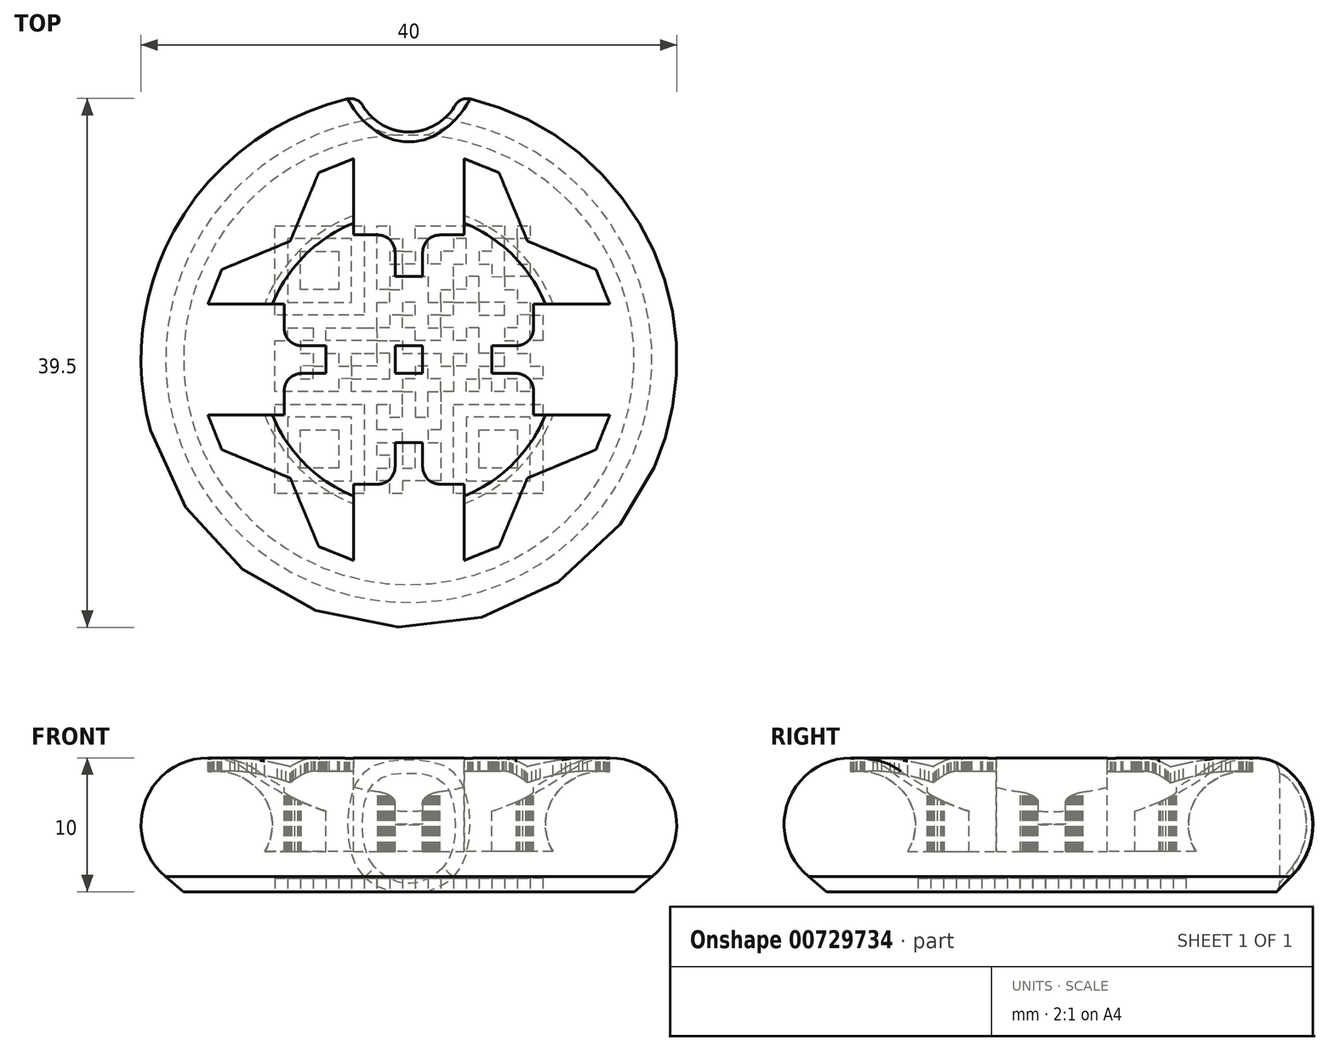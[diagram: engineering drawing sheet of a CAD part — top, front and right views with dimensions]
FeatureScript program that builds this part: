
annotation { "Feature Type Name" : "Feature", "Feature Type Description" : "" }
export const myFeature = defineFeature(function(context is Context, id is Id, definition is map)
    precondition{}
    {
        {
            var Q0;
            Q0=qCreatedBy(makeId("Front.planeOp"),FACE);
            var sketch = newSketch(context, id + "F0", { "sketchPlane" : qUnion([Q0])});
            skArc(sketch, "E0", {"start": v(-12, 9) * mm, "mid": v(-6.32, 6.03) * mm, "end": v(0, 5) * mm});
            skArc(sketch, "E1", {"start": v(-12, 9) * mm, "mid": v(-19.74, 6.58) * mm, "end": v(-15, 0) * mm});
            skLineSegment(sketch, "E2", {"start": v(0, 0) * mm, "end": v(-15, 0) * mm});
            skLineSegment(sketch, "E3", {"start": v(0, 0) * mm, "end": v(0, 5) * mm});
            skLineSegment(sketch, "E4", {"start": v(-18.21, 1.17) * mm, "end": v(-16.82, 0) * mm});
            skLineSegment(sketch, "E5", {"start": v(-16.82, 0) * mm, "end": v(-15, 0) * mm});
            skSolve(sketch);
        }
        {
            var Q0;
            Q0=qSketchRegion(id+"F0",true);
            var Q1;
            Q1=sQuery(id+"F0.wireOp",EDGE,"E3");
            revolve(context, id + "F1", {"surfaceOperationType" : NewSurfaceOperationType.NEW, "entities" : qUnion([Q0]), "axis" : qUnion([Q1]), "revolveType" : RevolveType.FULL});
        }
        {
            var Q0;
            Q0=qCreatedBy(makeId("Top.planeOp"),FACE);
            cPlane(context, id + "F2", {"entities" : qUnion([Q0]), "cplaneType" : CPlaneType.OFFSET, "offset" : 15 * mm, "width" : 150 * mm, "height" : 150 * mm});
        }
        {
            var Q0;
            Q0=qCreatedBy(id+"F2.planeOp",FACE);
            var sketch = newSketch(context, id + "F3", { "sketchPlane" : qUnion([Q0])});
            skLineSegment(sketch, "E6", {"start": v(9.31, -4.14) * mm, "end": v(9.31, -4.02) * mm});
            skLineSegment(sketch, "E7", {"start": v(9.31, -4.02) * mm, "end": v(9.31, -3.91) * mm});
            skLineSegment(sketch, "E8", {"start": v(9.31, -3.91) * mm, "end": v(9.31, -3.8) * mm});
            skLineSegment(sketch, "E9", {"start": v(9.31, -3.8) * mm, "end": v(9.31, -3.69) * mm});
            skLineSegment(sketch, "E10", {"start": v(9.31, -3.69) * mm, "end": v(9.31, -3.57) * mm});
            skLineSegment(sketch, "E11", {"start": v(9.31, -3.57) * mm, "end": v(9.31, -3.46) * mm});
            skLineSegment(sketch, "E12", {"start": v(9.31, -3.46) * mm, "end": v(9.31, -3.35) * mm});
            skLineSegment(sketch, "E13", {"start": v(9.31, -3.35) * mm, "end": v(9.31, -3.23) * mm});
            skLineSegment(sketch, "E14", {"start": v(9.31, -3.23) * mm, "end": v(9.31, -3.12) * mm});
            skLineSegment(sketch, "E15", {"start": v(9.31, -3.12) * mm, "end": v(9.31, -3) * mm});
            skLineSegment(sketch, "E16", {"start": v(9.31, -3) * mm, "end": v(9.31, -2.9) * mm});
            skLineSegment(sketch, "E17", {"start": v(9.31, -2.9) * mm, "end": v(9.31, -2.78) * mm});
            skLineSegment(sketch, "E18", {"start": v(9.31, -2.78) * mm, "end": v(9.31, -2.67) * mm});
            skLineSegment(sketch, "E19", {"start": v(9.31, -2.67) * mm, "end": v(9.31, -2.55) * mm});
            skLineSegment(sketch, "E20", {"start": v(9.31, -2.55) * mm, "end": v(9.31, -2.44) * mm});
            skLineSegment(sketch, "E21", {"start": v(9.31, -2.44) * mm, "end": v(9.31, -2.33) * mm});
            skLineSegment(sketch, "E22", {"start": v(9.31, -2.33) * mm, "end": v(9.3, -2.2) * mm});
            skLineSegment(sketch, "E23", {"start": v(9.3, -2.2) * mm, "end": v(9.28, -2.07) * mm});
            skLineSegment(sketch, "E24", {"start": v(9.28, -2.07) * mm, "end": v(9.25, -1.94) * mm});
            skLineSegment(sketch, "E25", {"start": v(9.25, -1.94) * mm, "end": v(9.2, -1.82) * mm});
            skLineSegment(sketch, "E26", {"start": v(9.2, -1.82) * mm, "end": v(9.15, -1.71) * mm});
            skLineSegment(sketch, "E27", {"start": v(9.15, -1.71) * mm, "end": v(9.09, -1.6) * mm});
            skLineSegment(sketch, "E28", {"start": v(9.09, -1.6) * mm, "end": v(9.02, -1.5) * mm});
            skLineSegment(sketch, "E29", {"start": v(9.02, -1.5) * mm, "end": v(8.93, -1.41) * mm});
            skLineSegment(sketch, "E30", {"start": v(8.93, -1.41) * mm, "end": v(8.84, -1.33) * mm});
            skLineSegment(sketch, "E31", {"start": v(8.84, -1.33) * mm, "end": v(8.74, -1.26) * mm});
            skLineSegment(sketch, "E32", {"start": v(8.74, -1.26) * mm, "end": v(8.63, -1.2) * mm});
            skLineSegment(sketch, "E33", {"start": v(8.63, -1.2) * mm, "end": v(8.52, -1.14) * mm});
            skLineSegment(sketch, "E34", {"start": v(8.52, -1.14) * mm, "end": v(8.4, -1.1) * mm});
            skLineSegment(sketch, "E35", {"start": v(8.4, -1.1) * mm, "end": v(8.28, -1.06) * mm});
            skLineSegment(sketch, "E36", {"start": v(8.28, -1.06) * mm, "end": v(8.15, -1.04) * mm});
            skLineSegment(sketch, "E37", {"start": v(8.15, -1.04) * mm, "end": v(8.02, -1.03) * mm});
            skLineSegment(sketch, "E38", {"start": v(8.02, -1.03) * mm, "end": v(7.9, -1.03) * mm});
            skLineSegment(sketch, "E39", {"start": v(7.9, -1.03) * mm, "end": v(7.8, -1.03) * mm});
            skLineSegment(sketch, "E40", {"start": v(7.8, -1.03) * mm, "end": v(7.68, -1.03) * mm});
            skLineSegment(sketch, "E41", {"start": v(7.68, -1.03) * mm, "end": v(7.56, -1.03) * mm});
            skLineSegment(sketch, "E42", {"start": v(7.56, -1.03) * mm, "end": v(7.45, -1.03) * mm});
            skLineSegment(sketch, "E43", {"start": v(7.45, -1.03) * mm, "end": v(7.34, -1.03) * mm});
            skLineSegment(sketch, "E44", {"start": v(7.34, -1.03) * mm, "end": v(7.23, -1.03) * mm});
            skLineSegment(sketch, "E45", {"start": v(7.23, -1.03) * mm, "end": v(7.11, -1.03) * mm});
            skLineSegment(sketch, "E46", {"start": v(7.11, -1.03) * mm, "end": v(7, -1.03) * mm});
            skLineSegment(sketch, "E47", {"start": v(7, -1.03) * mm, "end": v(6.89, -1.03) * mm});
            skLineSegment(sketch, "E48", {"start": v(6.89, -1.03) * mm, "end": v(6.77, -1.03) * mm});
            skLineSegment(sketch, "E49", {"start": v(6.77, -1.03) * mm, "end": v(6.66, -1.03) * mm});
            skLineSegment(sketch, "E50", {"start": v(6.66, -1.03) * mm, "end": v(6.55, -1.03) * mm});
            skLineSegment(sketch, "E51", {"start": v(6.55, -1.03) * mm, "end": v(6.43, -1.03) * mm});
            skLineSegment(sketch, "E52", {"start": v(6.43, -1.03) * mm, "end": v(6.32, -1.03) * mm});
            skLineSegment(sketch, "E53", {"start": v(6.32, -1.03) * mm, "end": v(6.2, -1.03) * mm});
            skLineSegment(sketch, "E54", {"start": v(6.2, -1.03) * mm, "end": v(6.2, -0.97) * mm});
            skLineSegment(sketch, "E55", {"start": v(6.2, -0.97) * mm, "end": v(6.2, -0.9) * mm});
            skLineSegment(sketch, "E56", {"start": v(6.2, -0.9) * mm, "end": v(6.2, -0.84) * mm});
            skLineSegment(sketch, "E57", {"start": v(6.2, -0.84) * mm, "end": v(6.2, -0.78) * mm});
            skLineSegment(sketch, "E58", {"start": v(6.2, -0.78) * mm, "end": v(6.2, -0.71) * mm});
            skLineSegment(sketch, "E59", {"start": v(6.2, -0.71) * mm, "end": v(6.2, -0.65) * mm});
            skLineSegment(sketch, "E60", {"start": v(6.2, -0.65) * mm, "end": v(6.2, -0.58) * mm});
            skLineSegment(sketch, "E61", {"start": v(6.2, -0.58) * mm, "end": v(6.2, -0.52) * mm});
            skLineSegment(sketch, "E62", {"start": v(6.2, -0.52) * mm, "end": v(6.2, -0.45) * mm});
            skLineSegment(sketch, "E63", {"start": v(6.2, -0.45) * mm, "end": v(6.2, -0.39) * mm});
            skLineSegment(sketch, "E64", {"start": v(6.2, -0.39) * mm, "end": v(6.2, -0.32) * mm});
            skLineSegment(sketch, "E65", {"start": v(6.2, -0.32) * mm, "end": v(6.2, -0.26) * mm});
            skLineSegment(sketch, "E66", {"start": v(6.2, -0.26) * mm, "end": v(6.2, -0.2) * mm});
            skLineSegment(sketch, "E67", {"start": v(6.2, -0.2) * mm, "end": v(6.2, -0.13) * mm});
            skLineSegment(sketch, "E68", {"start": v(6.2, -0.13) * mm, "end": v(6.2, -0.06) * mm});
            skLineSegment(sketch, "E69", {"start": v(6.2, -0.06) * mm, "end": v(6.2, 0) * mm});
            skLineSegment(sketch, "E70", {"start": v(6.2, 0) * mm, "end": v(6.2, 0.06) * mm});
            skLineSegment(sketch, "E71", {"start": v(6.2, 0.06) * mm, "end": v(6.2, 0.13) * mm});
            skLineSegment(sketch, "E72", {"start": v(6.2, 0.13) * mm, "end": v(6.2, 0.2) * mm});
            skLineSegment(sketch, "E73", {"start": v(6.2, 0.2) * mm, "end": v(6.2, 0.26) * mm});
            skLineSegment(sketch, "E74", {"start": v(6.2, 0.26) * mm, "end": v(6.2, 0.32) * mm});
            skLineSegment(sketch, "E75", {"start": v(6.2, 0.32) * mm, "end": v(6.2, 0.39) * mm});
            skLineSegment(sketch, "E76", {"start": v(6.2, 0.39) * mm, "end": v(6.2, 0.45) * mm});
            skLineSegment(sketch, "E77", {"start": v(6.2, 0.45) * mm, "end": v(6.2, 0.52) * mm});
            skLineSegment(sketch, "E78", {"start": v(6.2, 0.52) * mm, "end": v(6.2, 0.58) * mm});
            skLineSegment(sketch, "E79", {"start": v(6.2, 0.58) * mm, "end": v(6.2, 0.65) * mm});
            skLineSegment(sketch, "E80", {"start": v(6.2, 0.65) * mm, "end": v(6.2, 0.71) * mm});
            skLineSegment(sketch, "E81", {"start": v(6.2, 0.71) * mm, "end": v(6.2, 0.78) * mm});
            skLineSegment(sketch, "E82", {"start": v(6.2, 0.78) * mm, "end": v(6.2, 0.84) * mm});
            skLineSegment(sketch, "E83", {"start": v(6.2, 0.84) * mm, "end": v(6.2, 0.9) * mm});
            skLineSegment(sketch, "E84", {"start": v(6.2, 0.9) * mm, "end": v(6.2, 0.97) * mm});
            skLineSegment(sketch, "E85", {"start": v(6.2, 0.97) * mm, "end": v(6.2, 1.03) * mm});
            skLineSegment(sketch, "E86", {"start": v(6.2, 1.03) * mm, "end": v(6.32, 1.03) * mm});
            skLineSegment(sketch, "E87", {"start": v(6.32, 1.03) * mm, "end": v(6.43, 1.03) * mm});
            skLineSegment(sketch, "E88", {"start": v(6.43, 1.03) * mm, "end": v(6.55, 1.03) * mm});
            skLineSegment(sketch, "E89", {"start": v(6.55, 1.03) * mm, "end": v(6.66, 1.03) * mm});
            skLineSegment(sketch, "E90", {"start": v(6.66, 1.03) * mm, "end": v(6.77, 1.03) * mm});
            skLineSegment(sketch, "E91", {"start": v(6.77, 1.03) * mm, "end": v(6.89, 1.03) * mm});
            skLineSegment(sketch, "E92", {"start": v(6.89, 1.03) * mm, "end": v(7, 1.03) * mm});
            skLineSegment(sketch, "E93", {"start": v(7, 1.03) * mm, "end": v(7.11, 1.03) * mm});
            skLineSegment(sketch, "E94", {"start": v(7.11, 1.03) * mm, "end": v(7.23, 1.03) * mm});
            skLineSegment(sketch, "E95", {"start": v(7.23, 1.03) * mm, "end": v(7.34, 1.03) * mm});
            skLineSegment(sketch, "E96", {"start": v(7.34, 1.03) * mm, "end": v(7.45, 1.03) * mm});
            skLineSegment(sketch, "E97", {"start": v(7.45, 1.03) * mm, "end": v(7.56, 1.03) * mm});
            skLineSegment(sketch, "E98", {"start": v(7.56, 1.03) * mm, "end": v(7.68, 1.03) * mm});
            skLineSegment(sketch, "E99", {"start": v(7.68, 1.03) * mm, "end": v(7.8, 1.03) * mm});
            skLineSegment(sketch, "E100", {"start": v(7.8, 1.03) * mm, "end": v(7.9, 1.03) * mm});
            skLineSegment(sketch, "E101", {"start": v(7.9, 1.03) * mm, "end": v(8.02, 1.03) * mm});
            skLineSegment(sketch, "E102", {"start": v(8.02, 1.03) * mm, "end": v(8.15, 1.04) * mm});
            skLineSegment(sketch, "E103", {"start": v(8.15, 1.04) * mm, "end": v(8.28, 1.06) * mm});
            skLineSegment(sketch, "E104", {"start": v(8.28, 1.06) * mm, "end": v(8.4, 1.1) * mm});
            skLineSegment(sketch, "E105", {"start": v(8.4, 1.1) * mm, "end": v(8.52, 1.14) * mm});
            skLineSegment(sketch, "E106", {"start": v(8.52, 1.14) * mm, "end": v(8.63, 1.2) * mm});
            skLineSegment(sketch, "E107", {"start": v(8.63, 1.2) * mm, "end": v(8.74, 1.26) * mm});
            skLineSegment(sketch, "E108", {"start": v(8.74, 1.26) * mm, "end": v(8.84, 1.33) * mm});
            skLineSegment(sketch, "E109", {"start": v(8.84, 1.33) * mm, "end": v(8.93, 1.41) * mm});
            skLineSegment(sketch, "E110", {"start": v(8.93, 1.41) * mm, "end": v(9.02, 1.5) * mm});
            skLineSegment(sketch, "E111", {"start": v(9.02, 1.5) * mm, "end": v(9.09, 1.6) * mm});
            skLineSegment(sketch, "E112", {"start": v(9.09, 1.6) * mm, "end": v(9.15, 1.71) * mm});
            skLineSegment(sketch, "E113", {"start": v(9.15, 1.71) * mm, "end": v(9.2, 1.82) * mm});
            skLineSegment(sketch, "E114", {"start": v(9.2, 1.82) * mm, "end": v(9.25, 1.94) * mm});
            skLineSegment(sketch, "E115", {"start": v(9.25, 1.94) * mm, "end": v(9.28, 2.07) * mm});
            skLineSegment(sketch, "E116", {"start": v(9.28, 2.07) * mm, "end": v(9.3, 2.2) * mm});
            skLineSegment(sketch, "E117", {"start": v(9.3, 2.2) * mm, "end": v(9.31, 2.33) * mm});
            skLineSegment(sketch, "E118", {"start": v(9.31, 2.33) * mm, "end": v(9.31, 2.44) * mm});
            skLineSegment(sketch, "E119", {"start": v(9.31, 2.44) * mm, "end": v(9.31, 2.55) * mm});
            skLineSegment(sketch, "E120", {"start": v(9.31, 2.55) * mm, "end": v(9.31, 2.67) * mm});
            skLineSegment(sketch, "E121", {"start": v(9.31, 2.67) * mm, "end": v(9.31, 2.78) * mm});
            skLineSegment(sketch, "E122", {"start": v(9.31, 2.78) * mm, "end": v(9.31, 2.9) * mm});
            skLineSegment(sketch, "E123", {"start": v(9.31, 2.9) * mm, "end": v(9.31, 3) * mm});
            skLineSegment(sketch, "E124", {"start": v(9.31, 3) * mm, "end": v(9.31, 3.12) * mm});
            skLineSegment(sketch, "E125", {"start": v(9.31, 3.12) * mm, "end": v(9.31, 3.23) * mm});
            skLineSegment(sketch, "E126", {"start": v(9.31, 3.23) * mm, "end": v(9.31, 3.35) * mm});
            skLineSegment(sketch, "E127", {"start": v(9.31, 3.35) * mm, "end": v(9.31, 3.46) * mm});
            skLineSegment(sketch, "E128", {"start": v(9.31, 3.46) * mm, "end": v(9.31, 3.57) * mm});
            skLineSegment(sketch, "E129", {"start": v(9.31, 3.57) * mm, "end": v(9.31, 3.69) * mm});
            skLineSegment(sketch, "E130", {"start": v(9.31, 3.69) * mm, "end": v(9.31, 3.8) * mm});
            skLineSegment(sketch, "E131", {"start": v(9.31, 3.8) * mm, "end": v(9.31, 3.91) * mm});
            skLineSegment(sketch, "E132", {"start": v(9.31, 3.91) * mm, "end": v(9.31, 4.02) * mm});
            skLineSegment(sketch, "E133", {"start": v(9.31, 4.02) * mm, "end": v(9.31, 4.14) * mm});
            skLineSegment(sketch, "E134", {"start": v(9.31, 4.14) * mm, "end": v(9.44, 4.14) * mm});
            skLineSegment(sketch, "E135", {"start": v(9.44, 4.14) * mm, "end": v(9.57, 4.14) * mm});
            skLineSegment(sketch, "E136", {"start": v(9.57, 4.14) * mm, "end": v(9.7, 4.14) * mm});
            skLineSegment(sketch, "E137", {"start": v(9.7, 4.14) * mm, "end": v(9.83, 4.14) * mm});
            skLineSegment(sketch, "E138", {"start": v(9.83, 4.14) * mm, "end": v(9.96, 4.14) * mm});
            skLineSegment(sketch, "E139", {"start": v(9.96, 4.14) * mm, "end": v(10.09, 4.14) * mm});
            skLineSegment(sketch, "E140", {"start": v(10.09, 4.14) * mm, "end": v(10.22, 4.14) * mm});
            skLineSegment(sketch, "E141", {"start": v(10.22, 4.14) * mm, "end": v(10.34, 4.14) * mm});
            skLineSegment(sketch, "E142", {"start": v(10.34, 4.14) * mm, "end": v(10.47, 4.14) * mm});
            skLineSegment(sketch, "E143", {"start": v(10.47, 4.14) * mm, "end": v(10.6, 4.14) * mm});
            skLineSegment(sketch, "E144", {"start": v(10.6, 4.14) * mm, "end": v(10.73, 4.14) * mm});
            skLineSegment(sketch, "E145", {"start": v(10.73, 4.14) * mm, "end": v(10.86, 4.14) * mm});
            skLineSegment(sketch, "E146", {"start": v(10.86, 4.14) * mm, "end": v(11, 4.14) * mm});
            skLineSegment(sketch, "E147", {"start": v(11, 4.14) * mm, "end": v(11.12, 4.14) * mm});
            skLineSegment(sketch, "E148", {"start": v(11.12, 4.14) * mm, "end": v(11.25, 4.14) * mm});
            skLineSegment(sketch, "E149", {"start": v(11.25, 4.14) * mm, "end": v(11.38, 4.14) * mm});
            skLineSegment(sketch, "E150", {"start": v(11.38, 4.14) * mm, "end": v(11.6, 4.14) * mm});
            skLineSegment(sketch, "E151", {"start": v(11.6, 4.14) * mm, "end": v(11.83, 4.14) * mm});
            skLineSegment(sketch, "E152", {"start": v(11.83, 4.14) * mm, "end": v(12.06, 4.14) * mm});
            skLineSegment(sketch, "E153", {"start": v(12.06, 4.14) * mm, "end": v(12.28, 4.14) * mm});
            skLineSegment(sketch, "E154", {"start": v(12.28, 4.14) * mm, "end": v(12.51, 4.14) * mm});
            skLineSegment(sketch, "E155", {"start": v(12.51, 4.14) * mm, "end": v(12.74, 4.14) * mm});
            skLineSegment(sketch, "E156", {"start": v(12.74, 4.14) * mm, "end": v(12.96, 4.14) * mm});
            skLineSegment(sketch, "E157", {"start": v(12.96, 4.14) * mm, "end": v(13.19, 4.14) * mm});
            skLineSegment(sketch, "E158", {"start": v(13.19, 4.14) * mm, "end": v(13.42, 4.14) * mm});
            skLineSegment(sketch, "E159", {"start": v(13.42, 4.14) * mm, "end": v(13.64, 4.14) * mm});
            skLineSegment(sketch, "E160", {"start": v(13.64, 4.14) * mm, "end": v(13.87, 4.14) * mm});
            skLineSegment(sketch, "E161", {"start": v(13.87, 4.14) * mm, "end": v(14.1, 4.14) * mm});
            skLineSegment(sketch, "E162", {"start": v(14.1, 4.14) * mm, "end": v(14.32, 4.14) * mm});
            skLineSegment(sketch, "E163", {"start": v(14.32, 4.14) * mm, "end": v(14.55, 4.14) * mm});
            skLineSegment(sketch, "E164", {"start": v(14.55, 4.14) * mm, "end": v(14.77, 4.14) * mm});
            skLineSegment(sketch, "E165", {"start": v(14.77, 4.14) * mm, "end": v(15, 4.14) * mm});
            skLineSegment(sketch, "E166", {"start": v(15, 4.14) * mm, "end": v(14.95, 4.27) * mm});
            skLineSegment(sketch, "E167", {"start": v(14.95, 4.27) * mm, "end": v(14.9, 4.4) * mm});
            skLineSegment(sketch, "E168", {"start": v(14.9, 4.4) * mm, "end": v(14.84, 4.53) * mm});
            skLineSegment(sketch, "E169", {"start": v(14.84, 4.53) * mm, "end": v(14.8, 4.66) * mm});
            skLineSegment(sketch, "E170", {"start": v(14.8, 4.66) * mm, "end": v(14.74, 4.78) * mm});
            skLineSegment(sketch, "E171", {"start": v(14.74, 4.78) * mm, "end": v(14.69, 4.91) * mm});
            skLineSegment(sketch, "E172", {"start": v(14.69, 4.91) * mm, "end": v(14.64, 5.04) * mm});
            skLineSegment(sketch, "E173", {"start": v(14.64, 5.04) * mm, "end": v(14.59, 5.17) * mm});
            skLineSegment(sketch, "E174", {"start": v(14.59, 5.17) * mm, "end": v(14.53, 5.3) * mm});
            skLineSegment(sketch, "E175", {"start": v(14.53, 5.3) * mm, "end": v(14.48, 5.43) * mm});
            skLineSegment(sketch, "E176", {"start": v(14.48, 5.43) * mm, "end": v(14.43, 5.56) * mm});
            skLineSegment(sketch, "E177", {"start": v(14.43, 5.56) * mm, "end": v(14.38, 5.69) * mm});
            skLineSegment(sketch, "E178", {"start": v(14.38, 5.69) * mm, "end": v(14.33, 5.82) * mm});
            skLineSegment(sketch, "E179", {"start": v(14.33, 5.82) * mm, "end": v(14.28, 5.95) * mm});
            skLineSegment(sketch, "E180", {"start": v(14.28, 5.95) * mm, "end": v(14.22, 6.08) * mm});
            skLineSegment(sketch, "E181", {"start": v(14.22, 6.08) * mm, "end": v(14.17, 6.2) * mm});
            skLineSegment(sketch, "E182", {"start": v(14.17, 6.2) * mm, "end": v(14.16, 6.24) * mm});
            skLineSegment(sketch, "E183", {"start": v(14.16, 6.24) * mm, "end": v(14.15, 6.27) * mm});
            skLineSegment(sketch, "E184", {"start": v(14.15, 6.27) * mm, "end": v(14.13, 6.3) * mm});
            skLineSegment(sketch, "E185", {"start": v(14.13, 6.3) * mm, "end": v(14.12, 6.34) * mm});
            skLineSegment(sketch, "E186", {"start": v(14.12, 6.34) * mm, "end": v(14.1, 6.37) * mm});
            skLineSegment(sketch, "E187", {"start": v(14.1, 6.37) * mm, "end": v(14.1, 6.4) * mm});
            skLineSegment(sketch, "E188", {"start": v(14.1, 6.4) * mm, "end": v(14.08, 6.43) * mm});
            skLineSegment(sketch, "E189", {"start": v(14.08, 6.43) * mm, "end": v(14.07, 6.47) * mm});
            skLineSegment(sketch, "E190", {"start": v(14.07, 6.47) * mm, "end": v(14.06, 6.5) * mm});
            skLineSegment(sketch, "E191", {"start": v(14.06, 6.5) * mm, "end": v(14.04, 6.53) * mm});
            skLineSegment(sketch, "E192", {"start": v(14.04, 6.53) * mm, "end": v(14.03, 6.56) * mm});
            skLineSegment(sketch, "E193", {"start": v(14.03, 6.56) * mm, "end": v(14.02, 6.6) * mm});
            skLineSegment(sketch, "E194", {"start": v(14.02, 6.6) * mm, "end": v(14, 6.63) * mm});
            skLineSegment(sketch, "E195", {"start": v(14, 6.63) * mm, "end": v(14, 6.66) * mm});
            skLineSegment(sketch, "E196", {"start": v(14, 6.66) * mm, "end": v(13.98, 6.7) * mm});
            skLineSegment(sketch, "E197", {"start": v(13.98, 6.7) * mm, "end": v(13.97, 6.72) * mm});
            skLineSegment(sketch, "E198", {"start": v(13.97, 6.72) * mm, "end": v(13.65, 6.86) * mm});
            skLineSegment(sketch, "E199", {"start": v(13.65, 6.86) * mm, "end": v(13.33, 7) * mm});
            skLineSegment(sketch, "E200", {"start": v(13.33, 7) * mm, "end": v(13, 7.12) * mm});
            skLineSegment(sketch, "E201", {"start": v(13, 7.12) * mm, "end": v(12.69, 7.26) * mm});
            skLineSegment(sketch, "E202", {"start": v(12.69, 7.26) * mm, "end": v(12.37, 7.39) * mm});
            skLineSegment(sketch, "E203", {"start": v(12.37, 7.39) * mm, "end": v(12.05, 7.52) * mm});
            skLineSegment(sketch, "E204", {"start": v(12.05, 7.52) * mm, "end": v(11.73, 7.66) * mm});
            skLineSegment(sketch, "E205", {"start": v(11.73, 7.66) * mm, "end": v(11.4, 7.79) * mm});
            skLineSegment(sketch, "E206", {"start": v(11.4, 7.79) * mm, "end": v(11.1, 7.92) * mm});
            skLineSegment(sketch, "E207", {"start": v(11.1, 7.92) * mm, "end": v(10.77, 8.06) * mm});
            skLineSegment(sketch, "E208", {"start": v(10.77, 8.06) * mm, "end": v(10.45, 8.19) * mm});
            skLineSegment(sketch, "E209", {"start": v(10.45, 8.19) * mm, "end": v(10.13, 8.32) * mm});
            skLineSegment(sketch, "E210", {"start": v(10.13, 8.32) * mm, "end": v(9.81, 8.45) * mm});
            skLineSegment(sketch, "E211", {"start": v(9.81, 8.45) * mm, "end": v(9.5, 8.59) * mm});
            skLineSegment(sketch, "E212", {"start": v(9.5, 8.59) * mm, "end": v(9.17, 8.72) * mm});
            skLineSegment(sketch, "E213", {"start": v(9.17, 8.72) * mm, "end": v(8.85, 8.85) * mm});
            skLineSegment(sketch, "E214", {"start": v(8.85, 8.85) * mm, "end": v(8.72, 9.17) * mm});
            skLineSegment(sketch, "E215", {"start": v(8.72, 9.17) * mm, "end": v(8.59, 9.5) * mm});
            skLineSegment(sketch, "E216", {"start": v(8.59, 9.5) * mm, "end": v(8.45, 9.81) * mm});
            skLineSegment(sketch, "E217", {"start": v(8.45, 9.81) * mm, "end": v(8.32, 10.13) * mm});
            skLineSegment(sketch, "E218", {"start": v(8.32, 10.13) * mm, "end": v(8.19, 10.45) * mm});
            skLineSegment(sketch, "E219", {"start": v(8.19, 10.45) * mm, "end": v(8.06, 10.77) * mm});
            skLineSegment(sketch, "E220", {"start": v(8.06, 10.77) * mm, "end": v(7.92, 11.1) * mm});
            skLineSegment(sketch, "E221", {"start": v(7.92, 11.1) * mm, "end": v(7.79, 11.4) * mm});
            skLineSegment(sketch, "E222", {"start": v(7.79, 11.4) * mm, "end": v(7.66, 11.73) * mm});
            skLineSegment(sketch, "E223", {"start": v(7.66, 11.73) * mm, "end": v(7.52, 12.05) * mm});
            skLineSegment(sketch, "E224", {"start": v(7.52, 12.05) * mm, "end": v(7.39, 12.37) * mm});
            skLineSegment(sketch, "E225", {"start": v(7.39, 12.37) * mm, "end": v(7.26, 12.69) * mm});
            skLineSegment(sketch, "E226", {"start": v(7.26, 12.69) * mm, "end": v(7.12, 13) * mm});
            skLineSegment(sketch, "E227", {"start": v(7.12, 13) * mm, "end": v(7, 13.33) * mm});
            skLineSegment(sketch, "E228", {"start": v(7, 13.33) * mm, "end": v(6.86, 13.65) * mm});
            skLineSegment(sketch, "E229", {"start": v(6.86, 13.65) * mm, "end": v(6.72, 13.97) * mm});
            skLineSegment(sketch, "E230", {"start": v(6.72, 13.97) * mm, "end": v(6.7, 13.98) * mm});
            skLineSegment(sketch, "E231", {"start": v(6.7, 13.98) * mm, "end": v(6.66, 14) * mm});
            skLineSegment(sketch, "E232", {"start": v(6.66, 14) * mm, "end": v(6.63, 14) * mm});
            skLineSegment(sketch, "E233", {"start": v(6.63, 14) * mm, "end": v(6.6, 14.02) * mm});
            skLineSegment(sketch, "E234", {"start": v(6.6, 14.02) * mm, "end": v(6.56, 14.03) * mm});
            skLineSegment(sketch, "E235", {"start": v(6.56, 14.03) * mm, "end": v(6.53, 14.04) * mm});
            skLineSegment(sketch, "E236", {"start": v(6.53, 14.04) * mm, "end": v(6.5, 14.06) * mm});
            skLineSegment(sketch, "E237", {"start": v(6.5, 14.06) * mm, "end": v(6.47, 14.07) * mm});
            skLineSegment(sketch, "E238", {"start": v(6.47, 14.07) * mm, "end": v(6.43, 14.08) * mm});
            skLineSegment(sketch, "E239", {"start": v(6.43, 14.08) * mm, "end": v(6.4, 14.1) * mm});
            skLineSegment(sketch, "E240", {"start": v(6.4, 14.1) * mm, "end": v(6.37, 14.1) * mm});
            skLineSegment(sketch, "E241", {"start": v(6.37, 14.1) * mm, "end": v(6.34, 14.12) * mm});
            skLineSegment(sketch, "E242", {"start": v(6.34, 14.12) * mm, "end": v(6.3, 14.13) * mm});
            skLineSegment(sketch, "E243", {"start": v(6.3, 14.13) * mm, "end": v(6.27, 14.15) * mm});
            skLineSegment(sketch, "E244", {"start": v(6.27, 14.15) * mm, "end": v(6.24, 14.16) * mm});
            skLineSegment(sketch, "E245", {"start": v(6.24, 14.16) * mm, "end": v(6.2, 14.17) * mm});
            skLineSegment(sketch, "E246", {"start": v(6.2, 14.17) * mm, "end": v(6.08, 14.22) * mm});
            skLineSegment(sketch, "E247", {"start": v(6.08, 14.22) * mm, "end": v(5.95, 14.28) * mm});
            skLineSegment(sketch, "E248", {"start": v(5.95, 14.28) * mm, "end": v(5.82, 14.33) * mm});
            skLineSegment(sketch, "E249", {"start": v(5.82, 14.33) * mm, "end": v(5.69, 14.38) * mm});
            skLineSegment(sketch, "E250", {"start": v(5.69, 14.38) * mm, "end": v(5.56, 14.43) * mm});
            skLineSegment(sketch, "E251", {"start": v(5.56, 14.43) * mm, "end": v(5.43, 14.48) * mm});
            skLineSegment(sketch, "E252", {"start": v(5.43, 14.48) * mm, "end": v(5.3, 14.53) * mm});
            skLineSegment(sketch, "E253", {"start": v(5.3, 14.53) * mm, "end": v(5.17, 14.59) * mm});
            skLineSegment(sketch, "E254", {"start": v(5.17, 14.59) * mm, "end": v(5.04, 14.64) * mm});
            skLineSegment(sketch, "E255", {"start": v(5.04, 14.64) * mm, "end": v(4.91, 14.69) * mm});
            skLineSegment(sketch, "E256", {"start": v(4.91, 14.69) * mm, "end": v(4.78, 14.74) * mm});
            skLineSegment(sketch, "E257", {"start": v(4.78, 14.74) * mm, "end": v(4.66, 14.8) * mm});
            skLineSegment(sketch, "E258", {"start": v(4.66, 14.8) * mm, "end": v(4.53, 14.84) * mm});
            skLineSegment(sketch, "E259", {"start": v(4.53, 14.84) * mm, "end": v(4.4, 14.9) * mm});
            skLineSegment(sketch, "E260", {"start": v(4.4, 14.9) * mm, "end": v(4.27, 14.95) * mm});
            skLineSegment(sketch, "E261", {"start": v(4.27, 14.95) * mm, "end": v(4.14, 15) * mm});
            skLineSegment(sketch, "E262", {"start": v(4.14, 15) * mm, "end": v(4.14, 14.77) * mm});
            skLineSegment(sketch, "E263", {"start": v(4.14, 14.77) * mm, "end": v(4.14, 14.55) * mm});
            skLineSegment(sketch, "E264", {"start": v(4.14, 14.55) * mm, "end": v(4.14, 14.32) * mm});
            skLineSegment(sketch, "E265", {"start": v(4.14, 14.32) * mm, "end": v(4.14, 14.1) * mm});
            skLineSegment(sketch, "E266", {"start": v(4.14, 14.1) * mm, "end": v(4.14, 13.87) * mm});
            skLineSegment(sketch, "E267", {"start": v(4.14, 13.87) * mm, "end": v(4.14, 13.64) * mm});
            skLineSegment(sketch, "E268", {"start": v(4.14, 13.64) * mm, "end": v(4.14, 13.42) * mm});
            skLineSegment(sketch, "E269", {"start": v(4.14, 13.42) * mm, "end": v(4.14, 13.19) * mm});
            skLineSegment(sketch, "E270", {"start": v(4.14, 13.19) * mm, "end": v(4.14, 12.96) * mm});
            skLineSegment(sketch, "E271", {"start": v(4.14, 12.96) * mm, "end": v(4.14, 12.74) * mm});
            skLineSegment(sketch, "E272", {"start": v(4.14, 12.74) * mm, "end": v(4.14, 12.51) * mm});
            skLineSegment(sketch, "E273", {"start": v(4.14, 12.51) * mm, "end": v(4.14, 12.28) * mm});
            skLineSegment(sketch, "E274", {"start": v(4.14, 12.28) * mm, "end": v(4.14, 12.06) * mm});
            skLineSegment(sketch, "E275", {"start": v(4.14, 12.06) * mm, "end": v(4.14, 11.83) * mm});
            skLineSegment(sketch, "E276", {"start": v(4.14, 11.83) * mm, "end": v(4.14, 11.6) * mm});
            skLineSegment(sketch, "E277", {"start": v(4.14, 11.6) * mm, "end": v(4.14, 11.38) * mm});
            skLineSegment(sketch, "E278", {"start": v(4.14, 11.38) * mm, "end": v(4.14, 11.25) * mm});
            skLineSegment(sketch, "E279", {"start": v(4.14, 11.25) * mm, "end": v(4.14, 11.12) * mm});
            skLineSegment(sketch, "E280", {"start": v(4.14, 11.12) * mm, "end": v(4.14, 11) * mm});
            skLineSegment(sketch, "E281", {"start": v(4.14, 11) * mm, "end": v(4.14, 10.86) * mm});
            skLineSegment(sketch, "E282", {"start": v(4.14, 10.86) * mm, "end": v(4.14, 10.73) * mm});
            skLineSegment(sketch, "E283", {"start": v(4.14, 10.73) * mm, "end": v(4.14, 10.6) * mm});
            skLineSegment(sketch, "E284", {"start": v(4.14, 10.6) * mm, "end": v(4.14, 10.47) * mm});
            skLineSegment(sketch, "E285", {"start": v(4.14, 10.47) * mm, "end": v(4.14, 10.34) * mm});
            skLineSegment(sketch, "E286", {"start": v(4.14, 10.34) * mm, "end": v(4.14, 10.22) * mm});
            skLineSegment(sketch, "E287", {"start": v(4.14, 10.22) * mm, "end": v(4.14, 10.09) * mm});
            skLineSegment(sketch, "E288", {"start": v(4.14, 10.09) * mm, "end": v(4.14, 9.96) * mm});
            skLineSegment(sketch, "E289", {"start": v(4.14, 9.96) * mm, "end": v(4.14, 9.83) * mm});
            skLineSegment(sketch, "E290", {"start": v(4.14, 9.83) * mm, "end": v(4.14, 9.7) * mm});
            skLineSegment(sketch, "E291", {"start": v(4.14, 9.7) * mm, "end": v(4.14, 9.57) * mm});
            skLineSegment(sketch, "E292", {"start": v(4.14, 9.57) * mm, "end": v(4.14, 9.44) * mm});
            skLineSegment(sketch, "E293", {"start": v(4.14, 9.44) * mm, "end": v(4.14, 9.31) * mm});
            skLineSegment(sketch, "E294", {"start": v(4.14, 9.31) * mm, "end": v(4.02, 9.31) * mm});
            skLineSegment(sketch, "E295", {"start": v(4.02, 9.31) * mm, "end": v(3.91, 9.31) * mm});
            skLineSegment(sketch, "E296", {"start": v(3.91, 9.31) * mm, "end": v(3.8, 9.31) * mm});
            skLineSegment(sketch, "E297", {"start": v(3.8, 9.31) * mm, "end": v(3.69, 9.31) * mm});
            skLineSegment(sketch, "E298", {"start": v(3.69, 9.31) * mm, "end": v(3.57, 9.31) * mm});
            skLineSegment(sketch, "E299", {"start": v(3.57, 9.31) * mm, "end": v(3.46, 9.31) * mm});
            skLineSegment(sketch, "E300", {"start": v(3.46, 9.31) * mm, "end": v(3.35, 9.31) * mm});
            skLineSegment(sketch, "E301", {"start": v(3.35, 9.31) * mm, "end": v(3.23, 9.31) * mm});
            skLineSegment(sketch, "E302", {"start": v(3.23, 9.31) * mm, "end": v(3.12, 9.31) * mm});
            skLineSegment(sketch, "E303", {"start": v(3.12, 9.31) * mm, "end": v(3, 9.31) * mm});
            skLineSegment(sketch, "E304", {"start": v(3, 9.31) * mm, "end": v(2.9, 9.31) * mm});
            skLineSegment(sketch, "E305", {"start": v(2.9, 9.31) * mm, "end": v(2.78, 9.31) * mm});
            skLineSegment(sketch, "E306", {"start": v(2.78, 9.31) * mm, "end": v(2.67, 9.31) * mm});
            skLineSegment(sketch, "E307", {"start": v(2.67, 9.31) * mm, "end": v(2.55, 9.31) * mm});
            skLineSegment(sketch, "E308", {"start": v(2.55, 9.31) * mm, "end": v(2.44, 9.31) * mm});
            skLineSegment(sketch, "E309", {"start": v(2.44, 9.31) * mm, "end": v(2.33, 9.31) * mm});
            skLineSegment(sketch, "E310", {"start": v(2.33, 9.31) * mm, "end": v(2.2, 9.3) * mm});
            skLineSegment(sketch, "E311", {"start": v(2.2, 9.3) * mm, "end": v(2.07, 9.28) * mm});
            skLineSegment(sketch, "E312", {"start": v(2.07, 9.28) * mm, "end": v(1.94, 9.25) * mm});
            skLineSegment(sketch, "E313", {"start": v(1.94, 9.25) * mm, "end": v(1.82, 9.2) * mm});
            skLineSegment(sketch, "E314", {"start": v(1.82, 9.2) * mm, "end": v(1.71, 9.15) * mm});
            skLineSegment(sketch, "E315", {"start": v(1.71, 9.15) * mm, "end": v(1.6, 9.09) * mm});
            skLineSegment(sketch, "E316", {"start": v(1.6, 9.09) * mm, "end": v(1.5, 9.02) * mm});
            skLineSegment(sketch, "E317", {"start": v(1.5, 9.02) * mm, "end": v(1.41, 8.93) * mm});
            skLineSegment(sketch, "E318", {"start": v(1.41, 8.93) * mm, "end": v(1.33, 8.84) * mm});
            skLineSegment(sketch, "E319", {"start": v(1.33, 8.84) * mm, "end": v(1.26, 8.74) * mm});
            skLineSegment(sketch, "E320", {"start": v(1.26, 8.74) * mm, "end": v(1.2, 8.63) * mm});
            skLineSegment(sketch, "E321", {"start": v(1.2, 8.63) * mm, "end": v(1.14, 8.52) * mm});
            skLineSegment(sketch, "E322", {"start": v(1.14, 8.52) * mm, "end": v(1.1, 8.4) * mm});
            skLineSegment(sketch, "E323", {"start": v(1.1, 8.4) * mm, "end": v(1.06, 8.28) * mm});
            skLineSegment(sketch, "E324", {"start": v(1.06, 8.28) * mm, "end": v(1.04, 8.15) * mm});
            skLineSegment(sketch, "E325", {"start": v(1.04, 8.15) * mm, "end": v(1.03, 8.02) * mm});
            skLineSegment(sketch, "E326", {"start": v(1.03, 8.02) * mm, "end": v(1.03, 7.9) * mm});
            skLineSegment(sketch, "E327", {"start": v(1.03, 7.9) * mm, "end": v(1.03, 7.8) * mm});
            skLineSegment(sketch, "E328", {"start": v(1.03, 7.8) * mm, "end": v(1.03, 7.68) * mm});
            skLineSegment(sketch, "E329", {"start": v(1.03, 7.68) * mm, "end": v(1.03, 7.56) * mm});
            skLineSegment(sketch, "E330", {"start": v(1.03, 7.56) * mm, "end": v(1.03, 7.45) * mm});
            skLineSegment(sketch, "E331", {"start": v(1.03, 7.45) * mm, "end": v(1.03, 7.34) * mm});
            skLineSegment(sketch, "E332", {"start": v(1.03, 7.34) * mm, "end": v(1.03, 7.23) * mm});
            skLineSegment(sketch, "E333", {"start": v(1.03, 7.23) * mm, "end": v(1.03, 7.11) * mm});
            skLineSegment(sketch, "E334", {"start": v(1.03, 7.11) * mm, "end": v(1.03, 7) * mm});
            skLineSegment(sketch, "E335", {"start": v(1.03, 7) * mm, "end": v(1.03, 6.89) * mm});
            skLineSegment(sketch, "E336", {"start": v(1.03, 6.89) * mm, "end": v(1.03, 6.77) * mm});
            skLineSegment(sketch, "E337", {"start": v(1.03, 6.77) * mm, "end": v(1.03, 6.66) * mm});
            skLineSegment(sketch, "E338", {"start": v(1.03, 6.66) * mm, "end": v(1.03, 6.55) * mm});
            skLineSegment(sketch, "E339", {"start": v(1.03, 6.55) * mm, "end": v(1.03, 6.43) * mm});
            skLineSegment(sketch, "E340", {"start": v(1.03, 6.43) * mm, "end": v(1.03, 6.32) * mm});
            skLineSegment(sketch, "E341", {"start": v(1.03, 6.32) * mm, "end": v(1.03, 6.2) * mm});
            skLineSegment(sketch, "E342", {"start": v(1.03, 6.2) * mm, "end": v(0.97, 6.2) * mm});
            skLineSegment(sketch, "E343", {"start": v(0.97, 6.2) * mm, "end": v(0.9, 6.2) * mm});
            skLineSegment(sketch, "E344", {"start": v(0.9, 6.2) * mm, "end": v(0.84, 6.2) * mm});
            skLineSegment(sketch, "E345", {"start": v(0.84, 6.2) * mm, "end": v(0.78, 6.2) * mm});
            skLineSegment(sketch, "E346", {"start": v(0.78, 6.2) * mm, "end": v(0.71, 6.2) * mm});
            skLineSegment(sketch, "E347", {"start": v(0.71, 6.2) * mm, "end": v(0.65, 6.2) * mm});
            skLineSegment(sketch, "E348", {"start": v(0.65, 6.2) * mm, "end": v(0.58, 6.2) * mm});
            skLineSegment(sketch, "E349", {"start": v(0.58, 6.2) * mm, "end": v(0.52, 6.2) * mm});
            skLineSegment(sketch, "E350", {"start": v(0.52, 6.2) * mm, "end": v(0.45, 6.2) * mm});
            skLineSegment(sketch, "E351", {"start": v(0.45, 6.2) * mm, "end": v(0.39, 6.2) * mm});
            skLineSegment(sketch, "E352", {"start": v(0.39, 6.2) * mm, "end": v(0.32, 6.2) * mm});
            skLineSegment(sketch, "E353", {"start": v(0.32, 6.2) * mm, "end": v(0.26, 6.2) * mm});
            skLineSegment(sketch, "E354", {"start": v(0.26, 6.2) * mm, "end": v(0.2, 6.2) * mm});
            skLineSegment(sketch, "E355", {"start": v(0.2, 6.2) * mm, "end": v(0.13, 6.2) * mm});
            skLineSegment(sketch, "E356", {"start": v(0.13, 6.2) * mm, "end": v(0.06, 6.2) * mm});
            skLineSegment(sketch, "E357", {"start": v(0.06, 6.2) * mm, "end": v(0, 6.2) * mm});
            skLineSegment(sketch, "E358", {"start": v(0, 6.2) * mm, "end": v(-0.06, 6.2) * mm});
            skLineSegment(sketch, "E359", {"start": v(-0.06, 6.2) * mm, "end": v(-0.13, 6.2) * mm});
            skLineSegment(sketch, "E360", {"start": v(-0.13, 6.2) * mm, "end": v(-0.2, 6.2) * mm});
            skLineSegment(sketch, "E361", {"start": v(-0.2, 6.2) * mm, "end": v(-0.26, 6.2) * mm});
            skLineSegment(sketch, "E362", {"start": v(-0.26, 6.2) * mm, "end": v(-0.32, 6.2) * mm});
            skLineSegment(sketch, "E363", {"start": v(-0.32, 6.2) * mm, "end": v(-0.39, 6.2) * mm});
            skLineSegment(sketch, "E364", {"start": v(-0.39, 6.2) * mm, "end": v(-0.45, 6.2) * mm});
            skLineSegment(sketch, "E365", {"start": v(-0.45, 6.2) * mm, "end": v(-0.52, 6.2) * mm});
            skLineSegment(sketch, "E366", {"start": v(-0.52, 6.2) * mm, "end": v(-0.58, 6.2) * mm});
            skLineSegment(sketch, "E367", {"start": v(-0.58, 6.2) * mm, "end": v(-0.65, 6.2) * mm});
            skLineSegment(sketch, "E368", {"start": v(-0.65, 6.2) * mm, "end": v(-0.71, 6.2) * mm});
            skLineSegment(sketch, "E369", {"start": v(-0.71, 6.2) * mm, "end": v(-0.78, 6.2) * mm});
            skLineSegment(sketch, "E370", {"start": v(-0.78, 6.2) * mm, "end": v(-0.84, 6.2) * mm});
            skLineSegment(sketch, "E371", {"start": v(-0.84, 6.2) * mm, "end": v(-0.9, 6.2) * mm});
            skLineSegment(sketch, "E372", {"start": v(-0.9, 6.2) * mm, "end": v(-0.97, 6.2) * mm});
            skLineSegment(sketch, "E373", {"start": v(-0.97, 6.2) * mm, "end": v(-1.03, 6.2) * mm});
            skLineSegment(sketch, "E374", {"start": v(-1.03, 6.2) * mm, "end": v(-1.03, 6.32) * mm});
            skLineSegment(sketch, "E375", {"start": v(-1.03, 6.32) * mm, "end": v(-1.03, 6.43) * mm});
            skLineSegment(sketch, "E376", {"start": v(-1.03, 6.43) * mm, "end": v(-1.03, 6.55) * mm});
            skLineSegment(sketch, "E377", {"start": v(-1.03, 6.55) * mm, "end": v(-1.03, 6.66) * mm});
            skLineSegment(sketch, "E378", {"start": v(-1.03, 6.66) * mm, "end": v(-1.03, 6.77) * mm});
            skLineSegment(sketch, "E379", {"start": v(-1.03, 6.77) * mm, "end": v(-1.03, 6.89) * mm});
            skLineSegment(sketch, "E380", {"start": v(-1.03, 6.89) * mm, "end": v(-1.03, 7) * mm});
            skLineSegment(sketch, "E381", {"start": v(-1.03, 7) * mm, "end": v(-1.03, 7.11) * mm});
            skLineSegment(sketch, "E382", {"start": v(-1.03, 7.11) * mm, "end": v(-1.03, 7.23) * mm});
            skLineSegment(sketch, "E383", {"start": v(-1.03, 7.23) * mm, "end": v(-1.03, 7.34) * mm});
            skLineSegment(sketch, "E384", {"start": v(-1.03, 7.34) * mm, "end": v(-1.03, 7.45) * mm});
            skLineSegment(sketch, "E385", {"start": v(-1.03, 7.45) * mm, "end": v(-1.03, 7.56) * mm});
            skLineSegment(sketch, "E386", {"start": v(-1.03, 7.56) * mm, "end": v(-1.03, 7.68) * mm});
            skLineSegment(sketch, "E387", {"start": v(-1.03, 7.68) * mm, "end": v(-1.03, 7.8) * mm});
            skLineSegment(sketch, "E388", {"start": v(-1.03, 7.8) * mm, "end": v(-1.03, 7.9) * mm});
            skLineSegment(sketch, "E389", {"start": v(-1.03, 7.9) * mm, "end": v(-1.03, 8.02) * mm});
            skLineSegment(sketch, "E390", {"start": v(-1.03, 8.02) * mm, "end": v(-1.04, 8.15) * mm});
            skLineSegment(sketch, "E391", {"start": v(-1.04, 8.15) * mm, "end": v(-1.06, 8.28) * mm});
            skLineSegment(sketch, "E392", {"start": v(-1.06, 8.28) * mm, "end": v(-1.1, 8.4) * mm});
            skLineSegment(sketch, "E393", {"start": v(-1.1, 8.4) * mm, "end": v(-1.14, 8.52) * mm});
            skLineSegment(sketch, "E394", {"start": v(-1.14, 8.52) * mm, "end": v(-1.2, 8.63) * mm});
            skLineSegment(sketch, "E395", {"start": v(-1.2, 8.63) * mm, "end": v(-1.26, 8.74) * mm});
            skLineSegment(sketch, "E396", {"start": v(-1.26, 8.74) * mm, "end": v(-1.33, 8.84) * mm});
            skLineSegment(sketch, "E397", {"start": v(-1.33, 8.84) * mm, "end": v(-1.41, 8.93) * mm});
            skLineSegment(sketch, "E398", {"start": v(-1.41, 8.93) * mm, "end": v(-1.5, 9.02) * mm});
            skLineSegment(sketch, "E399", {"start": v(-1.5, 9.02) * mm, "end": v(-1.6, 9.09) * mm});
            skLineSegment(sketch, "E400", {"start": v(-1.6, 9.09) * mm, "end": v(-1.71, 9.15) * mm});
            skLineSegment(sketch, "E401", {"start": v(-1.71, 9.15) * mm, "end": v(-1.82, 9.2) * mm});
            skLineSegment(sketch, "E402", {"start": v(-1.82, 9.2) * mm, "end": v(-1.94, 9.25) * mm});
            skLineSegment(sketch, "E403", {"start": v(-1.94, 9.25) * mm, "end": v(-2.07, 9.28) * mm});
            skLineSegment(sketch, "E404", {"start": v(-2.07, 9.28) * mm, "end": v(-2.2, 9.3) * mm});
            skLineSegment(sketch, "E405", {"start": v(-2.2, 9.3) * mm, "end": v(-2.33, 9.31) * mm});
            skLineSegment(sketch, "E406", {"start": v(-2.33, 9.31) * mm, "end": v(-2.44, 9.31) * mm});
            skLineSegment(sketch, "E407", {"start": v(-2.44, 9.31) * mm, "end": v(-2.55, 9.31) * mm});
            skLineSegment(sketch, "E408", {"start": v(-2.55, 9.31) * mm, "end": v(-2.67, 9.31) * mm});
            skLineSegment(sketch, "E409", {"start": v(-2.67, 9.31) * mm, "end": v(-2.78, 9.31) * mm});
            skLineSegment(sketch, "E410", {"start": v(-2.78, 9.31) * mm, "end": v(-2.9, 9.31) * mm});
            skLineSegment(sketch, "E411", {"start": v(-2.9, 9.31) * mm, "end": v(-3, 9.31) * mm});
            skLineSegment(sketch, "E412", {"start": v(-3, 9.31) * mm, "end": v(-3.12, 9.31) * mm});
            skLineSegment(sketch, "E413", {"start": v(-3.12, 9.31) * mm, "end": v(-3.23, 9.31) * mm});
            skLineSegment(sketch, "E414", {"start": v(-3.23, 9.31) * mm, "end": v(-3.35, 9.31) * mm});
            skLineSegment(sketch, "E415", {"start": v(-3.35, 9.31) * mm, "end": v(-3.46, 9.31) * mm});
            skLineSegment(sketch, "E416", {"start": v(-3.46, 9.31) * mm, "end": v(-3.57, 9.31) * mm});
            skLineSegment(sketch, "E417", {"start": v(-3.57, 9.31) * mm, "end": v(-3.69, 9.31) * mm});
            skLineSegment(sketch, "E418", {"start": v(-3.69, 9.31) * mm, "end": v(-3.8, 9.31) * mm});
            skLineSegment(sketch, "E419", {"start": v(-3.8, 9.31) * mm, "end": v(-3.91, 9.31) * mm});
            skLineSegment(sketch, "E420", {"start": v(-3.91, 9.31) * mm, "end": v(-4.02, 9.31) * mm});
            skLineSegment(sketch, "E421", {"start": v(-4.02, 9.31) * mm, "end": v(-4.14, 9.31) * mm});
            skLineSegment(sketch, "E422", {"start": v(-4.14, 9.31) * mm, "end": v(-4.14, 9.44) * mm});
            skLineSegment(sketch, "E423", {"start": v(-4.14, 9.44) * mm, "end": v(-4.14, 9.57) * mm});
            skLineSegment(sketch, "E424", {"start": v(-4.14, 9.57) * mm, "end": v(-4.14, 9.7) * mm});
            skLineSegment(sketch, "E425", {"start": v(-4.14, 9.7) * mm, "end": v(-4.14, 9.83) * mm});
            skLineSegment(sketch, "E426", {"start": v(-4.14, 9.83) * mm, "end": v(-4.14, 9.96) * mm});
            skLineSegment(sketch, "E427", {"start": v(-4.14, 9.96) * mm, "end": v(-4.14, 10.09) * mm});
            skLineSegment(sketch, "E428", {"start": v(-4.14, 10.09) * mm, "end": v(-4.14, 10.22) * mm});
            skLineSegment(sketch, "E429", {"start": v(-4.14, 10.22) * mm, "end": v(-4.14, 10.34) * mm});
            skLineSegment(sketch, "E430", {"start": v(-4.14, 10.34) * mm, "end": v(-4.14, 10.47) * mm});
            skLineSegment(sketch, "E431", {"start": v(-4.14, 10.47) * mm, "end": v(-4.14, 10.6) * mm});
            skLineSegment(sketch, "E432", {"start": v(-4.14, 10.6) * mm, "end": v(-4.14, 10.73) * mm});
            skLineSegment(sketch, "E433", {"start": v(-4.14, 10.73) * mm, "end": v(-4.14, 10.86) * mm});
            skLineSegment(sketch, "E434", {"start": v(-4.14, 10.86) * mm, "end": v(-4.14, 11) * mm});
            skLineSegment(sketch, "E435", {"start": v(-4.14, 11) * mm, "end": v(-4.14, 11.12) * mm});
            skLineSegment(sketch, "E436", {"start": v(-4.14, 11.12) * mm, "end": v(-4.14, 11.25) * mm});
            skLineSegment(sketch, "E437", {"start": v(-4.14, 11.25) * mm, "end": v(-4.14, 11.38) * mm});
            skLineSegment(sketch, "E438", {"start": v(-4.14, 11.38) * mm, "end": v(-4.14, 11.6) * mm});
            skLineSegment(sketch, "E439", {"start": v(-4.14, 11.6) * mm, "end": v(-4.14, 11.83) * mm});
            skLineSegment(sketch, "E440", {"start": v(-4.14, 11.83) * mm, "end": v(-4.14, 12.06) * mm});
            skLineSegment(sketch, "E441", {"start": v(-4.14, 12.06) * mm, "end": v(-4.14, 12.28) * mm});
            skLineSegment(sketch, "E442", {"start": v(-4.14, 12.28) * mm, "end": v(-4.14, 12.51) * mm});
            skLineSegment(sketch, "E443", {"start": v(-4.14, 12.51) * mm, "end": v(-4.14, 12.74) * mm});
            skLineSegment(sketch, "E444", {"start": v(-4.14, 12.74) * mm, "end": v(-4.14, 12.96) * mm});
            skLineSegment(sketch, "E445", {"start": v(-4.14, 12.96) * mm, "end": v(-4.14, 13.19) * mm});
            skLineSegment(sketch, "E446", {"start": v(-4.14, 13.19) * mm, "end": v(-4.14, 13.42) * mm});
            skLineSegment(sketch, "E447", {"start": v(-4.14, 13.42) * mm, "end": v(-4.14, 13.64) * mm});
            skLineSegment(sketch, "E448", {"start": v(-4.14, 13.64) * mm, "end": v(-4.14, 13.87) * mm});
            skLineSegment(sketch, "E449", {"start": v(-4.14, 13.87) * mm, "end": v(-4.14, 14.1) * mm});
            skLineSegment(sketch, "E450", {"start": v(-4.14, 14.1) * mm, "end": v(-4.14, 14.32) * mm});
            skLineSegment(sketch, "E451", {"start": v(-4.14, 14.32) * mm, "end": v(-4.14, 14.55) * mm});
            skLineSegment(sketch, "E452", {"start": v(-4.14, 14.55) * mm, "end": v(-4.14, 14.77) * mm});
            skLineSegment(sketch, "E453", {"start": v(-4.14, 14.77) * mm, "end": v(-4.14, 15) * mm});
            skLineSegment(sketch, "E454", {"start": v(-4.14, 15) * mm, "end": v(-4.27, 14.95) * mm});
            skLineSegment(sketch, "E455", {"start": v(-4.27, 14.95) * mm, "end": v(-4.4, 14.9) * mm});
            skLineSegment(sketch, "E456", {"start": v(-4.4, 14.9) * mm, "end": v(-4.53, 14.84) * mm});
            skLineSegment(sketch, "E457", {"start": v(-4.53, 14.84) * mm, "end": v(-4.66, 14.8) * mm});
            skLineSegment(sketch, "E458", {"start": v(-4.66, 14.8) * mm, "end": v(-4.78, 14.74) * mm});
            skLineSegment(sketch, "E459", {"start": v(-4.78, 14.74) * mm, "end": v(-4.91, 14.69) * mm});
            skLineSegment(sketch, "E460", {"start": v(-4.91, 14.69) * mm, "end": v(-5.04, 14.64) * mm});
            skLineSegment(sketch, "E461", {"start": v(-5.04, 14.64) * mm, "end": v(-5.17, 14.59) * mm});
            skLineSegment(sketch, "E462", {"start": v(-5.17, 14.59) * mm, "end": v(-5.3, 14.53) * mm});
            skLineSegment(sketch, "E463", {"start": v(-5.3, 14.53) * mm, "end": v(-5.43, 14.48) * mm});
            skLineSegment(sketch, "E464", {"start": v(-5.43, 14.48) * mm, "end": v(-5.56, 14.43) * mm});
            skLineSegment(sketch, "E465", {"start": v(-5.56, 14.43) * mm, "end": v(-5.69, 14.38) * mm});
            skLineSegment(sketch, "E466", {"start": v(-5.69, 14.38) * mm, "end": v(-5.82, 14.33) * mm});
            skLineSegment(sketch, "E467", {"start": v(-5.82, 14.33) * mm, "end": v(-5.95, 14.28) * mm});
            skLineSegment(sketch, "E468", {"start": v(-5.95, 14.28) * mm, "end": v(-6.08, 14.22) * mm});
            skLineSegment(sketch, "E469", {"start": v(-6.08, 14.22) * mm, "end": v(-6.2, 14.17) * mm});
            skLineSegment(sketch, "E470", {"start": v(-6.2, 14.17) * mm, "end": v(-6.24, 14.16) * mm});
            skLineSegment(sketch, "E471", {"start": v(-6.24, 14.16) * mm, "end": v(-6.27, 14.15) * mm});
            skLineSegment(sketch, "E472", {"start": v(-6.27, 14.15) * mm, "end": v(-6.3, 14.13) * mm});
            skLineSegment(sketch, "E473", {"start": v(-6.3, 14.13) * mm, "end": v(-6.34, 14.12) * mm});
            skLineSegment(sketch, "E474", {"start": v(-6.34, 14.12) * mm, "end": v(-6.37, 14.1) * mm});
            skLineSegment(sketch, "E475", {"start": v(-6.37, 14.1) * mm, "end": v(-6.4, 14.1) * mm});
            skLineSegment(sketch, "E476", {"start": v(-6.4, 14.1) * mm, "end": v(-6.43, 14.08) * mm});
            skLineSegment(sketch, "E477", {"start": v(-6.43, 14.08) * mm, "end": v(-6.47, 14.07) * mm});
            skLineSegment(sketch, "E478", {"start": v(-6.47, 14.07) * mm, "end": v(-6.5, 14.06) * mm});
            skLineSegment(sketch, "E479", {"start": v(-6.5, 14.06) * mm, "end": v(-6.53, 14.04) * mm});
            skLineSegment(sketch, "E480", {"start": v(-6.53, 14.04) * mm, "end": v(-6.56, 14.03) * mm});
            skLineSegment(sketch, "E481", {"start": v(-6.56, 14.03) * mm, "end": v(-6.6, 14.02) * mm});
            skLineSegment(sketch, "E482", {"start": v(-6.6, 14.02) * mm, "end": v(-6.63, 14) * mm});
            skLineSegment(sketch, "E483", {"start": v(-6.63, 14) * mm, "end": v(-6.66, 14) * mm});
            skLineSegment(sketch, "E484", {"start": v(-6.66, 14) * mm, "end": v(-6.7, 13.98) * mm});
            skLineSegment(sketch, "E485", {"start": v(-6.7, 13.98) * mm, "end": v(-6.72, 13.97) * mm});
            skLineSegment(sketch, "E486", {"start": v(-6.72, 13.97) * mm, "end": v(-6.86, 13.65) * mm});
            skLineSegment(sketch, "E487", {"start": v(-6.86, 13.65) * mm, "end": v(-7, 13.33) * mm});
            skLineSegment(sketch, "E488", {"start": v(-7, 13.33) * mm, "end": v(-7.12, 13) * mm});
            skLineSegment(sketch, "E489", {"start": v(-7.12, 13) * mm, "end": v(-7.26, 12.69) * mm});
            skLineSegment(sketch, "E490", {"start": v(-7.26, 12.69) * mm, "end": v(-7.39, 12.37) * mm});
            skLineSegment(sketch, "E491", {"start": v(-7.39, 12.37) * mm, "end": v(-7.52, 12.05) * mm});
            skLineSegment(sketch, "E492", {"start": v(-7.52, 12.05) * mm, "end": v(-7.66, 11.73) * mm});
            skLineSegment(sketch, "E493", {"start": v(-7.66, 11.73) * mm, "end": v(-7.79, 11.4) * mm});
            skLineSegment(sketch, "E494", {"start": v(-7.79, 11.4) * mm, "end": v(-7.92, 11.1) * mm});
            skLineSegment(sketch, "E495", {"start": v(-7.92, 11.1) * mm, "end": v(-8.06, 10.77) * mm});
            skLineSegment(sketch, "E496", {"start": v(-8.06, 10.77) * mm, "end": v(-8.19, 10.45) * mm});
            skLineSegment(sketch, "E497", {"start": v(-8.19, 10.45) * mm, "end": v(-8.32, 10.13) * mm});
            skLineSegment(sketch, "E498", {"start": v(-8.32, 10.13) * mm, "end": v(-8.45, 9.81) * mm});
            skLineSegment(sketch, "E499", {"start": v(-8.45, 9.81) * mm, "end": v(-8.59, 9.5) * mm});
            skLineSegment(sketch, "E500", {"start": v(-8.59, 9.5) * mm, "end": v(-8.72, 9.17) * mm});
            skLineSegment(sketch, "E501", {"start": v(-8.72, 9.17) * mm, "end": v(-8.85, 8.85) * mm});
            skLineSegment(sketch, "E502", {"start": v(-8.85, 8.85) * mm, "end": v(-9.17, 8.72) * mm});
            skLineSegment(sketch, "E503", {"start": v(-9.17, 8.72) * mm, "end": v(-9.5, 8.59) * mm});
            skLineSegment(sketch, "E504", {"start": v(-9.5, 8.59) * mm, "end": v(-9.81, 8.45) * mm});
            skLineSegment(sketch, "E505", {"start": v(-9.81, 8.45) * mm, "end": v(-10.13, 8.32) * mm});
            skLineSegment(sketch, "E506", {"start": v(-10.13, 8.32) * mm, "end": v(-10.45, 8.19) * mm});
            skLineSegment(sketch, "E507", {"start": v(-10.45, 8.19) * mm, "end": v(-10.77, 8.06) * mm});
            skLineSegment(sketch, "E508", {"start": v(-10.77, 8.06) * mm, "end": v(-11.1, 7.92) * mm});
            skLineSegment(sketch, "E509", {"start": v(-11.1, 7.92) * mm, "end": v(-11.4, 7.79) * mm});
            skLineSegment(sketch, "E510", {"start": v(-11.4, 7.79) * mm, "end": v(-11.73, 7.66) * mm});
            skLineSegment(sketch, "E511", {"start": v(-11.73, 7.66) * mm, "end": v(-12.05, 7.52) * mm});
            skLineSegment(sketch, "E512", {"start": v(-12.05, 7.52) * mm, "end": v(-12.37, 7.39) * mm});
            skLineSegment(sketch, "E513", {"start": v(-12.37, 7.39) * mm, "end": v(-12.69, 7.26) * mm});
            skLineSegment(sketch, "E514", {"start": v(-12.69, 7.26) * mm, "end": v(-13, 7.12) * mm});
            skLineSegment(sketch, "E515", {"start": v(-13, 7.12) * mm, "end": v(-13.33, 7) * mm});
            skLineSegment(sketch, "E516", {"start": v(-13.33, 7) * mm, "end": v(-13.65, 6.86) * mm});
            skLineSegment(sketch, "E517", {"start": v(-13.65, 6.86) * mm, "end": v(-13.97, 6.72) * mm});
            skLineSegment(sketch, "E518", {"start": v(-13.97, 6.72) * mm, "end": v(-13.98, 6.7) * mm});
            skLineSegment(sketch, "E519", {"start": v(-13.98, 6.7) * mm, "end": v(-14, 6.66) * mm});
            skLineSegment(sketch, "E520", {"start": v(-14, 6.66) * mm, "end": v(-14, 6.63) * mm});
            skLineSegment(sketch, "E521", {"start": v(-14, 6.63) * mm, "end": v(-14.02, 6.6) * mm});
            skLineSegment(sketch, "E522", {"start": v(-14.02, 6.6) * mm, "end": v(-14.03, 6.56) * mm});
            skLineSegment(sketch, "E523", {"start": v(-14.03, 6.56) * mm, "end": v(-14.04, 6.53) * mm});
            skLineSegment(sketch, "E524", {"start": v(-14.04, 6.53) * mm, "end": v(-14.06, 6.5) * mm});
            skLineSegment(sketch, "E525", {"start": v(-14.06, 6.5) * mm, "end": v(-14.07, 6.47) * mm});
            skLineSegment(sketch, "E526", {"start": v(-14.07, 6.47) * mm, "end": v(-14.08, 6.43) * mm});
            skLineSegment(sketch, "E527", {"start": v(-14.08, 6.43) * mm, "end": v(-14.1, 6.4) * mm});
            skLineSegment(sketch, "E528", {"start": v(-14.1, 6.4) * mm, "end": v(-14.1, 6.37) * mm});
            skLineSegment(sketch, "E529", {"start": v(-14.1, 6.37) * mm, "end": v(-14.12, 6.34) * mm});
            skLineSegment(sketch, "E530", {"start": v(-14.12, 6.34) * mm, "end": v(-14.13, 6.3) * mm});
            skLineSegment(sketch, "E531", {"start": v(-14.13, 6.3) * mm, "end": v(-14.15, 6.27) * mm});
            skLineSegment(sketch, "E532", {"start": v(-14.15, 6.27) * mm, "end": v(-14.16, 6.24) * mm});
            skLineSegment(sketch, "E533", {"start": v(-14.16, 6.24) * mm, "end": v(-14.17, 6.2) * mm});
            skLineSegment(sketch, "E534", {"start": v(-14.17, 6.2) * mm, "end": v(-14.22, 6.08) * mm});
            skLineSegment(sketch, "E535", {"start": v(-14.22, 6.08) * mm, "end": v(-14.28, 5.95) * mm});
            skLineSegment(sketch, "E536", {"start": v(-14.28, 5.95) * mm, "end": v(-14.33, 5.82) * mm});
            skLineSegment(sketch, "E537", {"start": v(-14.33, 5.82) * mm, "end": v(-14.38, 5.69) * mm});
            skLineSegment(sketch, "E538", {"start": v(-14.38, 5.69) * mm, "end": v(-14.43, 5.56) * mm});
            skLineSegment(sketch, "E539", {"start": v(-14.43, 5.56) * mm, "end": v(-14.48, 5.43) * mm});
            skLineSegment(sketch, "E540", {"start": v(-14.48, 5.43) * mm, "end": v(-14.53, 5.3) * mm});
            skLineSegment(sketch, "E541", {"start": v(-14.53, 5.3) * mm, "end": v(-14.59, 5.17) * mm});
            skLineSegment(sketch, "E542", {"start": v(-14.59, 5.17) * mm, "end": v(-14.64, 5.04) * mm});
            skLineSegment(sketch, "E543", {"start": v(-14.64, 5.04) * mm, "end": v(-14.69, 4.91) * mm});
            skLineSegment(sketch, "E544", {"start": v(-14.69, 4.91) * mm, "end": v(-14.74, 4.78) * mm});
            skLineSegment(sketch, "E545", {"start": v(-14.74, 4.78) * mm, "end": v(-14.8, 4.66) * mm});
            skLineSegment(sketch, "E546", {"start": v(-14.8, 4.66) * mm, "end": v(-14.84, 4.53) * mm});
            skLineSegment(sketch, "E547", {"start": v(-14.84, 4.53) * mm, "end": v(-14.9, 4.4) * mm});
            skLineSegment(sketch, "E548", {"start": v(-14.9, 4.4) * mm, "end": v(-14.95, 4.27) * mm});
            skLineSegment(sketch, "E549", {"start": v(-14.95, 4.27) * mm, "end": v(-15, 4.14) * mm});
            skLineSegment(sketch, "E550", {"start": v(-15, 4.14) * mm, "end": v(-14.77, 4.14) * mm});
            skLineSegment(sketch, "E551", {"start": v(-14.77, 4.14) * mm, "end": v(-14.55, 4.14) * mm});
            skLineSegment(sketch, "E552", {"start": v(-14.55, 4.14) * mm, "end": v(-14.32, 4.14) * mm});
            skLineSegment(sketch, "E553", {"start": v(-14.32, 4.14) * mm, "end": v(-14.1, 4.14) * mm});
            skLineSegment(sketch, "E554", {"start": v(-14.1, 4.14) * mm, "end": v(-13.87, 4.14) * mm});
            skLineSegment(sketch, "E555", {"start": v(-13.87, 4.14) * mm, "end": v(-13.64, 4.14) * mm});
            skLineSegment(sketch, "E556", {"start": v(-13.64, 4.14) * mm, "end": v(-13.42, 4.14) * mm});
            skLineSegment(sketch, "E557", {"start": v(-13.42, 4.14) * mm, "end": v(-13.19, 4.14) * mm});
            skLineSegment(sketch, "E558", {"start": v(-13.19, 4.14) * mm, "end": v(-12.96, 4.14) * mm});
            skLineSegment(sketch, "E559", {"start": v(-12.96, 4.14) * mm, "end": v(-12.74, 4.14) * mm});
            skLineSegment(sketch, "E560", {"start": v(-12.74, 4.14) * mm, "end": v(-12.51, 4.14) * mm});
            skLineSegment(sketch, "E561", {"start": v(-12.51, 4.14) * mm, "end": v(-12.28, 4.14) * mm});
            skLineSegment(sketch, "E562", {"start": v(-12.28, 4.14) * mm, "end": v(-12.06, 4.14) * mm});
            skLineSegment(sketch, "E563", {"start": v(-12.06, 4.14) * mm, "end": v(-11.83, 4.14) * mm});
            skLineSegment(sketch, "E564", {"start": v(-11.83, 4.14) * mm, "end": v(-11.6, 4.14) * mm});
            skLineSegment(sketch, "E565", {"start": v(-11.6, 4.14) * mm, "end": v(-11.38, 4.14) * mm});
            skLineSegment(sketch, "E566", {"start": v(-11.38, 4.14) * mm, "end": v(-11.25, 4.14) * mm});
            skLineSegment(sketch, "E567", {"start": v(-11.25, 4.14) * mm, "end": v(-11.12, 4.14) * mm});
            skLineSegment(sketch, "E568", {"start": v(-11.12, 4.14) * mm, "end": v(-11, 4.14) * mm});
            skLineSegment(sketch, "E569", {"start": v(-11, 4.14) * mm, "end": v(-10.86, 4.14) * mm});
            skLineSegment(sketch, "E570", {"start": v(-10.86, 4.14) * mm, "end": v(-10.73, 4.14) * mm});
            skLineSegment(sketch, "E571", {"start": v(-10.73, 4.14) * mm, "end": v(-10.6, 4.14) * mm});
            skLineSegment(sketch, "E572", {"start": v(-10.6, 4.14) * mm, "end": v(-10.47, 4.14) * mm});
            skLineSegment(sketch, "E573", {"start": v(-10.47, 4.14) * mm, "end": v(-10.34, 4.14) * mm});
            skLineSegment(sketch, "E574", {"start": v(-10.34, 4.14) * mm, "end": v(-10.22, 4.14) * mm});
            skLineSegment(sketch, "E575", {"start": v(-10.22, 4.14) * mm, "end": v(-10.09, 4.14) * mm});
            skLineSegment(sketch, "E576", {"start": v(-10.09, 4.14) * mm, "end": v(-9.96, 4.14) * mm});
            skLineSegment(sketch, "E577", {"start": v(-9.96, 4.14) * mm, "end": v(-9.83, 4.14) * mm});
            skLineSegment(sketch, "E578", {"start": v(-9.83, 4.14) * mm, "end": v(-9.7, 4.14) * mm});
            skLineSegment(sketch, "E579", {"start": v(-9.7, 4.14) * mm, "end": v(-9.57, 4.14) * mm});
            skLineSegment(sketch, "E580", {"start": v(-9.57, 4.14) * mm, "end": v(-9.44, 4.14) * mm});
            skLineSegment(sketch, "E581", {"start": v(-9.44, 4.14) * mm, "end": v(-9.31, 4.14) * mm});
            skLineSegment(sketch, "E582", {"start": v(-9.31, 4.14) * mm, "end": v(-9.31, 4.02) * mm});
            skLineSegment(sketch, "E583", {"start": v(-9.31, 4.02) * mm, "end": v(-9.31, 3.91) * mm});
            skLineSegment(sketch, "E584", {"start": v(-9.31, 3.91) * mm, "end": v(-9.31, 3.8) * mm});
            skLineSegment(sketch, "E585", {"start": v(-9.31, 3.8) * mm, "end": v(-9.31, 3.69) * mm});
            skLineSegment(sketch, "E586", {"start": v(-9.31, 3.69) * mm, "end": v(-9.31, 3.57) * mm});
            skLineSegment(sketch, "E587", {"start": v(-9.31, 3.57) * mm, "end": v(-9.31, 3.46) * mm});
            skLineSegment(sketch, "E588", {"start": v(-9.31, 3.46) * mm, "end": v(-9.31, 3.35) * mm});
            skLineSegment(sketch, "E589", {"start": v(-9.31, 3.35) * mm, "end": v(-9.31, 3.23) * mm});
            skLineSegment(sketch, "E590", {"start": v(-9.31, 3.23) * mm, "end": v(-9.31, 3.12) * mm});
            skLineSegment(sketch, "E591", {"start": v(-9.31, 3.12) * mm, "end": v(-9.31, 3) * mm});
            skLineSegment(sketch, "E592", {"start": v(-9.31, 3) * mm, "end": v(-9.31, 2.9) * mm});
            skLineSegment(sketch, "E593", {"start": v(-9.31, 2.9) * mm, "end": v(-9.31, 2.78) * mm});
            skLineSegment(sketch, "E594", {"start": v(-9.31, 2.78) * mm, "end": v(-9.31, 2.67) * mm});
            skLineSegment(sketch, "E595", {"start": v(-9.31, 2.67) * mm, "end": v(-9.31, 2.55) * mm});
            skLineSegment(sketch, "E596", {"start": v(-9.31, 2.55) * mm, "end": v(-9.31, 2.44) * mm});
            skLineSegment(sketch, "E597", {"start": v(-9.31, 2.44) * mm, "end": v(-9.31, 2.33) * mm});
            skLineSegment(sketch, "E598", {"start": v(-9.31, 2.33) * mm, "end": v(-9.3, 2.2) * mm});
            skLineSegment(sketch, "E599", {"start": v(-9.3, 2.2) * mm, "end": v(-9.28, 2.07) * mm});
            skLineSegment(sketch, "E600", {"start": v(-9.28, 2.07) * mm, "end": v(-9.25, 1.94) * mm});
            skLineSegment(sketch, "E601", {"start": v(-9.25, 1.94) * mm, "end": v(-9.2, 1.82) * mm});
            skLineSegment(sketch, "E602", {"start": v(-9.2, 1.82) * mm, "end": v(-9.15, 1.71) * mm});
            skLineSegment(sketch, "E603", {"start": v(-9.15, 1.71) * mm, "end": v(-9.09, 1.6) * mm});
            skLineSegment(sketch, "E604", {"start": v(-9.09, 1.6) * mm, "end": v(-9.02, 1.5) * mm});
            skLineSegment(sketch, "E605", {"start": v(-9.02, 1.5) * mm, "end": v(-8.93, 1.41) * mm});
            skLineSegment(sketch, "E606", {"start": v(-8.93, 1.41) * mm, "end": v(-8.84, 1.33) * mm});
            skLineSegment(sketch, "E607", {"start": v(-8.84, 1.33) * mm, "end": v(-8.74, 1.26) * mm});
            skLineSegment(sketch, "E608", {"start": v(-8.74, 1.26) * mm, "end": v(-8.63, 1.2) * mm});
            skLineSegment(sketch, "E609", {"start": v(-8.63, 1.2) * mm, "end": v(-8.52, 1.14) * mm});
            skLineSegment(sketch, "E610", {"start": v(-8.52, 1.14) * mm, "end": v(-8.4, 1.1) * mm});
            skLineSegment(sketch, "E611", {"start": v(-8.4, 1.1) * mm, "end": v(-8.28, 1.06) * mm});
            skLineSegment(sketch, "E612", {"start": v(-8.28, 1.06) * mm, "end": v(-8.15, 1.04) * mm});
            skLineSegment(sketch, "E613", {"start": v(-8.15, 1.04) * mm, "end": v(-8.02, 1.03) * mm});
            skLineSegment(sketch, "E614", {"start": v(-8.02, 1.03) * mm, "end": v(-7.9, 1.03) * mm});
            skLineSegment(sketch, "E615", {"start": v(-7.9, 1.03) * mm, "end": v(-7.8, 1.03) * mm});
            skLineSegment(sketch, "E616", {"start": v(-7.8, 1.03) * mm, "end": v(-7.68, 1.03) * mm});
            skLineSegment(sketch, "E617", {"start": v(-7.68, 1.03) * mm, "end": v(-7.56, 1.03) * mm});
            skLineSegment(sketch, "E618", {"start": v(-7.56, 1.03) * mm, "end": v(-7.45, 1.03) * mm});
            skLineSegment(sketch, "E619", {"start": v(-7.45, 1.03) * mm, "end": v(-7.34, 1.03) * mm});
            skLineSegment(sketch, "E620", {"start": v(-7.34, 1.03) * mm, "end": v(-7.23, 1.03) * mm});
            skLineSegment(sketch, "E621", {"start": v(-7.23, 1.03) * mm, "end": v(-7.11, 1.03) * mm});
            skLineSegment(sketch, "E622", {"start": v(-7.11, 1.03) * mm, "end": v(-7, 1.03) * mm});
            skLineSegment(sketch, "E623", {"start": v(-7, 1.03) * mm, "end": v(-6.89, 1.03) * mm});
            skLineSegment(sketch, "E624", {"start": v(-6.89, 1.03) * mm, "end": v(-6.77, 1.03) * mm});
            skLineSegment(sketch, "E625", {"start": v(-6.77, 1.03) * mm, "end": v(-6.66, 1.03) * mm});
            skLineSegment(sketch, "E626", {"start": v(-6.66, 1.03) * mm, "end": v(-6.55, 1.03) * mm});
            skLineSegment(sketch, "E627", {"start": v(-6.55, 1.03) * mm, "end": v(-6.43, 1.03) * mm});
            skLineSegment(sketch, "E628", {"start": v(-6.43, 1.03) * mm, "end": v(-6.32, 1.03) * mm});
            skLineSegment(sketch, "E629", {"start": v(-6.32, 1.03) * mm, "end": v(-6.2, 1.03) * mm});
            skLineSegment(sketch, "E630", {"start": v(-6.2, 1.03) * mm, "end": v(-6.2, 0.97) * mm});
            skLineSegment(sketch, "E631", {"start": v(-6.2, 0.97) * mm, "end": v(-6.2, 0.9) * mm});
            skLineSegment(sketch, "E632", {"start": v(-6.2, 0.9) * mm, "end": v(-6.2, 0.84) * mm});
            skLineSegment(sketch, "E633", {"start": v(-6.2, 0.84) * mm, "end": v(-6.2, 0.78) * mm});
            skLineSegment(sketch, "E634", {"start": v(-6.2, 0.78) * mm, "end": v(-6.2, 0.71) * mm});
            skLineSegment(sketch, "E635", {"start": v(-6.2, 0.71) * mm, "end": v(-6.2, 0.65) * mm});
            skLineSegment(sketch, "E636", {"start": v(-6.2, 0.65) * mm, "end": v(-6.2, 0.58) * mm});
            skLineSegment(sketch, "E637", {"start": v(-6.2, 0.58) * mm, "end": v(-6.2, 0.52) * mm});
            skLineSegment(sketch, "E638", {"start": v(-6.2, 0.52) * mm, "end": v(-6.2, 0.45) * mm});
            skLineSegment(sketch, "E639", {"start": v(-6.2, 0.45) * mm, "end": v(-6.2, 0.39) * mm});
            skLineSegment(sketch, "E640", {"start": v(-6.2, 0.39) * mm, "end": v(-6.2, 0.32) * mm});
            skLineSegment(sketch, "E641", {"start": v(-6.2, 0.32) * mm, "end": v(-6.2, 0.26) * mm});
            skLineSegment(sketch, "E642", {"start": v(-6.2, 0.26) * mm, "end": v(-6.2, 0.2) * mm});
            skLineSegment(sketch, "E643", {"start": v(-6.2, 0.2) * mm, "end": v(-6.2, 0.13) * mm});
            skLineSegment(sketch, "E644", {"start": v(-6.2, 0.13) * mm, "end": v(-6.2, 0.06) * mm});
            skLineSegment(sketch, "E645", {"start": v(-6.2, 0.06) * mm, "end": v(-6.2, 0) * mm});
            skLineSegment(sketch, "E646", {"start": v(-6.2, 0) * mm, "end": v(-6.2, -0.06) * mm});
            skLineSegment(sketch, "E647", {"start": v(-6.2, -0.06) * mm, "end": v(-6.2, -0.13) * mm});
            skLineSegment(sketch, "E648", {"start": v(-6.2, -0.13) * mm, "end": v(-6.2, -0.2) * mm});
            skLineSegment(sketch, "E649", {"start": v(-6.2, -0.2) * mm, "end": v(-6.2, -0.26) * mm});
            skLineSegment(sketch, "E650", {"start": v(-6.2, -0.26) * mm, "end": v(-6.2, -0.32) * mm});
            skLineSegment(sketch, "E651", {"start": v(-6.2, -0.32) * mm, "end": v(-6.2, -0.39) * mm});
            skLineSegment(sketch, "E652", {"start": v(-6.2, -0.39) * mm, "end": v(-6.2, -0.45) * mm});
            skLineSegment(sketch, "E653", {"start": v(-6.2, -0.45) * mm, "end": v(-6.2, -0.52) * mm});
            skLineSegment(sketch, "E654", {"start": v(-6.2, -0.52) * mm, "end": v(-6.2, -0.58) * mm});
            skLineSegment(sketch, "E655", {"start": v(-6.2, -0.58) * mm, "end": v(-6.2, -0.65) * mm});
            skLineSegment(sketch, "E656", {"start": v(-6.2, -0.65) * mm, "end": v(-6.2, -0.71) * mm});
            skLineSegment(sketch, "E657", {"start": v(-6.2, -0.71) * mm, "end": v(-6.2, -0.78) * mm});
            skLineSegment(sketch, "E658", {"start": v(-6.2, -0.78) * mm, "end": v(-6.2, -0.84) * mm});
            skLineSegment(sketch, "E659", {"start": v(-6.2, -0.84) * mm, "end": v(-6.2, -0.9) * mm});
            skLineSegment(sketch, "E660", {"start": v(-6.2, -0.9) * mm, "end": v(-6.2, -0.97) * mm});
            skLineSegment(sketch, "E661", {"start": v(-6.2, -0.97) * mm, "end": v(-6.2, -1.03) * mm});
            skLineSegment(sketch, "E662", {"start": v(-6.2, -1.03) * mm, "end": v(-6.32, -1.03) * mm});
            skLineSegment(sketch, "E663", {"start": v(-6.32, -1.03) * mm, "end": v(-6.43, -1.03) * mm});
            skLineSegment(sketch, "E664", {"start": v(-6.43, -1.03) * mm, "end": v(-6.55, -1.03) * mm});
            skLineSegment(sketch, "E665", {"start": v(-6.55, -1.03) * mm, "end": v(-6.66, -1.03) * mm});
            skLineSegment(sketch, "E666", {"start": v(-6.66, -1.03) * mm, "end": v(-6.77, -1.03) * mm});
            skLineSegment(sketch, "E667", {"start": v(-6.77, -1.03) * mm, "end": v(-6.89, -1.03) * mm});
            skLineSegment(sketch, "E668", {"start": v(-6.89, -1.03) * mm, "end": v(-7, -1.03) * mm});
            skLineSegment(sketch, "E669", {"start": v(-7, -1.03) * mm, "end": v(-7.11, -1.03) * mm});
            skLineSegment(sketch, "E670", {"start": v(-7.11, -1.03) * mm, "end": v(-7.23, -1.03) * mm});
            skLineSegment(sketch, "E671", {"start": v(-7.23, -1.03) * mm, "end": v(-7.34, -1.03) * mm});
            skLineSegment(sketch, "E672", {"start": v(-7.34, -1.03) * mm, "end": v(-7.45, -1.03) * mm});
            skLineSegment(sketch, "E673", {"start": v(-7.45, -1.03) * mm, "end": v(-7.56, -1.03) * mm});
            skLineSegment(sketch, "E674", {"start": v(-7.56, -1.03) * mm, "end": v(-7.68, -1.03) * mm});
            skLineSegment(sketch, "E675", {"start": v(-7.68, -1.03) * mm, "end": v(-7.8, -1.03) * mm});
            skLineSegment(sketch, "E676", {"start": v(-7.8, -1.03) * mm, "end": v(-7.9, -1.03) * mm});
            skLineSegment(sketch, "E677", {"start": v(-7.9, -1.03) * mm, "end": v(-8.02, -1.03) * mm});
            skLineSegment(sketch, "E678", {"start": v(-8.02, -1.03) * mm, "end": v(-8.15, -1.04) * mm});
            skLineSegment(sketch, "E679", {"start": v(-8.15, -1.04) * mm, "end": v(-8.28, -1.06) * mm});
            skLineSegment(sketch, "E680", {"start": v(-8.28, -1.06) * mm, "end": v(-8.4, -1.1) * mm});
            skLineSegment(sketch, "E681", {"start": v(-8.4, -1.1) * mm, "end": v(-8.52, -1.14) * mm});
            skLineSegment(sketch, "E682", {"start": v(-8.52, -1.14) * mm, "end": v(-8.63, -1.2) * mm});
            skLineSegment(sketch, "E683", {"start": v(-8.63, -1.2) * mm, "end": v(-8.74, -1.26) * mm});
            skLineSegment(sketch, "E684", {"start": v(-8.74, -1.26) * mm, "end": v(-8.84, -1.33) * mm});
            skLineSegment(sketch, "E685", {"start": v(-8.84, -1.33) * mm, "end": v(-8.93, -1.41) * mm});
            skLineSegment(sketch, "E686", {"start": v(-8.93, -1.41) * mm, "end": v(-9.02, -1.5) * mm});
            skLineSegment(sketch, "E687", {"start": v(-9.02, -1.5) * mm, "end": v(-9.09, -1.6) * mm});
            skLineSegment(sketch, "E688", {"start": v(-9.09, -1.6) * mm, "end": v(-9.15, -1.71) * mm});
            skLineSegment(sketch, "E689", {"start": v(-9.15, -1.71) * mm, "end": v(-9.2, -1.82) * mm});
            skLineSegment(sketch, "E690", {"start": v(-9.2, -1.82) * mm, "end": v(-9.25, -1.94) * mm});
            skLineSegment(sketch, "E691", {"start": v(-9.25, -1.94) * mm, "end": v(-9.28, -2.07) * mm});
            skLineSegment(sketch, "E692", {"start": v(-9.28, -2.07) * mm, "end": v(-9.3, -2.2) * mm});
            skLineSegment(sketch, "E693", {"start": v(-9.3, -2.2) * mm, "end": v(-9.31, -2.33) * mm});
            skLineSegment(sketch, "E694", {"start": v(-9.31, -2.33) * mm, "end": v(-9.31, -2.44) * mm});
            skLineSegment(sketch, "E695", {"start": v(-9.31, -2.44) * mm, "end": v(-9.31, -2.55) * mm});
            skLineSegment(sketch, "E696", {"start": v(-9.31, -2.55) * mm, "end": v(-9.31, -2.67) * mm});
            skLineSegment(sketch, "E697", {"start": v(-9.31, -2.67) * mm, "end": v(-9.31, -2.78) * mm});
            skLineSegment(sketch, "E698", {"start": v(-9.31, -2.78) * mm, "end": v(-9.31, -2.9) * mm});
            skLineSegment(sketch, "E699", {"start": v(-9.31, -2.9) * mm, "end": v(-9.31, -3) * mm});
            skLineSegment(sketch, "E700", {"start": v(-9.31, -3) * mm, "end": v(-9.31, -3.12) * mm});
            skLineSegment(sketch, "E701", {"start": v(-9.31, -3.12) * mm, "end": v(-9.31, -3.23) * mm});
            skLineSegment(sketch, "E702", {"start": v(-9.31, -3.23) * mm, "end": v(-9.31, -3.35) * mm});
            skLineSegment(sketch, "E703", {"start": v(-9.31, -3.35) * mm, "end": v(-9.31, -3.46) * mm});
            skLineSegment(sketch, "E704", {"start": v(-9.31, -3.46) * mm, "end": v(-9.31, -3.57) * mm});
            skLineSegment(sketch, "E705", {"start": v(-9.31, -3.57) * mm, "end": v(-9.31, -3.69) * mm});
            skLineSegment(sketch, "E706", {"start": v(-9.31, -3.69) * mm, "end": v(-9.31, -3.8) * mm});
            skLineSegment(sketch, "E707", {"start": v(-9.31, -3.8) * mm, "end": v(-9.31, -3.91) * mm});
            skLineSegment(sketch, "E708", {"start": v(-9.31, -3.91) * mm, "end": v(-9.31, -4.02) * mm});
            skLineSegment(sketch, "E709", {"start": v(-9.31, -4.02) * mm, "end": v(-9.31, -4.14) * mm});
            skLineSegment(sketch, "E710", {"start": v(-9.31, -4.14) * mm, "end": v(-9.44, -4.14) * mm});
            skLineSegment(sketch, "E711", {"start": v(-9.44, -4.14) * mm, "end": v(-9.57, -4.14) * mm});
            skLineSegment(sketch, "E712", {"start": v(-9.57, -4.14) * mm, "end": v(-9.7, -4.14) * mm});
            skLineSegment(sketch, "E713", {"start": v(-9.7, -4.14) * mm, "end": v(-9.83, -4.14) * mm});
            skLineSegment(sketch, "E714", {"start": v(-9.83, -4.14) * mm, "end": v(-9.96, -4.14) * mm});
            skLineSegment(sketch, "E715", {"start": v(-9.96, -4.14) * mm, "end": v(-10.09, -4.14) * mm});
            skLineSegment(sketch, "E716", {"start": v(-10.09, -4.14) * mm, "end": v(-10.22, -4.14) * mm});
            skLineSegment(sketch, "E717", {"start": v(-10.22, -4.14) * mm, "end": v(-10.34, -4.14) * mm});
            skLineSegment(sketch, "E718", {"start": v(-10.34, -4.14) * mm, "end": v(-10.47, -4.14) * mm});
            skLineSegment(sketch, "E719", {"start": v(-10.47, -4.14) * mm, "end": v(-10.6, -4.14) * mm});
            skLineSegment(sketch, "E720", {"start": v(-10.6, -4.14) * mm, "end": v(-10.73, -4.14) * mm});
            skLineSegment(sketch, "E721", {"start": v(-10.73, -4.14) * mm, "end": v(-10.86, -4.14) * mm});
            skLineSegment(sketch, "E722", {"start": v(-10.86, -4.14) * mm, "end": v(-11, -4.14) * mm});
            skLineSegment(sketch, "E723", {"start": v(-11, -4.14) * mm, "end": v(-11.12, -4.14) * mm});
            skLineSegment(sketch, "E724", {"start": v(-11.12, -4.14) * mm, "end": v(-11.25, -4.14) * mm});
            skLineSegment(sketch, "E725", {"start": v(-11.25, -4.14) * mm, "end": v(-11.38, -4.14) * mm});
            skLineSegment(sketch, "E726", {"start": v(-11.38, -4.14) * mm, "end": v(-11.6, -4.14) * mm});
            skLineSegment(sketch, "E727", {"start": v(-11.6, -4.14) * mm, "end": v(-11.83, -4.14) * mm});
            skLineSegment(sketch, "E728", {"start": v(-11.83, -4.14) * mm, "end": v(-12.06, -4.14) * mm});
            skLineSegment(sketch, "E729", {"start": v(-12.06, -4.14) * mm, "end": v(-12.28, -4.14) * mm});
            skLineSegment(sketch, "E730", {"start": v(-12.28, -4.14) * mm, "end": v(-12.51, -4.14) * mm});
            skLineSegment(sketch, "E731", {"start": v(-12.51, -4.14) * mm, "end": v(-12.74, -4.14) * mm});
            skLineSegment(sketch, "E732", {"start": v(-12.74, -4.14) * mm, "end": v(-12.96, -4.14) * mm});
            skLineSegment(sketch, "E733", {"start": v(-12.96, -4.14) * mm, "end": v(-13.19, -4.14) * mm});
            skLineSegment(sketch, "E734", {"start": v(-13.19, -4.14) * mm, "end": v(-13.42, -4.14) * mm});
            skLineSegment(sketch, "E735", {"start": v(-13.42, -4.14) * mm, "end": v(-13.64, -4.14) * mm});
            skLineSegment(sketch, "E736", {"start": v(-13.64, -4.14) * mm, "end": v(-13.87, -4.14) * mm});
            skLineSegment(sketch, "E737", {"start": v(-13.87, -4.14) * mm, "end": v(-14.1, -4.14) * mm});
            skLineSegment(sketch, "E738", {"start": v(-14.1, -4.14) * mm, "end": v(-14.32, -4.14) * mm});
            skLineSegment(sketch, "E739", {"start": v(-14.32, -4.14) * mm, "end": v(-14.55, -4.14) * mm});
            skLineSegment(sketch, "E740", {"start": v(-14.55, -4.14) * mm, "end": v(-14.77, -4.14) * mm});
            skLineSegment(sketch, "E741", {"start": v(-14.77, -4.14) * mm, "end": v(-15, -4.14) * mm});
            skLineSegment(sketch, "E742", {"start": v(-15, -4.14) * mm, "end": v(-14.95, -4.27) * mm});
            skLineSegment(sketch, "E743", {"start": v(-14.95, -4.27) * mm, "end": v(-14.9, -4.4) * mm});
            skLineSegment(sketch, "E744", {"start": v(-14.9, -4.4) * mm, "end": v(-14.84, -4.53) * mm});
            skLineSegment(sketch, "E745", {"start": v(-14.84, -4.53) * mm, "end": v(-14.8, -4.66) * mm});
            skLineSegment(sketch, "E746", {"start": v(-14.8, -4.66) * mm, "end": v(-14.74, -4.78) * mm});
            skLineSegment(sketch, "E747", {"start": v(-14.74, -4.78) * mm, "end": v(-14.69, -4.91) * mm});
            skLineSegment(sketch, "E748", {"start": v(-14.69, -4.91) * mm, "end": v(-14.64, -5.04) * mm});
            skLineSegment(sketch, "E749", {"start": v(-14.64, -5.04) * mm, "end": v(-14.59, -5.17) * mm});
            skLineSegment(sketch, "E750", {"start": v(-14.59, -5.17) * mm, "end": v(-14.53, -5.3) * mm});
            skLineSegment(sketch, "E751", {"start": v(-14.53, -5.3) * mm, "end": v(-14.48, -5.43) * mm});
            skLineSegment(sketch, "E752", {"start": v(-14.48, -5.43) * mm, "end": v(-14.43, -5.56) * mm});
            skLineSegment(sketch, "E753", {"start": v(-14.43, -5.56) * mm, "end": v(-14.38, -5.69) * mm});
            skLineSegment(sketch, "E754", {"start": v(-14.38, -5.69) * mm, "end": v(-14.33, -5.82) * mm});
            skLineSegment(sketch, "E755", {"start": v(-14.33, -5.82) * mm, "end": v(-14.28, -5.95) * mm});
            skLineSegment(sketch, "E756", {"start": v(-14.28, -5.95) * mm, "end": v(-14.22, -6.08) * mm});
            skLineSegment(sketch, "E757", {"start": v(-14.22, -6.08) * mm, "end": v(-14.17, -6.2) * mm});
            skLineSegment(sketch, "E758", {"start": v(-14.17, -6.2) * mm, "end": v(-14.16, -6.24) * mm});
            skLineSegment(sketch, "E759", {"start": v(-14.16, -6.24) * mm, "end": v(-14.15, -6.27) * mm});
            skLineSegment(sketch, "E760", {"start": v(-14.15, -6.27) * mm, "end": v(-14.13, -6.3) * mm});
            skLineSegment(sketch, "E761", {"start": v(-14.13, -6.3) * mm, "end": v(-14.12, -6.34) * mm});
            skLineSegment(sketch, "E762", {"start": v(-14.12, -6.34) * mm, "end": v(-14.1, -6.37) * mm});
            skLineSegment(sketch, "E763", {"start": v(-14.1, -6.37) * mm, "end": v(-14.1, -6.4) * mm});
            skLineSegment(sketch, "E764", {"start": v(-14.1, -6.4) * mm, "end": v(-14.08, -6.43) * mm});
            skLineSegment(sketch, "E765", {"start": v(-14.08, -6.43) * mm, "end": v(-14.07, -6.47) * mm});
            skLineSegment(sketch, "E766", {"start": v(-14.07, -6.47) * mm, "end": v(-14.06, -6.5) * mm});
            skLineSegment(sketch, "E767", {"start": v(-14.06, -6.5) * mm, "end": v(-14.04, -6.53) * mm});
            skLineSegment(sketch, "E768", {"start": v(-14.04, -6.53) * mm, "end": v(-14.03, -6.56) * mm});
            skLineSegment(sketch, "E769", {"start": v(-14.03, -6.56) * mm, "end": v(-14.02, -6.6) * mm});
            skLineSegment(sketch, "E770", {"start": v(-14.02, -6.6) * mm, "end": v(-14, -6.63) * mm});
            skLineSegment(sketch, "E771", {"start": v(-14, -6.63) * mm, "end": v(-14, -6.66) * mm});
            skLineSegment(sketch, "E772", {"start": v(-14, -6.66) * mm, "end": v(-13.98, -6.7) * mm});
            skLineSegment(sketch, "E773", {"start": v(-13.98, -6.7) * mm, "end": v(-13.97, -6.72) * mm});
            skLineSegment(sketch, "E774", {"start": v(-13.97, -6.72) * mm, "end": v(-13.65, -6.86) * mm});
            skLineSegment(sketch, "E775", {"start": v(-13.65, -6.86) * mm, "end": v(-13.33, -7) * mm});
            skLineSegment(sketch, "E776", {"start": v(-13.33, -7) * mm, "end": v(-13, -7.12) * mm});
            skLineSegment(sketch, "E777", {"start": v(-13, -7.12) * mm, "end": v(-12.69, -7.26) * mm});
            skLineSegment(sketch, "E778", {"start": v(-12.69, -7.26) * mm, "end": v(-12.37, -7.39) * mm});
            skLineSegment(sketch, "E779", {"start": v(-12.37, -7.39) * mm, "end": v(-12.05, -7.52) * mm});
            skLineSegment(sketch, "E780", {"start": v(-12.05, -7.52) * mm, "end": v(-11.73, -7.66) * mm});
            skLineSegment(sketch, "E781", {"start": v(-11.73, -7.66) * mm, "end": v(-11.4, -7.79) * mm});
            skLineSegment(sketch, "E782", {"start": v(-11.4, -7.79) * mm, "end": v(-11.1, -7.92) * mm});
            skLineSegment(sketch, "E783", {"start": v(-11.1, -7.92) * mm, "end": v(-10.77, -8.06) * mm});
            skLineSegment(sketch, "E784", {"start": v(-10.77, -8.06) * mm, "end": v(-10.45, -8.19) * mm});
            skLineSegment(sketch, "E785", {"start": v(-10.45, -8.19) * mm, "end": v(-10.13, -8.32) * mm});
            skLineSegment(sketch, "E786", {"start": v(-10.13, -8.32) * mm, "end": v(-9.81, -8.45) * mm});
            skLineSegment(sketch, "E787", {"start": v(-9.81, -8.45) * mm, "end": v(-9.5, -8.59) * mm});
            skLineSegment(sketch, "E788", {"start": v(-9.5, -8.59) * mm, "end": v(-9.17, -8.72) * mm});
            skLineSegment(sketch, "E789", {"start": v(-9.17, -8.72) * mm, "end": v(-8.85, -8.85) * mm});
            skLineSegment(sketch, "E790", {"start": v(-8.85, -8.85) * mm, "end": v(-8.72, -9.17) * mm});
            skLineSegment(sketch, "E791", {"start": v(-8.72, -9.17) * mm, "end": v(-8.59, -9.5) * mm});
            skLineSegment(sketch, "E792", {"start": v(-8.59, -9.5) * mm, "end": v(-8.45, -9.81) * mm});
            skLineSegment(sketch, "E793", {"start": v(-8.45, -9.81) * mm, "end": v(-8.32, -10.13) * mm});
            skLineSegment(sketch, "E794", {"start": v(-8.32, -10.13) * mm, "end": v(-8.19, -10.45) * mm});
            skLineSegment(sketch, "E795", {"start": v(-8.19, -10.45) * mm, "end": v(-8.06, -10.77) * mm});
            skLineSegment(sketch, "E796", {"start": v(-8.06, -10.77) * mm, "end": v(-7.92, -11.1) * mm});
            skLineSegment(sketch, "E797", {"start": v(-7.92, -11.1) * mm, "end": v(-7.79, -11.4) * mm});
            skLineSegment(sketch, "E798", {"start": v(-7.79, -11.4) * mm, "end": v(-7.66, -11.73) * mm});
            skLineSegment(sketch, "E799", {"start": v(-7.66, -11.73) * mm, "end": v(-7.52, -12.05) * mm});
            skLineSegment(sketch, "E800", {"start": v(-7.52, -12.05) * mm, "end": v(-7.39, -12.37) * mm});
            skLineSegment(sketch, "E801", {"start": v(-7.39, -12.37) * mm, "end": v(-7.26, -12.69) * mm});
            skLineSegment(sketch, "E802", {"start": v(-7.26, -12.69) * mm, "end": v(-7.12, -13) * mm});
            skLineSegment(sketch, "E803", {"start": v(-7.12, -13) * mm, "end": v(-7, -13.33) * mm});
            skLineSegment(sketch, "E804", {"start": v(-7, -13.33) * mm, "end": v(-6.86, -13.65) * mm});
            skLineSegment(sketch, "E805", {"start": v(-6.86, -13.65) * mm, "end": v(-6.72, -13.97) * mm});
            skLineSegment(sketch, "E806", {"start": v(-6.72, -13.97) * mm, "end": v(-6.7, -13.98) * mm});
            skLineSegment(sketch, "E807", {"start": v(-6.7, -13.98) * mm, "end": v(-6.66, -14) * mm});
            skLineSegment(sketch, "E808", {"start": v(-6.66, -14) * mm, "end": v(-6.63, -14) * mm});
            skLineSegment(sketch, "E809", {"start": v(-6.63, -14) * mm, "end": v(-6.6, -14.02) * mm});
            skLineSegment(sketch, "E810", {"start": v(-6.6, -14.02) * mm, "end": v(-6.56, -14.03) * mm});
            skLineSegment(sketch, "E811", {"start": v(-6.56, -14.03) * mm, "end": v(-6.53, -14.04) * mm});
            skLineSegment(sketch, "E812", {"start": v(-6.53, -14.04) * mm, "end": v(-6.5, -14.06) * mm});
            skLineSegment(sketch, "E813", {"start": v(-6.5, -14.06) * mm, "end": v(-6.47, -14.07) * mm});
            skLineSegment(sketch, "E814", {"start": v(-6.47, -14.07) * mm, "end": v(-6.43, -14.08) * mm});
            skLineSegment(sketch, "E815", {"start": v(-6.43, -14.08) * mm, "end": v(-6.4, -14.1) * mm});
            skLineSegment(sketch, "E816", {"start": v(-6.4, -14.1) * mm, "end": v(-6.37, -14.1) * mm});
            skLineSegment(sketch, "E817", {"start": v(-6.37, -14.1) * mm, "end": v(-6.34, -14.12) * mm});
            skLineSegment(sketch, "E818", {"start": v(-6.34, -14.12) * mm, "end": v(-6.3, -14.13) * mm});
            skLineSegment(sketch, "E819", {"start": v(-6.3, -14.13) * mm, "end": v(-6.27, -14.15) * mm});
            skLineSegment(sketch, "E820", {"start": v(-6.27, -14.15) * mm, "end": v(-6.24, -14.16) * mm});
            skLineSegment(sketch, "E821", {"start": v(-6.24, -14.16) * mm, "end": v(-6.2, -14.17) * mm});
            skLineSegment(sketch, "E822", {"start": v(-6.2, -14.17) * mm, "end": v(-6.08, -14.22) * mm});
            skLineSegment(sketch, "E823", {"start": v(-6.08, -14.22) * mm, "end": v(-5.95, -14.28) * mm});
            skLineSegment(sketch, "E824", {"start": v(-5.95, -14.28) * mm, "end": v(-5.82, -14.33) * mm});
            skLineSegment(sketch, "E825", {"start": v(-5.82, -14.33) * mm, "end": v(-5.69, -14.38) * mm});
            skLineSegment(sketch, "E826", {"start": v(-5.69, -14.38) * mm, "end": v(-5.56, -14.43) * mm});
            skLineSegment(sketch, "E827", {"start": v(-5.56, -14.43) * mm, "end": v(-5.43, -14.48) * mm});
            skLineSegment(sketch, "E828", {"start": v(-5.43, -14.48) * mm, "end": v(-5.3, -14.53) * mm});
            skLineSegment(sketch, "E829", {"start": v(-5.3, -14.53) * mm, "end": v(-5.17, -14.59) * mm});
            skLineSegment(sketch, "E830", {"start": v(-5.17, -14.59) * mm, "end": v(-5.04, -14.64) * mm});
            skLineSegment(sketch, "E831", {"start": v(-5.04, -14.64) * mm, "end": v(-4.91, -14.69) * mm});
            skLineSegment(sketch, "E832", {"start": v(-4.91, -14.69) * mm, "end": v(-4.78, -14.74) * mm});
            skLineSegment(sketch, "E833", {"start": v(-4.78, -14.74) * mm, "end": v(-4.66, -14.8) * mm});
            skLineSegment(sketch, "E834", {"start": v(-4.66, -14.8) * mm, "end": v(-4.53, -14.84) * mm});
            skLineSegment(sketch, "E835", {"start": v(-4.53, -14.84) * mm, "end": v(-4.4, -14.9) * mm});
            skLineSegment(sketch, "E836", {"start": v(-4.4, -14.9) * mm, "end": v(-4.27, -14.95) * mm});
            skLineSegment(sketch, "E837", {"start": v(-4.27, -14.95) * mm, "end": v(-4.14, -15) * mm});
            skLineSegment(sketch, "E838", {"start": v(-4.14, -15) * mm, "end": v(-4.14, -14.77) * mm});
            skLineSegment(sketch, "E839", {"start": v(-4.14, -14.77) * mm, "end": v(-4.14, -14.55) * mm});
            skLineSegment(sketch, "E840", {"start": v(-4.14, -14.55) * mm, "end": v(-4.14, -14.32) * mm});
            skLineSegment(sketch, "E841", {"start": v(-4.14, -14.32) * mm, "end": v(-4.14, -14.1) * mm});
            skLineSegment(sketch, "E842", {"start": v(-4.14, -14.1) * mm, "end": v(-4.14, -13.87) * mm});
            skLineSegment(sketch, "E843", {"start": v(-4.14, -13.87) * mm, "end": v(-4.14, -13.64) * mm});
            skLineSegment(sketch, "E844", {"start": v(-4.14, -13.64) * mm, "end": v(-4.14, -13.42) * mm});
            skLineSegment(sketch, "E845", {"start": v(-4.14, -13.42) * mm, "end": v(-4.14, -13.19) * mm});
            skLineSegment(sketch, "E846", {"start": v(-4.14, -13.19) * mm, "end": v(-4.14, -12.96) * mm});
            skLineSegment(sketch, "E847", {"start": v(-4.14, -12.96) * mm, "end": v(-4.14, -12.74) * mm});
            skLineSegment(sketch, "E848", {"start": v(-4.14, -12.74) * mm, "end": v(-4.14, -12.51) * mm});
            skLineSegment(sketch, "E849", {"start": v(-4.14, -12.51) * mm, "end": v(-4.14, -12.28) * mm});
            skLineSegment(sketch, "E850", {"start": v(-4.14, -12.28) * mm, "end": v(-4.14, -12.06) * mm});
            skLineSegment(sketch, "E851", {"start": v(-4.14, -12.06) * mm, "end": v(-4.14, -11.83) * mm});
            skLineSegment(sketch, "E852", {"start": v(-4.14, -11.83) * mm, "end": v(-4.14, -11.6) * mm});
            skLineSegment(sketch, "E853", {"start": v(-4.14, -11.6) * mm, "end": v(-4.14, -11.38) * mm});
            skLineSegment(sketch, "E854", {"start": v(-4.14, -11.38) * mm, "end": v(-4.14, -11.25) * mm});
            skLineSegment(sketch, "E855", {"start": v(-4.14, -11.25) * mm, "end": v(-4.14, -11.12) * mm});
            skLineSegment(sketch, "E856", {"start": v(-4.14, -11.12) * mm, "end": v(-4.14, -11) * mm});
            skLineSegment(sketch, "E857", {"start": v(-4.14, -11) * mm, "end": v(-4.14, -10.86) * mm});
            skLineSegment(sketch, "E858", {"start": v(-4.14, -10.86) * mm, "end": v(-4.14, -10.73) * mm});
            skLineSegment(sketch, "E859", {"start": v(-4.14, -10.73) * mm, "end": v(-4.14, -10.6) * mm});
            skLineSegment(sketch, "E860", {"start": v(-4.14, -10.6) * mm, "end": v(-4.14, -10.47) * mm});
            skLineSegment(sketch, "E861", {"start": v(-4.14, -10.47) * mm, "end": v(-4.14, -10.34) * mm});
            skLineSegment(sketch, "E862", {"start": v(-4.14, -10.34) * mm, "end": v(-4.14, -10.22) * mm});
            skLineSegment(sketch, "E863", {"start": v(-4.14, -10.22) * mm, "end": v(-4.14, -10.09) * mm});
            skLineSegment(sketch, "E864", {"start": v(-4.14, -10.09) * mm, "end": v(-4.14, -9.96) * mm});
            skLineSegment(sketch, "E865", {"start": v(-4.14, -9.96) * mm, "end": v(-4.14, -9.83) * mm});
            skLineSegment(sketch, "E866", {"start": v(-4.14, -9.83) * mm, "end": v(-4.14, -9.7) * mm});
            skLineSegment(sketch, "E867", {"start": v(-4.14, -9.7) * mm, "end": v(-4.14, -9.57) * mm});
            skLineSegment(sketch, "E868", {"start": v(-4.14, -9.57) * mm, "end": v(-4.14, -9.44) * mm});
            skLineSegment(sketch, "E869", {"start": v(-4.14, -9.44) * mm, "end": v(-4.14, -9.31) * mm});
            skLineSegment(sketch, "E870", {"start": v(-4.14, -9.31) * mm, "end": v(-4.02, -9.31) * mm});
            skLineSegment(sketch, "E871", {"start": v(-4.02, -9.31) * mm, "end": v(-3.91, -9.31) * mm});
            skLineSegment(sketch, "E872", {"start": v(-3.91, -9.31) * mm, "end": v(-3.8, -9.31) * mm});
            skLineSegment(sketch, "E873", {"start": v(-3.8, -9.31) * mm, "end": v(-3.69, -9.31) * mm});
            skLineSegment(sketch, "E874", {"start": v(-3.69, -9.31) * mm, "end": v(-3.57, -9.31) * mm});
            skLineSegment(sketch, "E875", {"start": v(-3.57, -9.31) * mm, "end": v(-3.46, -9.31) * mm});
            skLineSegment(sketch, "E876", {"start": v(-3.46, -9.31) * mm, "end": v(-3.35, -9.31) * mm});
            skLineSegment(sketch, "E877", {"start": v(-3.35, -9.31) * mm, "end": v(-3.23, -9.31) * mm});
            skLineSegment(sketch, "E878", {"start": v(-3.23, -9.31) * mm, "end": v(-3.12, -9.31) * mm});
            skLineSegment(sketch, "E879", {"start": v(-3.12, -9.31) * mm, "end": v(-3, -9.31) * mm});
            skLineSegment(sketch, "E880", {"start": v(-3, -9.31) * mm, "end": v(-2.9, -9.31) * mm});
            skLineSegment(sketch, "E881", {"start": v(-2.9, -9.31) * mm, "end": v(-2.78, -9.31) * mm});
            skLineSegment(sketch, "E882", {"start": v(-2.78, -9.31) * mm, "end": v(-2.67, -9.31) * mm});
            skLineSegment(sketch, "E883", {"start": v(-2.67, -9.31) * mm, "end": v(-2.55, -9.31) * mm});
            skLineSegment(sketch, "E884", {"start": v(-2.55, -9.31) * mm, "end": v(-2.44, -9.31) * mm});
            skLineSegment(sketch, "E885", {"start": v(-2.44, -9.31) * mm, "end": v(-2.33, -9.31) * mm});
            skLineSegment(sketch, "E886", {"start": v(-2.33, -9.31) * mm, "end": v(-2.2, -9.3) * mm});
            skLineSegment(sketch, "E887", {"start": v(-2.2, -9.3) * mm, "end": v(-2.07, -9.28) * mm});
            skLineSegment(sketch, "E888", {"start": v(-2.07, -9.28) * mm, "end": v(-1.94, -9.25) * mm});
            skLineSegment(sketch, "E889", {"start": v(-1.94, -9.25) * mm, "end": v(-1.82, -9.2) * mm});
            skLineSegment(sketch, "E890", {"start": v(-1.82, -9.2) * mm, "end": v(-1.71, -9.15) * mm});
            skLineSegment(sketch, "E891", {"start": v(-1.71, -9.15) * mm, "end": v(-1.6, -9.09) * mm});
            skLineSegment(sketch, "E892", {"start": v(-1.6, -9.09) * mm, "end": v(-1.5, -9.02) * mm});
            skLineSegment(sketch, "E893", {"start": v(-1.5, -9.02) * mm, "end": v(-1.41, -8.93) * mm});
            skLineSegment(sketch, "E894", {"start": v(-1.41, -8.93) * mm, "end": v(-1.33, -8.84) * mm});
            skLineSegment(sketch, "E895", {"start": v(-1.33, -8.84) * mm, "end": v(-1.26, -8.74) * mm});
            skLineSegment(sketch, "E896", {"start": v(-1.26, -8.74) * mm, "end": v(-1.2, -8.63) * mm});
            skLineSegment(sketch, "E897", {"start": v(-1.2, -8.63) * mm, "end": v(-1.14, -8.52) * mm});
            skLineSegment(sketch, "E898", {"start": v(-1.14, -8.52) * mm, "end": v(-1.1, -8.4) * mm});
            skLineSegment(sketch, "E899", {"start": v(-1.1, -8.4) * mm, "end": v(-1.06, -8.28) * mm});
            skLineSegment(sketch, "E900", {"start": v(-1.06, -8.28) * mm, "end": v(-1.04, -8.15) * mm});
            skLineSegment(sketch, "E901", {"start": v(-1.04, -8.15) * mm, "end": v(-1.03, -8.02) * mm});
            skLineSegment(sketch, "E902", {"start": v(-1.03, -8.02) * mm, "end": v(-1.03, -7.9) * mm});
            skLineSegment(sketch, "E903", {"start": v(-1.03, -7.9) * mm, "end": v(-1.03, -7.8) * mm});
            skLineSegment(sketch, "E904", {"start": v(-1.03, -7.8) * mm, "end": v(-1.03, -7.68) * mm});
            skLineSegment(sketch, "E905", {"start": v(-1.03, -7.68) * mm, "end": v(-1.03, -7.56) * mm});
            skLineSegment(sketch, "E906", {"start": v(-1.03, -7.56) * mm, "end": v(-1.03, -7.45) * mm});
            skLineSegment(sketch, "E907", {"start": v(-1.03, -7.45) * mm, "end": v(-1.03, -7.34) * mm});
            skLineSegment(sketch, "E908", {"start": v(-1.03, -7.34) * mm, "end": v(-1.03, -7.23) * mm});
            skLineSegment(sketch, "E909", {"start": v(-1.03, -7.23) * mm, "end": v(-1.03, -7.11) * mm});
            skLineSegment(sketch, "E910", {"start": v(-1.03, -7.11) * mm, "end": v(-1.03, -7) * mm});
            skLineSegment(sketch, "E911", {"start": v(-1.03, -7) * mm, "end": v(-1.03, -6.89) * mm});
            skLineSegment(sketch, "E912", {"start": v(-1.03, -6.89) * mm, "end": v(-1.03, -6.77) * mm});
            skLineSegment(sketch, "E913", {"start": v(-1.03, -6.77) * mm, "end": v(-1.03, -6.66) * mm});
            skLineSegment(sketch, "E914", {"start": v(-1.03, -6.66) * mm, "end": v(-1.03, -6.55) * mm});
            skLineSegment(sketch, "E915", {"start": v(-1.03, -6.55) * mm, "end": v(-1.03, -6.43) * mm});
            skLineSegment(sketch, "E916", {"start": v(-1.03, -6.43) * mm, "end": v(-1.03, -6.32) * mm});
            skLineSegment(sketch, "E917", {"start": v(-1.03, -6.32) * mm, "end": v(-1.03, -6.2) * mm});
            skLineSegment(sketch, "E918", {"start": v(-1.03, -6.2) * mm, "end": v(-0.97, -6.2) * mm});
            skLineSegment(sketch, "E919", {"start": v(-0.97, -6.2) * mm, "end": v(-0.9, -6.2) * mm});
            skLineSegment(sketch, "E920", {"start": v(-0.9, -6.2) * mm, "end": v(-0.84, -6.2) * mm});
            skLineSegment(sketch, "E921", {"start": v(-0.84, -6.2) * mm, "end": v(-0.78, -6.2) * mm});
            skLineSegment(sketch, "E922", {"start": v(-0.78, -6.2) * mm, "end": v(-0.71, -6.2) * mm});
            skLineSegment(sketch, "E923", {"start": v(-0.71, -6.2) * mm, "end": v(-0.65, -6.2) * mm});
            skLineSegment(sketch, "E924", {"start": v(-0.65, -6.2) * mm, "end": v(-0.58, -6.2) * mm});
            skLineSegment(sketch, "E925", {"start": v(-0.58, -6.2) * mm, "end": v(-0.52, -6.2) * mm});
            skLineSegment(sketch, "E926", {"start": v(-0.52, -6.2) * mm, "end": v(-0.45, -6.2) * mm});
            skLineSegment(sketch, "E927", {"start": v(-0.45, -6.2) * mm, "end": v(-0.39, -6.2) * mm});
            skLineSegment(sketch, "E928", {"start": v(-0.39, -6.2) * mm, "end": v(-0.32, -6.2) * mm});
            skLineSegment(sketch, "E929", {"start": v(-0.32, -6.2) * mm, "end": v(-0.26, -6.2) * mm});
            skLineSegment(sketch, "E930", {"start": v(-0.26, -6.2) * mm, "end": v(-0.2, -6.2) * mm});
            skLineSegment(sketch, "E931", {"start": v(-0.2, -6.2) * mm, "end": v(-0.13, -6.2) * mm});
            skLineSegment(sketch, "E932", {"start": v(-0.13, -6.2) * mm, "end": v(-0.06, -6.2) * mm});
            skLineSegment(sketch, "E933", {"start": v(-0.06, -6.2) * mm, "end": v(0, -6.2) * mm});
            skLineSegment(sketch, "E934", {"start": v(0, -6.2) * mm, "end": v(0.06, -6.2) * mm});
            skLineSegment(sketch, "E935", {"start": v(0.06, -6.2) * mm, "end": v(0.13, -6.2) * mm});
            skLineSegment(sketch, "E936", {"start": v(0.13, -6.2) * mm, "end": v(0.2, -6.2) * mm});
            skLineSegment(sketch, "E937", {"start": v(0.2, -6.2) * mm, "end": v(0.26, -6.2) * mm});
            skLineSegment(sketch, "E938", {"start": v(0.26, -6.2) * mm, "end": v(0.32, -6.2) * mm});
            skLineSegment(sketch, "E939", {"start": v(0.32, -6.2) * mm, "end": v(0.39, -6.2) * mm});
            skLineSegment(sketch, "E940", {"start": v(0.39, -6.2) * mm, "end": v(0.45, -6.2) * mm});
            skLineSegment(sketch, "E941", {"start": v(0.45, -6.2) * mm, "end": v(0.52, -6.2) * mm});
            skLineSegment(sketch, "E942", {"start": v(0.52, -6.2) * mm, "end": v(0.58, -6.2) * mm});
            skLineSegment(sketch, "E943", {"start": v(0.58, -6.2) * mm, "end": v(0.65, -6.2) * mm});
            skLineSegment(sketch, "E944", {"start": v(0.65, -6.2) * mm, "end": v(0.71, -6.2) * mm});
            skLineSegment(sketch, "E945", {"start": v(0.71, -6.2) * mm, "end": v(0.78, -6.2) * mm});
            skLineSegment(sketch, "E946", {"start": v(0.78, -6.2) * mm, "end": v(0.84, -6.2) * mm});
            skLineSegment(sketch, "E947", {"start": v(0.84, -6.2) * mm, "end": v(0.9, -6.2) * mm});
            skLineSegment(sketch, "E948", {"start": v(0.9, -6.2) * mm, "end": v(0.97, -6.2) * mm});
            skLineSegment(sketch, "E949", {"start": v(0.97, -6.2) * mm, "end": v(1.03, -6.2) * mm});
            skLineSegment(sketch, "E950", {"start": v(1.03, -6.2) * mm, "end": v(1.03, -6.32) * mm});
            skLineSegment(sketch, "E951", {"start": v(1.03, -6.32) * mm, "end": v(1.03, -6.43) * mm});
            skLineSegment(sketch, "E952", {"start": v(1.03, -6.43) * mm, "end": v(1.03, -6.55) * mm});
            skLineSegment(sketch, "E953", {"start": v(1.03, -6.55) * mm, "end": v(1.03, -6.66) * mm});
            skLineSegment(sketch, "E954", {"start": v(1.03, -6.66) * mm, "end": v(1.03, -6.77) * mm});
            skLineSegment(sketch, "E955", {"start": v(1.03, -6.77) * mm, "end": v(1.03, -6.89) * mm});
            skLineSegment(sketch, "E956", {"start": v(1.03, -6.89) * mm, "end": v(1.03, -7) * mm});
            skLineSegment(sketch, "E957", {"start": v(1.03, -7) * mm, "end": v(1.03, -7.11) * mm});
            skLineSegment(sketch, "E958", {"start": v(1.03, -7.11) * mm, "end": v(1.03, -7.23) * mm});
            skLineSegment(sketch, "E959", {"start": v(1.03, -7.23) * mm, "end": v(1.03, -7.34) * mm});
            skLineSegment(sketch, "E960", {"start": v(1.03, -7.34) * mm, "end": v(1.03, -7.45) * mm});
            skLineSegment(sketch, "E961", {"start": v(1.03, -7.45) * mm, "end": v(1.03, -7.56) * mm});
            skLineSegment(sketch, "E962", {"start": v(1.03, -7.56) * mm, "end": v(1.03, -7.68) * mm});
            skLineSegment(sketch, "E963", {"start": v(1.03, -7.68) * mm, "end": v(1.03, -7.8) * mm});
            skLineSegment(sketch, "E964", {"start": v(1.03, -7.8) * mm, "end": v(1.03, -7.9) * mm});
            skLineSegment(sketch, "E965", {"start": v(1.03, -7.9) * mm, "end": v(1.03, -8.02) * mm});
            skLineSegment(sketch, "E966", {"start": v(1.03, -8.02) * mm, "end": v(1.04, -8.15) * mm});
            skLineSegment(sketch, "E967", {"start": v(1.04, -8.15) * mm, "end": v(1.06, -8.28) * mm});
            skLineSegment(sketch, "E968", {"start": v(1.06, -8.28) * mm, "end": v(1.1, -8.4) * mm});
            skLineSegment(sketch, "E969", {"start": v(1.1, -8.4) * mm, "end": v(1.14, -8.52) * mm});
            skLineSegment(sketch, "E970", {"start": v(1.14, -8.52) * mm, "end": v(1.2, -8.63) * mm});
            skLineSegment(sketch, "E971", {"start": v(1.2, -8.63) * mm, "end": v(1.26, -8.74) * mm});
            skLineSegment(sketch, "E972", {"start": v(1.26, -8.74) * mm, "end": v(1.33, -8.84) * mm});
            skLineSegment(sketch, "E973", {"start": v(1.33, -8.84) * mm, "end": v(1.41, -8.93) * mm});
            skLineSegment(sketch, "E974", {"start": v(1.41, -8.93) * mm, "end": v(1.5, -9.02) * mm});
            skLineSegment(sketch, "E975", {"start": v(1.5, -9.02) * mm, "end": v(1.6, -9.09) * mm});
            skLineSegment(sketch, "E976", {"start": v(1.6, -9.09) * mm, "end": v(1.71, -9.15) * mm});
            skLineSegment(sketch, "E977", {"start": v(1.71, -9.15) * mm, "end": v(1.82, -9.2) * mm});
            skLineSegment(sketch, "E978", {"start": v(1.82, -9.2) * mm, "end": v(1.94, -9.25) * mm});
            skLineSegment(sketch, "E979", {"start": v(1.94, -9.25) * mm, "end": v(2.07, -9.28) * mm});
            skLineSegment(sketch, "E980", {"start": v(2.07, -9.28) * mm, "end": v(2.2, -9.3) * mm});
            skLineSegment(sketch, "E981", {"start": v(2.2, -9.3) * mm, "end": v(2.33, -9.31) * mm});
            skLineSegment(sketch, "E982", {"start": v(2.33, -9.31) * mm, "end": v(2.44, -9.31) * mm});
            skLineSegment(sketch, "E983", {"start": v(2.44, -9.31) * mm, "end": v(2.55, -9.31) * mm});
            skLineSegment(sketch, "E984", {"start": v(2.55, -9.31) * mm, "end": v(2.67, -9.31) * mm});
            skLineSegment(sketch, "E985", {"start": v(2.67, -9.31) * mm, "end": v(2.78, -9.31) * mm});
            skLineSegment(sketch, "E986", {"start": v(2.78, -9.31) * mm, "end": v(2.9, -9.31) * mm});
            skLineSegment(sketch, "E987", {"start": v(2.9, -9.31) * mm, "end": v(3, -9.31) * mm});
            skLineSegment(sketch, "E988", {"start": v(3, -9.31) * mm, "end": v(3.12, -9.31) * mm});
            skLineSegment(sketch, "E989", {"start": v(3.12, -9.31) * mm, "end": v(3.23, -9.31) * mm});
            skLineSegment(sketch, "E990", {"start": v(3.23, -9.31) * mm, "end": v(3.35, -9.31) * mm});
            skLineSegment(sketch, "E991", {"start": v(3.35, -9.31) * mm, "end": v(3.46, -9.31) * mm});
            skLineSegment(sketch, "E992", {"start": v(3.46, -9.31) * mm, "end": v(3.57, -9.31) * mm});
            skLineSegment(sketch, "E993", {"start": v(3.57, -9.31) * mm, "end": v(3.69, -9.31) * mm});
            skLineSegment(sketch, "E994", {"start": v(3.69, -9.31) * mm, "end": v(3.8, -9.31) * mm});
            skLineSegment(sketch, "E995", {"start": v(3.8, -9.31) * mm, "end": v(3.91, -9.31) * mm});
            skLineSegment(sketch, "E996", {"start": v(3.91, -9.31) * mm, "end": v(4.02, -9.31) * mm});
            skLineSegment(sketch, "E997", {"start": v(4.02, -9.31) * mm, "end": v(4.14, -9.31) * mm});
            skLineSegment(sketch, "E998", {"start": v(4.14, -9.31) * mm, "end": v(4.14, -9.44) * mm});
            skLineSegment(sketch, "E999", {"start": v(4.14, -9.44) * mm, "end": v(4.14, -9.57) * mm});
            skLineSegment(sketch, "E1000", {"start": v(4.14, -9.57) * mm, "end": v(4.14, -9.7) * mm});
            skLineSegment(sketch, "E1001", {"start": v(4.14, -9.7) * mm, "end": v(4.14, -9.83) * mm});
            skLineSegment(sketch, "E1002", {"start": v(4.14, -9.83) * mm, "end": v(4.14, -9.96) * mm});
            skLineSegment(sketch, "E1003", {"start": v(4.14, -9.96) * mm, "end": v(4.14, -10.09) * mm});
            skLineSegment(sketch, "E1004", {"start": v(4.14, -10.09) * mm, "end": v(4.14, -10.22) * mm});
            skLineSegment(sketch, "E1005", {"start": v(4.14, -10.22) * mm, "end": v(4.14, -10.34) * mm});
            skLineSegment(sketch, "E1006", {"start": v(4.14, -10.34) * mm, "end": v(4.14, -10.47) * mm});
            skLineSegment(sketch, "E1007", {"start": v(4.14, -10.47) * mm, "end": v(4.14, -10.6) * mm});
            skLineSegment(sketch, "E1008", {"start": v(4.14, -10.6) * mm, "end": v(4.14, -10.73) * mm});
            skLineSegment(sketch, "E1009", {"start": v(4.14, -10.73) * mm, "end": v(4.14, -10.86) * mm});
            skLineSegment(sketch, "E1010", {"start": v(4.14, -10.86) * mm, "end": v(4.14, -11) * mm});
            skLineSegment(sketch, "E1011", {"start": v(4.14, -11) * mm, "end": v(4.14, -11.12) * mm});
            skLineSegment(sketch, "E1012", {"start": v(4.14, -11.12) * mm, "end": v(4.14, -11.25) * mm});
            skLineSegment(sketch, "E1013", {"start": v(4.14, -11.25) * mm, "end": v(4.14, -11.38) * mm});
            skLineSegment(sketch, "E1014", {"start": v(4.14, -11.38) * mm, "end": v(4.14, -11.6) * mm});
            skLineSegment(sketch, "E1015", {"start": v(4.14, -11.6) * mm, "end": v(4.14, -11.83) * mm});
            skLineSegment(sketch, "E1016", {"start": v(4.14, -11.83) * mm, "end": v(4.14, -12.06) * mm});
            skLineSegment(sketch, "E1017", {"start": v(4.14, -12.06) * mm, "end": v(4.14, -12.28) * mm});
            skLineSegment(sketch, "E1018", {"start": v(4.14, -12.28) * mm, "end": v(4.14, -12.51) * mm});
            skLineSegment(sketch, "E1019", {"start": v(4.14, -12.51) * mm, "end": v(4.14, -12.74) * mm});
            skLineSegment(sketch, "E1020", {"start": v(4.14, -12.74) * mm, "end": v(4.14, -12.96) * mm});
            skLineSegment(sketch, "E1021", {"start": v(4.14, -12.96) * mm, "end": v(4.14, -13.19) * mm});
            skLineSegment(sketch, "E1022", {"start": v(4.14, -13.19) * mm, "end": v(4.14, -13.42) * mm});
            skLineSegment(sketch, "E1023", {"start": v(4.14, -13.42) * mm, "end": v(4.14, -13.64) * mm});
            skLineSegment(sketch, "E1024", {"start": v(4.14, -13.64) * mm, "end": v(4.14, -13.87) * mm});
            skLineSegment(sketch, "E1025", {"start": v(4.14, -13.87) * mm, "end": v(4.14, -14.1) * mm});
            skLineSegment(sketch, "E1026", {"start": v(4.14, -14.1) * mm, "end": v(4.14, -14.32) * mm});
            skLineSegment(sketch, "E1027", {"start": v(4.14, -14.32) * mm, "end": v(4.14, -14.55) * mm});
            skLineSegment(sketch, "E1028", {"start": v(4.14, -14.55) * mm, "end": v(4.14, -14.77) * mm});
            skLineSegment(sketch, "E1029", {"start": v(4.14, -14.77) * mm, "end": v(4.14, -15) * mm});
            skLineSegment(sketch, "E1030", {"start": v(4.14, -15) * mm, "end": v(4.27, -14.95) * mm});
            skLineSegment(sketch, "E1031", {"start": v(4.27, -14.95) * mm, "end": v(4.4, -14.9) * mm});
            skLineSegment(sketch, "E1032", {"start": v(4.4, -14.9) * mm, "end": v(4.53, -14.84) * mm});
            skLineSegment(sketch, "E1033", {"start": v(4.53, -14.84) * mm, "end": v(4.66, -14.8) * mm});
            skLineSegment(sketch, "E1034", {"start": v(4.66, -14.8) * mm, "end": v(4.78, -14.74) * mm});
            skLineSegment(sketch, "E1035", {"start": v(4.78, -14.74) * mm, "end": v(4.91, -14.69) * mm});
            skLineSegment(sketch, "E1036", {"start": v(4.91, -14.69) * mm, "end": v(5.04, -14.64) * mm});
            skLineSegment(sketch, "E1037", {"start": v(5.04, -14.64) * mm, "end": v(5.17, -14.59) * mm});
            skLineSegment(sketch, "E1038", {"start": v(5.17, -14.59) * mm, "end": v(5.3, -14.53) * mm});
            skLineSegment(sketch, "E1039", {"start": v(5.3, -14.53) * mm, "end": v(5.43, -14.48) * mm});
            skLineSegment(sketch, "E1040", {"start": v(5.43, -14.48) * mm, "end": v(5.56, -14.43) * mm});
            skLineSegment(sketch, "E1041", {"start": v(5.56, -14.43) * mm, "end": v(5.69, -14.38) * mm});
            skLineSegment(sketch, "E1042", {"start": v(5.69, -14.38) * mm, "end": v(5.82, -14.33) * mm});
            skLineSegment(sketch, "E1043", {"start": v(5.82, -14.33) * mm, "end": v(5.95, -14.28) * mm});
            skLineSegment(sketch, "E1044", {"start": v(5.95, -14.28) * mm, "end": v(6.08, -14.22) * mm});
            skLineSegment(sketch, "E1045", {"start": v(6.08, -14.22) * mm, "end": v(6.2, -14.17) * mm});
            skLineSegment(sketch, "E1046", {"start": v(6.2, -14.17) * mm, "end": v(6.24, -14.16) * mm});
            skLineSegment(sketch, "E1047", {"start": v(6.24, -14.16) * mm, "end": v(6.27, -14.15) * mm});
            skLineSegment(sketch, "E1048", {"start": v(6.27, -14.15) * mm, "end": v(6.3, -14.13) * mm});
            skLineSegment(sketch, "E1049", {"start": v(6.3, -14.13) * mm, "end": v(6.34, -14.12) * mm});
            skLineSegment(sketch, "E1050", {"start": v(6.34, -14.12) * mm, "end": v(6.37, -14.1) * mm});
            skLineSegment(sketch, "E1051", {"start": v(6.37, -14.1) * mm, "end": v(6.4, -14.1) * mm});
            skLineSegment(sketch, "E1052", {"start": v(6.4, -14.1) * mm, "end": v(6.43, -14.08) * mm});
            skLineSegment(sketch, "E1053", {"start": v(6.43, -14.08) * mm, "end": v(6.47, -14.07) * mm});
            skLineSegment(sketch, "E1054", {"start": v(6.47, -14.07) * mm, "end": v(6.5, -14.06) * mm});
            skLineSegment(sketch, "E1055", {"start": v(6.5, -14.06) * mm, "end": v(6.53, -14.04) * mm});
            skLineSegment(sketch, "E1056", {"start": v(6.53, -14.04) * mm, "end": v(6.56, -14.03) * mm});
            skLineSegment(sketch, "E1057", {"start": v(6.56, -14.03) * mm, "end": v(6.6, -14.02) * mm});
            skLineSegment(sketch, "E1058", {"start": v(6.6, -14.02) * mm, "end": v(6.63, -14) * mm});
            skLineSegment(sketch, "E1059", {"start": v(6.63, -14) * mm, "end": v(6.66, -14) * mm});
            skLineSegment(sketch, "E1060", {"start": v(6.66, -14) * mm, "end": v(6.7, -13.98) * mm});
            skLineSegment(sketch, "E1061", {"start": v(6.7, -13.98) * mm, "end": v(6.72, -13.97) * mm});
            skLineSegment(sketch, "E1062", {"start": v(6.72, -13.97) * mm, "end": v(6.86, -13.65) * mm});
            skLineSegment(sketch, "E1063", {"start": v(6.86, -13.65) * mm, "end": v(7, -13.33) * mm});
            skLineSegment(sketch, "E1064", {"start": v(7, -13.33) * mm, "end": v(7.12, -13) * mm});
            skLineSegment(sketch, "E1065", {"start": v(7.12, -13) * mm, "end": v(7.26, -12.69) * mm});
            skLineSegment(sketch, "E1066", {"start": v(7.26, -12.69) * mm, "end": v(7.39, -12.37) * mm});
            skLineSegment(sketch, "E1067", {"start": v(7.39, -12.37) * mm, "end": v(7.52, -12.05) * mm});
            skLineSegment(sketch, "E1068", {"start": v(7.52, -12.05) * mm, "end": v(7.66, -11.73) * mm});
            skLineSegment(sketch, "E1069", {"start": v(7.66, -11.73) * mm, "end": v(7.79, -11.4) * mm});
            skLineSegment(sketch, "E1070", {"start": v(7.79, -11.4) * mm, "end": v(7.92, -11.1) * mm});
            skLineSegment(sketch, "E1071", {"start": v(7.92, -11.1) * mm, "end": v(8.06, -10.77) * mm});
            skLineSegment(sketch, "E1072", {"start": v(8.06, -10.77) * mm, "end": v(8.19, -10.45) * mm});
            skLineSegment(sketch, "E1073", {"start": v(8.19, -10.45) * mm, "end": v(8.32, -10.13) * mm});
            skLineSegment(sketch, "E1074", {"start": v(8.32, -10.13) * mm, "end": v(8.45, -9.81) * mm});
            skLineSegment(sketch, "E1075", {"start": v(8.45, -9.81) * mm, "end": v(8.59, -9.5) * mm});
            skLineSegment(sketch, "E1076", {"start": v(8.59, -9.5) * mm, "end": v(8.72, -9.17) * mm});
            skLineSegment(sketch, "E1077", {"start": v(8.72, -9.17) * mm, "end": v(8.85, -8.85) * mm});
            skLineSegment(sketch, "E1078", {"start": v(8.85, -8.85) * mm, "end": v(9.17, -8.72) * mm});
            skLineSegment(sketch, "E1079", {"start": v(9.17, -8.72) * mm, "end": v(9.5, -8.59) * mm});
            skLineSegment(sketch, "E1080", {"start": v(9.5, -8.59) * mm, "end": v(9.81, -8.45) * mm});
            skLineSegment(sketch, "E1081", {"start": v(9.81, -8.45) * mm, "end": v(10.13, -8.32) * mm});
            skLineSegment(sketch, "E1082", {"start": v(10.13, -8.32) * mm, "end": v(10.45, -8.19) * mm});
            skLineSegment(sketch, "E1083", {"start": v(10.45, -8.19) * mm, "end": v(10.77, -8.06) * mm});
            skLineSegment(sketch, "E1084", {"start": v(10.77, -8.06) * mm, "end": v(11.1, -7.92) * mm});
            skLineSegment(sketch, "E1085", {"start": v(11.1, -7.92) * mm, "end": v(11.4, -7.79) * mm});
            skLineSegment(sketch, "E1086", {"start": v(11.4, -7.79) * mm, "end": v(11.73, -7.66) * mm});
            skLineSegment(sketch, "E1087", {"start": v(11.73, -7.66) * mm, "end": v(12.05, -7.52) * mm});
            skLineSegment(sketch, "E1088", {"start": v(12.05, -7.52) * mm, "end": v(12.37, -7.39) * mm});
            skLineSegment(sketch, "E1089", {"start": v(12.37, -7.39) * mm, "end": v(12.69, -7.26) * mm});
            skLineSegment(sketch, "E1090", {"start": v(12.69, -7.26) * mm, "end": v(13, -7.12) * mm});
            skLineSegment(sketch, "E1091", {"start": v(13, -7.12) * mm, "end": v(13.33, -7) * mm});
            skLineSegment(sketch, "E1092", {"start": v(13.33, -7) * mm, "end": v(13.65, -6.86) * mm});
            skLineSegment(sketch, "E1093", {"start": v(13.65, -6.86) * mm, "end": v(13.97, -6.72) * mm});
            skLineSegment(sketch, "E1094", {"start": v(13.97, -6.72) * mm, "end": v(13.98, -6.7) * mm});
            skLineSegment(sketch, "E1095", {"start": v(13.98, -6.7) * mm, "end": v(14, -6.66) * mm});
            skLineSegment(sketch, "E1096", {"start": v(14, -6.66) * mm, "end": v(14, -6.63) * mm});
            skLineSegment(sketch, "E1097", {"start": v(14, -6.63) * mm, "end": v(14.02, -6.6) * mm});
            skLineSegment(sketch, "E1098", {"start": v(14.02, -6.6) * mm, "end": v(14.03, -6.56) * mm});
            skLineSegment(sketch, "E1099", {"start": v(14.03, -6.56) * mm, "end": v(14.04, -6.53) * mm});
            skLineSegment(sketch, "E1100", {"start": v(14.04, -6.53) * mm, "end": v(14.06, -6.5) * mm});
            skLineSegment(sketch, "E1101", {"start": v(14.06, -6.5) * mm, "end": v(14.07, -6.47) * mm});
            skLineSegment(sketch, "E1102", {"start": v(14.07, -6.47) * mm, "end": v(14.08, -6.43) * mm});
            skLineSegment(sketch, "E1103", {"start": v(14.08, -6.43) * mm, "end": v(14.1, -6.4) * mm});
            skLineSegment(sketch, "E1104", {"start": v(14.1, -6.4) * mm, "end": v(14.1, -6.37) * mm});
            skLineSegment(sketch, "E1105", {"start": v(14.1, -6.37) * mm, "end": v(14.12, -6.34) * mm});
            skLineSegment(sketch, "E1106", {"start": v(14.12, -6.34) * mm, "end": v(14.13, -6.3) * mm});
            skLineSegment(sketch, "E1107", {"start": v(14.13, -6.3) * mm, "end": v(14.15, -6.27) * mm});
            skLineSegment(sketch, "E1108", {"start": v(14.15, -6.27) * mm, "end": v(14.16, -6.24) * mm});
            skLineSegment(sketch, "E1109", {"start": v(14.16, -6.24) * mm, "end": v(14.17, -6.2) * mm});
            skLineSegment(sketch, "E1110", {"start": v(14.17, -6.2) * mm, "end": v(14.22, -6.08) * mm});
            skLineSegment(sketch, "E1111", {"start": v(14.22, -6.08) * mm, "end": v(14.28, -5.95) * mm});
            skLineSegment(sketch, "E1112", {"start": v(14.28, -5.95) * mm, "end": v(14.33, -5.82) * mm});
            skLineSegment(sketch, "E1113", {"start": v(14.33, -5.82) * mm, "end": v(14.38, -5.69) * mm});
            skLineSegment(sketch, "E1114", {"start": v(14.38, -5.69) * mm, "end": v(14.43, -5.56) * mm});
            skLineSegment(sketch, "E1115", {"start": v(14.43, -5.56) * mm, "end": v(14.48, -5.43) * mm});
            skLineSegment(sketch, "E1116", {"start": v(14.48, -5.43) * mm, "end": v(14.53, -5.3) * mm});
            skLineSegment(sketch, "E1117", {"start": v(14.53, -5.3) * mm, "end": v(14.59, -5.17) * mm});
            skLineSegment(sketch, "E1118", {"start": v(14.59, -5.17) * mm, "end": v(14.64, -5.04) * mm});
            skLineSegment(sketch, "E1119", {"start": v(14.64, -5.04) * mm, "end": v(14.69, -4.91) * mm});
            skLineSegment(sketch, "E1120", {"start": v(14.69, -4.91) * mm, "end": v(14.74, -4.78) * mm});
            skLineSegment(sketch, "E1121", {"start": v(14.74, -4.78) * mm, "end": v(14.8, -4.66) * mm});
            skLineSegment(sketch, "E1122", {"start": v(14.8, -4.66) * mm, "end": v(14.84, -4.53) * mm});
            skLineSegment(sketch, "E1123", {"start": v(14.84, -4.53) * mm, "end": v(14.9, -4.4) * mm});
            skLineSegment(sketch, "E1124", {"start": v(14.9, -4.4) * mm, "end": v(14.95, -4.27) * mm});
            skLineSegment(sketch, "E1125", {"start": v(14.95, -4.27) * mm, "end": v(15, -4.14) * mm});
            skLineSegment(sketch, "E1126", {"start": v(15, -4.14) * mm, "end": v(14.77, -4.14) * mm});
            skLineSegment(sketch, "E1127", {"start": v(14.77, -4.14) * mm, "end": v(14.55, -4.14) * mm});
            skLineSegment(sketch, "E1128", {"start": v(14.55, -4.14) * mm, "end": v(14.32, -4.14) * mm});
            skLineSegment(sketch, "E1129", {"start": v(14.32, -4.14) * mm, "end": v(14.1, -4.14) * mm});
            skLineSegment(sketch, "E1130", {"start": v(14.1, -4.14) * mm, "end": v(13.87, -4.14) * mm});
            skLineSegment(sketch, "E1131", {"start": v(13.87, -4.14) * mm, "end": v(13.64, -4.14) * mm});
            skLineSegment(sketch, "E1132", {"start": v(13.64, -4.14) * mm, "end": v(13.42, -4.14) * mm});
            skLineSegment(sketch, "E1133", {"start": v(13.42, -4.14) * mm, "end": v(13.19, -4.14) * mm});
            skLineSegment(sketch, "E1134", {"start": v(13.19, -4.14) * mm, "end": v(12.96, -4.14) * mm});
            skLineSegment(sketch, "E1135", {"start": v(12.96, -4.14) * mm, "end": v(12.74, -4.14) * mm});
            skLineSegment(sketch, "E1136", {"start": v(12.74, -4.14) * mm, "end": v(12.51, -4.14) * mm});
            skLineSegment(sketch, "E1137", {"start": v(12.51, -4.14) * mm, "end": v(12.28, -4.14) * mm});
            skLineSegment(sketch, "E1138", {"start": v(12.28, -4.14) * mm, "end": v(12.06, -4.14) * mm});
            skLineSegment(sketch, "E1139", {"start": v(12.06, -4.14) * mm, "end": v(11.83, -4.14) * mm});
            skLineSegment(sketch, "E1140", {"start": v(11.83, -4.14) * mm, "end": v(11.6, -4.14) * mm});
            skLineSegment(sketch, "E1141", {"start": v(11.6, -4.14) * mm, "end": v(11.38, -4.14) * mm});
            skLineSegment(sketch, "E1142", {"start": v(11.38, -4.14) * mm, "end": v(11.25, -4.14) * mm});
            skLineSegment(sketch, "E1143", {"start": v(11.25, -4.14) * mm, "end": v(11.12, -4.14) * mm});
            skLineSegment(sketch, "E1144", {"start": v(11.12, -4.14) * mm, "end": v(11, -4.14) * mm});
            skLineSegment(sketch, "E1145", {"start": v(11, -4.14) * mm, "end": v(10.86, -4.14) * mm});
            skLineSegment(sketch, "E1146", {"start": v(10.86, -4.14) * mm, "end": v(10.73, -4.14) * mm});
            skLineSegment(sketch, "E1147", {"start": v(10.73, -4.14) * mm, "end": v(10.6, -4.14) * mm});
            skLineSegment(sketch, "E1148", {"start": v(10.6, -4.14) * mm, "end": v(10.47, -4.14) * mm});
            skLineSegment(sketch, "E1149", {"start": v(10.47, -4.14) * mm, "end": v(10.34, -4.14) * mm});
            skLineSegment(sketch, "E1150", {"start": v(10.34, -4.14) * mm, "end": v(10.22, -4.14) * mm});
            skLineSegment(sketch, "E1151", {"start": v(10.22, -4.14) * mm, "end": v(10.09, -4.14) * mm});
            skLineSegment(sketch, "E1152", {"start": v(10.09, -4.14) * mm, "end": v(9.96, -4.14) * mm});
            skLineSegment(sketch, "E1153", {"start": v(9.96, -4.14) * mm, "end": v(9.83, -4.14) * mm});
            skLineSegment(sketch, "E1154", {"start": v(9.83, -4.14) * mm, "end": v(9.7, -4.14) * mm});
            skLineSegment(sketch, "E1155", {"start": v(9.7, -4.14) * mm, "end": v(9.57, -4.14) * mm});
            skLineSegment(sketch, "E1156", {"start": v(9.57, -4.14) * mm, "end": v(9.44, -4.14) * mm});
            skLineSegment(sketch, "E1157", {"start": v(9.44, -4.14) * mm, "end": v(9.31, -4.14) * mm});
            skLineSegment(sketch, "E1158", {"start": v(-1.03, -1.03) * mm, "end": v(-1.03, -0.9) * mm});
            skLineSegment(sketch, "E1159", {"start": v(-1.03, -0.9) * mm, "end": v(-1.03, -0.78) * mm});
            skLineSegment(sketch, "E1160", {"start": v(-1.03, -0.78) * mm, "end": v(-1.03, -0.65) * mm});
            skLineSegment(sketch, "E1161", {"start": v(-1.03, -0.65) * mm, "end": v(-1.03, -0.52) * mm});
            skLineSegment(sketch, "E1162", {"start": v(-1.03, -0.52) * mm, "end": v(-1.03, -0.39) * mm});
            skLineSegment(sketch, "E1163", {"start": v(-1.03, -0.39) * mm, "end": v(-1.03, -0.26) * mm});
            skLineSegment(sketch, "E1164", {"start": v(-1.03, -0.26) * mm, "end": v(-1.03, -0.13) * mm});
            skLineSegment(sketch, "E1165", {"start": v(-1.03, -0.13) * mm, "end": v(-1.03, 0) * mm});
            skLineSegment(sketch, "E1166", {"start": v(-1.03, 0) * mm, "end": v(-1.03, 0.13) * mm});
            skLineSegment(sketch, "E1167", {"start": v(-1.03, 0.13) * mm, "end": v(-1.03, 0.26) * mm});
            skLineSegment(sketch, "E1168", {"start": v(-1.03, 0.26) * mm, "end": v(-1.03, 0.39) * mm});
            skLineSegment(sketch, "E1169", {"start": v(-1.03, 0.39) * mm, "end": v(-1.03, 0.52) * mm});
            skLineSegment(sketch, "E1170", {"start": v(-1.03, 0.52) * mm, "end": v(-1.03, 0.65) * mm});
            skLineSegment(sketch, "E1171", {"start": v(-1.03, 0.65) * mm, "end": v(-1.03, 0.78) * mm});
            skLineSegment(sketch, "E1172", {"start": v(-1.03, 0.78) * mm, "end": v(-1.03, 0.9) * mm});
            skLineSegment(sketch, "E1173", {"start": v(-1.03, 0.9) * mm, "end": v(-1.03, 1.03) * mm});
            skLineSegment(sketch, "E1174", {"start": v(-1.03, 1.03) * mm, "end": v(-0.9, 1.03) * mm});
            skLineSegment(sketch, "E1175", {"start": v(-0.9, 1.03) * mm, "end": v(-0.78, 1.03) * mm});
            skLineSegment(sketch, "E1176", {"start": v(-0.78, 1.03) * mm, "end": v(-0.65, 1.03) * mm});
            skLineSegment(sketch, "E1177", {"start": v(-0.65, 1.03) * mm, "end": v(-0.52, 1.03) * mm});
            skLineSegment(sketch, "E1178", {"start": v(-0.52, 1.03) * mm, "end": v(-0.39, 1.03) * mm});
            skLineSegment(sketch, "E1179", {"start": v(-0.39, 1.03) * mm, "end": v(-0.26, 1.03) * mm});
            skLineSegment(sketch, "E1180", {"start": v(-0.26, 1.03) * mm, "end": v(-0.13, 1.03) * mm});
            skLineSegment(sketch, "E1181", {"start": v(-0.13, 1.03) * mm, "end": v(0, 1.03) * mm});
            skLineSegment(sketch, "E1182", {"start": v(0, 1.03) * mm, "end": v(0.13, 1.03) * mm});
            skLineSegment(sketch, "E1183", {"start": v(0.13, 1.03) * mm, "end": v(0.26, 1.03) * mm});
            skLineSegment(sketch, "E1184", {"start": v(0.26, 1.03) * mm, "end": v(0.39, 1.03) * mm});
            skLineSegment(sketch, "E1185", {"start": v(0.39, 1.03) * mm, "end": v(0.52, 1.03) * mm});
            skLineSegment(sketch, "E1186", {"start": v(0.52, 1.03) * mm, "end": v(0.65, 1.03) * mm});
            skLineSegment(sketch, "E1187", {"start": v(0.65, 1.03) * mm, "end": v(0.78, 1.03) * mm});
            skLineSegment(sketch, "E1188", {"start": v(0.78, 1.03) * mm, "end": v(0.9, 1.03) * mm});
            skLineSegment(sketch, "E1189", {"start": v(0.9, 1.03) * mm, "end": v(1.03, 1.03) * mm});
            skLineSegment(sketch, "E1190", {"start": v(1.03, 1.03) * mm, "end": v(1.03, 0.9) * mm});
            skLineSegment(sketch, "E1191", {"start": v(1.03, 0.9) * mm, "end": v(1.03, 0.78) * mm});
            skLineSegment(sketch, "E1192", {"start": v(1.03, 0.78) * mm, "end": v(1.03, 0.65) * mm});
            skLineSegment(sketch, "E1193", {"start": v(1.03, 0.65) * mm, "end": v(1.03, 0.52) * mm});
            skLineSegment(sketch, "E1194", {"start": v(1.03, 0.52) * mm, "end": v(1.03, 0.39) * mm});
            skLineSegment(sketch, "E1195", {"start": v(1.03, 0.39) * mm, "end": v(1.03, 0.26) * mm});
            skLineSegment(sketch, "E1196", {"start": v(1.03, 0.26) * mm, "end": v(1.03, 0.13) * mm});
            skLineSegment(sketch, "E1197", {"start": v(1.03, 0.13) * mm, "end": v(1.03, 0) * mm});
            skLineSegment(sketch, "E1198", {"start": v(1.03, 0) * mm, "end": v(1.03, -0.13) * mm});
            skLineSegment(sketch, "E1199", {"start": v(1.03, -0.13) * mm, "end": v(1.03, -0.26) * mm});
            skLineSegment(sketch, "E1200", {"start": v(1.03, -0.26) * mm, "end": v(1.03, -0.39) * mm});
            skLineSegment(sketch, "E1201", {"start": v(1.03, -0.39) * mm, "end": v(1.03, -0.52) * mm});
            skLineSegment(sketch, "E1202", {"start": v(1.03, -0.52) * mm, "end": v(1.03, -0.65) * mm});
            skLineSegment(sketch, "E1203", {"start": v(1.03, -0.65) * mm, "end": v(1.03, -0.78) * mm});
            skLineSegment(sketch, "E1204", {"start": v(1.03, -0.78) * mm, "end": v(1.03, -0.9) * mm});
            skLineSegment(sketch, "E1205", {"start": v(1.03, -0.9) * mm, "end": v(1.03, -1.03) * mm});
            skLineSegment(sketch, "E1206", {"start": v(1.03, -1.03) * mm, "end": v(0.9, -1.03) * mm});
            skLineSegment(sketch, "E1207", {"start": v(0.9, -1.03) * mm, "end": v(0.78, -1.03) * mm});
            skLineSegment(sketch, "E1208", {"start": v(0.78, -1.03) * mm, "end": v(0.65, -1.03) * mm});
            skLineSegment(sketch, "E1209", {"start": v(0.65, -1.03) * mm, "end": v(0.52, -1.03) * mm});
            skLineSegment(sketch, "E1210", {"start": v(0.52, -1.03) * mm, "end": v(0.39, -1.03) * mm});
            skLineSegment(sketch, "E1211", {"start": v(0.39, -1.03) * mm, "end": v(0.26, -1.03) * mm});
            skLineSegment(sketch, "E1212", {"start": v(0.26, -1.03) * mm, "end": v(0.13, -1.03) * mm});
            skLineSegment(sketch, "E1213", {"start": v(0.13, -1.03) * mm, "end": v(0, -1.03) * mm});
            skLineSegment(sketch, "E1214", {"start": v(0, -1.03) * mm, "end": v(-0.13, -1.03) * mm});
            skLineSegment(sketch, "E1215", {"start": v(-0.13, -1.03) * mm, "end": v(-0.26, -1.03) * mm});
            skLineSegment(sketch, "E1216", {"start": v(-0.26, -1.03) * mm, "end": v(-0.39, -1.03) * mm});
            skLineSegment(sketch, "E1217", {"start": v(-0.39, -1.03) * mm, "end": v(-0.52, -1.03) * mm});
            skLineSegment(sketch, "E1218", {"start": v(-0.52, -1.03) * mm, "end": v(-0.65, -1.03) * mm});
            skLineSegment(sketch, "E1219", {"start": v(-0.65, -1.03) * mm, "end": v(-0.78, -1.03) * mm});
            skLineSegment(sketch, "E1220", {"start": v(-0.78, -1.03) * mm, "end": v(-0.9, -1.03) * mm});
            skLineSegment(sketch, "E1221", {"start": v(-0.9, -1.03) * mm, "end": v(-1.03, -1.03) * mm});
            skSolve(sketch);
        }
        {
            var Q0;
            Q0=makeQuery(id+"F3.imprint","IMPRINT",FACE,{"disambiguationData":[TD([[makeQuery(id+"F3.imprint","IMPRINT",EDGE,{"derivedFrom":sQuery(id+"F3.wireOp",EDGE,"E6")}),1.0]])]});
            extrude(context, id + "F4", {"entities" : qUnion([Q0]), "operationType" : NewBodyOperationType.REMOVE, "oppositeDirection" : true, "depth" : 12 * mm, "offsetDistance" : 25 * mm});
        }
        {
            var Q0;
            Q0=qCreatedBy(makeId("Front.planeOp"),FACE);
            var sketch = newSketch(context, id + "F5", { "sketchPlane" : qUnion([Q0])});
            skCircle(sketch, "E1222", {"center": v(-15, 5) * mm, "radius": 4 * mm});
            skLineSegment(sketch, "E1223", {"start": v(-17.93, 2.28) * mm, "end": v(-15.82, 0) * mm});
            skLineSegment(sketch, "E1224", {"start": v(-16.82, 0) * mm, "end": v(-18.21, 1.17) * mm, "construction": true});
            skLineSegment(sketch, "E1225", {"start": v(-11.94, 2.43) * mm, "end": v(-13.97, 0) * mm});
            skLineSegment(sketch, "E1226", {"start": v(-15.82, 0) * mm, "end": v(-13.97, 0) * mm});
            skSolve(sketch);
        }
        {
            var Q0;
            Q0=qSketchRegion(id+"F5",true);
            var Q1;
            Q1=sQuery(id+"F0.wireOp",EDGE,"E3");
            revolve(context, id + "F6", {"operationType" : NewBodyOperationType.ADD, "surfaceOperationType" : NewSurfaceOperationType.NEW, "entities" : qUnion([Q0]), "axis" : qUnion([Q1]), "revolveType" : RevolveType.FULL});
        }
        {
            var Q0;
            Q0=qCreatedBy(makeId("Top.planeOp"),FACE);
            var sketch = newSketch(context, id + "F7", { "sketchPlane" : qUnion([Q0])});
            skCircle(sketch, "E1227", {"center": v(0, 21) * mm, "radius": 4 * mm});
            skSolve(sketch);
        }
        {
            var Q0;
            Q0=makeQuery(id+"F7.imprint","IMPRINT",FACE,{"disambiguationData":[TD([[makeQuery(id+"F7.imprint","IMPRINT",EDGE,{"derivedFrom":sQuery(id+"F7.wireOp",EDGE,"E1227")}),1.0]])]});
            extrude(context, id + "F8", {"entities" : qUnion([Q0]), "operationType" : NewBodyOperationType.REMOVE, "depth" : 25 * mm, "offsetDistance" : 25 * mm});
        }
        {
            var Q0;
            Q0=makeQuery(id+"F8.boolean.opBoolean","INTERSECT",EDGE,{"derivedFrom":[makeQuery(id+"F4.boolean.opBoolean","SPLIT",FACE,{"disambiguationData":[TD([makeQuery(id+"F1.opRevolve","SWEPT_FACE",FACE,{"disambiguationData":[OSD([sQuery(id+"F0.wireOp",EDGE,"E2")])]}),makeQuery(id+"F4.opExtrude","SWEPT_FACE",FACE,{"disambiguationData":[OSD([sQuery(id+"F3.wireOp",EDGE,"705da5c4-06c6-4740-92ce-35b712dfc936.0")])]}),makeQuery(id+"F4.opExtrude","SWEPT_FACE",FACE,{"disambiguationData":[OSD([sQuery(id+"F3.wireOp",EDGE,"705da5c4-06c6-4740-92ce-35b712dfc936.1")])]}),makeQuery(id+"F4.opExtrude","SWEPT_FACE",FACE,{"disambiguationData":[OSD([sQuery(id+"F3.wireOp",EDGE,"705da5c4-06c6-4740-92ce-35b712dfc936.2")])]}),makeQuery(id+"F4.opExtrude","SWEPT_FACE",FACE,{"disambiguationData":[OSD([sQuery(id+"F3.wireOp",EDGE,"705da5c4-06c6-4740-92ce-35b712dfc936.3")])]}),makeQuery(id+"F4.opExtrude","SWEPT_FACE",FACE,{"disambiguationData":[OSD([sQuery(id+"F3.wireOp",EDGE,"705da5c4-06c6-4740-92ce-35b712dfc936.4")])]}),makeQuery(id+"F4.opExtrude","SWEPT_FACE",FACE,{"disambiguationData":[OSD([sQuery(id+"F3.wireOp",EDGE,"705da5c4-06c6-4740-92ce-35b712dfc936.5")])]})])],"derivedFrom":makeQuery(id+"F1.opRevolve","SWEPT_FACE",FACE,{"disambiguationData":[OSD([sQuery(id+"F0.wireOp",EDGE,"E1")])]})}),makeQuery(id+"F8.opExtrude","SWEPT_FACE",FACE,{"disambiguationData":[OSD([sQuery(id+"F7.wireOp",EDGE,"E1227")])]})]});
            fillet(context, id + "F9", {"entities" : qUnion([Q0]), "radius" : 1 * mm, "tangentPropagation" : true, "allowEdgeOverflow" : false});
        }
        {
            var Q0;
            Q0=makeQuery(id+"F1.opRevolve","SWEPT_FACE",FACE,{"disambiguationData":[OSD([sQuery(id+"F0.wireOp",EDGE,"E2"),sQuery(id+"F0.wireOp",EDGE,"E5")])]});
            var sketch = newSketch(context, id + "F10", { "sketchPlane" : qUnion([Q0])});
            skLineSegment(sketch, "E1228", {"start": v(9.05, -10) * mm, "end": v(9.05, -9.05) * mm});
            skLineSegment(sketch, "E1229", {"start": v(9.05, -9.05) * mm, "end": v(8.1, -9.05) * mm});
            skLineSegment(sketch, "E1230", {"start": v(8.1, -9.05) * mm, "end": v(8.1, -10) * mm});
            skLineSegment(sketch, "E1231", {"start": v(8.1, -10) * mm, "end": v(9.05, -10) * mm});
            skLineSegment(sketch, "E1232", {"start": v(7.14, -8.1) * mm, "end": v(7.14, -9.05) * mm});
            skLineSegment(sketch, "E1233", {"start": v(7.14, -9.05) * mm, "end": v(8.09, -9.04) * mm});
            skLineSegment(sketch, "E1234", {"start": v(8.09, -9.04) * mm, "end": v(8.1, -8.1) * mm});
            skLineSegment(sketch, "E1235", {"start": v(8.1, -8.1) * mm, "end": v(8.1, -7.14) * mm});
            skLineSegment(sketch, "E1236", {"start": v(8.1, -7.14) * mm, "end": v(9.05, -7.14) * mm});
            skLineSegment(sketch, "E1237", {"start": v(9.05, -7.14) * mm, "end": v(9.05, -6.2) * mm});
            skLineSegment(sketch, "E1238", {"start": v(9.05, -6.2) * mm, "end": v(8.1, -6.2) * mm});
            skLineSegment(sketch, "E1239", {"start": v(8.1, -6.2) * mm, "end": v(7.14, -6.2) * mm});
            skLineSegment(sketch, "E1240", {"start": v(7.14, -6.2) * mm, "end": v(7.14, -7.14) * mm});
            skLineSegment(sketch, "E1241", {"start": v(7.14, -7.14) * mm, "end": v(7.14, -8.1) * mm});
            skLineSegment(sketch, "E1242", {"start": v(0.48, -8.1) * mm, "end": v(0.48, -7.14) * mm});
            skLineSegment(sketch, "E1243", {"start": v(0.48, -7.14) * mm, "end": v(-0.48, -7.14) * mm});
            skLineSegment(sketch, "E1244", {"start": v(-0.48, -7.14) * mm, "end": v(-0.48, -8.1) * mm});
            skLineSegment(sketch, "E1245", {"start": v(-0.48, -8.1) * mm, "end": v(0.48, -8.1) * mm});
            skLineSegment(sketch, "E1246", {"start": v(-1.43, -5.24) * mm, "end": v(-2.38, -5.24) * mm});
            skLineSegment(sketch, "E1247", {"start": v(-2.38, -5.24) * mm, "end": v(-2.38, -6.2) * mm});
            skLineSegment(sketch, "E1248", {"start": v(-2.38, -6.2) * mm, "end": v(-2.38, -7.14) * mm});
            skLineSegment(sketch, "E1249", {"start": v(-2.38, -7.14) * mm, "end": v(-2.38, -8.1) * mm});
            skLineSegment(sketch, "E1250", {"start": v(-2.38, -8.1) * mm, "end": v(-2.38, -9.05) * mm});
            skLineSegment(sketch, "E1251", {"start": v(-2.38, -9.05) * mm, "end": v(-2.38, -10) * mm});
            skLineSegment(sketch, "E1252", {"start": v(-2.38, -10) * mm, "end": v(-1.43, -10) * mm});
            skLineSegment(sketch, "E1253", {"start": v(-1.43, -10) * mm, "end": v(-1.43, -9.05) * mm});
            skLineSegment(sketch, "E1254", {"start": v(-1.43, -9.05) * mm, "end": v(-0.48, -9.05) * mm});
            skLineSegment(sketch, "E1255", {"start": v(-0.48, -9.05) * mm, "end": v(-0.49, -8.1) * mm});
            skLineSegment(sketch, "E1256", {"start": v(-0.49, -8.1) * mm, "end": v(-1.43, -8.1) * mm});
            skLineSegment(sketch, "E1257", {"start": v(-1.43, -8.1) * mm, "end": v(-1.43, -7.14) * mm});
            skLineSegment(sketch, "E1258", {"start": v(-1.43, -7.14) * mm, "end": v(-0.49, -7.13) * mm});
            skLineSegment(sketch, "E1259", {"start": v(-0.49, -7.13) * mm, "end": v(-0.48, -6.2) * mm});
            skLineSegment(sketch, "E1260", {"start": v(-0.48, -6.2) * mm, "end": v(-1.43, -6.2) * mm});
            skLineSegment(sketch, "E1261", {"start": v(-1.43, -6.2) * mm, "end": v(-1.43, -5.24) * mm});
            skLineSegment(sketch, "E1262", {"start": v(-7.14, -5.24) * mm, "end": v(-8.1, -5.24) * mm});
            skLineSegment(sketch, "E1263", {"start": v(-8.1, -5.24) * mm, "end": v(-8.1, -6.2) * mm});
            skLineSegment(sketch, "E1264", {"start": v(-8.1, -6.2) * mm, "end": v(-8.1, -7.14) * mm});
            skLineSegment(sketch, "E1265", {"start": v(-8.1, -7.14) * mm, "end": v(-8.1, -8.1) * mm});
            skLineSegment(sketch, "E1266", {"start": v(-8.1, -8.1) * mm, "end": v(-7.14, -8.1) * mm});
            skLineSegment(sketch, "E1267", {"start": v(-7.14, -8.1) * mm, "end": v(-6.2, -8.1) * mm});
            skLineSegment(sketch, "E1268", {"start": v(-6.2, -8.1) * mm, "end": v(-5.24, -8.1) * mm});
            skLineSegment(sketch, "E1269", {"start": v(-5.24, -8.1) * mm, "end": v(-5.24, -7.14) * mm});
            skLineSegment(sketch, "E1270", {"start": v(-5.24, -7.14) * mm, "end": v(-5.24, -6.2) * mm});
            skLineSegment(sketch, "E1271", {"start": v(-5.24, -6.2) * mm, "end": v(-5.24, -5.24) * mm});
            skLineSegment(sketch, "E1272", {"start": v(-5.24, -5.24) * mm, "end": v(-6.2, -5.24) * mm});
            skLineSegment(sketch, "E1273", {"start": v(-6.2, -5.24) * mm, "end": v(-7.14, -5.24) * mm});
            skLineSegment(sketch, "E1274", {"start": v(2.38, -4.29) * mm, "end": v(2.38, -5.24) * mm});
            skLineSegment(sketch, "E1275", {"start": v(2.38, -5.24) * mm, "end": v(3.33, -5.24) * mm});
            skLineSegment(sketch, "E1276", {"start": v(3.33, -5.24) * mm, "end": v(3.33, -4.29) * mm});
            skLineSegment(sketch, "E1277", {"start": v(3.33, -4.29) * mm, "end": v(2.38, -4.29) * mm});
            skLineSegment(sketch, "E1278", {"start": v(1.43, -3.33) * mm, "end": v(1.43, -2.38) * mm});
            skLineSegment(sketch, "E1279", {"start": v(1.43, -2.38) * mm, "end": v(2.38, -2.38) * mm});
            skLineSegment(sketch, "E1280", {"start": v(2.38, -2.38) * mm, "end": v(2.38, -1.43) * mm});
            skLineSegment(sketch, "E1281", {"start": v(2.38, -1.43) * mm, "end": v(1.43, -1.43) * mm});
            skLineSegment(sketch, "E1282", {"start": v(1.43, -1.43) * mm, "end": v(0.48, -1.43) * mm});
            skLineSegment(sketch, "E1283", {"start": v(0.48, -1.43) * mm, "end": v(0.48, -2.38) * mm});
            skLineSegment(sketch, "E1284", {"start": v(0.48, -2.38) * mm, "end": v(-0.48, -2.38) * mm});
            skLineSegment(sketch, "E1285", {"start": v(-0.48, -2.38) * mm, "end": v(-0.47, -3.32) * mm});
            skLineSegment(sketch, "E1286", {"start": v(-0.47, -3.32) * mm, "end": v(0.48, -3.33) * mm});
            skLineSegment(sketch, "E1287", {"start": v(0.48, -3.33) * mm, "end": v(0.48, -4.29) * mm});
            skLineSegment(sketch, "E1288", {"start": v(0.48, -4.29) * mm, "end": v(-0.48, -4.29) * mm});
            skLineSegment(sketch, "E1289", {"start": v(-0.48, -4.29) * mm, "end": v(-0.48, -3.33) * mm});
            skLineSegment(sketch, "E1290", {"start": v(-0.48, -3.33) * mm, "end": v(-1.43, -3.33) * mm});
            skLineSegment(sketch, "E1291", {"start": v(-1.43, -3.33) * mm, "end": v(-1.43, -2.38) * mm});
            skLineSegment(sketch, "E1292", {"start": v(-1.43, -2.38) * mm, "end": v(-2.38, -2.38) * mm});
            skLineSegment(sketch, "E1293", {"start": v(-2.38, -2.38) * mm, "end": v(-2.38, -3.33) * mm});
            skLineSegment(sketch, "E1294", {"start": v(-2.38, -3.33) * mm, "end": v(-2.38, -4.29) * mm});
            skLineSegment(sketch, "E1295", {"start": v(-2.38, -4.29) * mm, "end": v(-1.43, -4.29) * mm});
            skLineSegment(sketch, "E1296", {"start": v(-1.43, -4.29) * mm, "end": v(-1.42, -5.23) * mm});
            skLineSegment(sketch, "E1297", {"start": v(-1.42, -5.23) * mm, "end": v(-0.48, -5.24) * mm});
            skLineSegment(sketch, "E1298", {"start": v(-0.48, -5.24) * mm, "end": v(-0.47, -6.18) * mm});
            skLineSegment(sketch, "E1299", {"start": v(-0.47, -6.18) * mm, "end": v(0.48, -6.2) * mm});
            skLineSegment(sketch, "E1300", {"start": v(0.48, -6.2) * mm, "end": v(1.43, -6.2) * mm});
            skLineSegment(sketch, "E1301", {"start": v(1.43, -6.2) * mm, "end": v(1.43, -5.24) * mm});
            skLineSegment(sketch, "E1302", {"start": v(1.43, -5.24) * mm, "end": v(1.43, -4.29) * mm});
            skLineSegment(sketch, "E1303", {"start": v(1.43, -4.29) * mm, "end": v(2.37, -4.28) * mm});
            skLineSegment(sketch, "E1304", {"start": v(2.37, -4.28) * mm, "end": v(2.38, -3.33) * mm});
            skLineSegment(sketch, "E1305", {"start": v(2.38, -3.33) * mm, "end": v(1.43, -3.33) * mm});
            skLineSegment(sketch, "E1306", {"start": v(-5.24, -3.33) * mm, "end": v(-6.2, -3.33) * mm});
            skLineSegment(sketch, "E1307", {"start": v(-6.2, -3.33) * mm, "end": v(-7.14, -3.33) * mm});
            skLineSegment(sketch, "E1308", {"start": v(-7.14, -3.33) * mm, "end": v(-8.1, -3.33) * mm});
            skLineSegment(sketch, "E1309", {"start": v(-8.1, -3.33) * mm, "end": v(-9.05, -3.33) * mm});
            skLineSegment(sketch, "E1310", {"start": v(-9.05, -3.33) * mm, "end": v(-10, -3.33) * mm});
            skLineSegment(sketch, "E1311", {"start": v(-10, -3.33) * mm, "end": v(-10, -4.29) * mm});
            skLineSegment(sketch, "E1312", {"start": v(-10, -4.29) * mm, "end": v(-10, -5.24) * mm});
            skLineSegment(sketch, "E1313", {"start": v(-10, -5.24) * mm, "end": v(-10, -6.2) * mm});
            skLineSegment(sketch, "E1314", {"start": v(-10, -6.2) * mm, "end": v(-10, -7.14) * mm});
            skLineSegment(sketch, "E1315", {"start": v(-10, -7.14) * mm, "end": v(-10, -8.1) * mm});
            skLineSegment(sketch, "E1316", {"start": v(-10, -8.1) * mm, "end": v(-10, -9.05) * mm});
            skLineSegment(sketch, "E1317", {"start": v(-10, -9.05) * mm, "end": v(-10, -10) * mm});
            skLineSegment(sketch, "E1318", {"start": v(-10, -10) * mm, "end": v(-9.05, -10) * mm});
            skLineSegment(sketch, "E1319", {"start": v(-9.05, -10) * mm, "end": v(-8.1, -10) * mm});
            skLineSegment(sketch, "E1320", {"start": v(-8.1, -10) * mm, "end": v(-7.14, -10) * mm});
            skLineSegment(sketch, "E1321", {"start": v(-7.14, -10) * mm, "end": v(-6.2, -10) * mm});
            skLineSegment(sketch, "E1322", {"start": v(-6.2, -10) * mm, "end": v(-5.24, -10) * mm});
            skLineSegment(sketch, "E1323", {"start": v(-5.24, -10) * mm, "end": v(-4.29, -10) * mm});
            skLineSegment(sketch, "E1324", {"start": v(-4.29, -10) * mm, "end": v(-3.33, -10) * mm});
            skLineSegment(sketch, "E1325", {"start": v(-3.33, -10) * mm, "end": v(-3.33, -9.05) * mm});
            skLineSegment(sketch, "E1326", {"start": v(-3.33, -9.05) * mm, "end": v(-3.33, -8.1) * mm});
            skLineSegment(sketch, "E1327", {"start": v(-3.33, -8.1) * mm, "end": v(-3.33, -7.14) * mm});
            skLineSegment(sketch, "E1328", {"start": v(-3.33, -7.14) * mm, "end": v(-3.33, -6.2) * mm});
            skLineSegment(sketch, "E1329", {"start": v(-3.33, -6.2) * mm, "end": v(-3.33, -5.24) * mm});
            skLineSegment(sketch, "E1330", {"start": v(-3.33, -5.24) * mm, "end": v(-3.33, -4.29) * mm});
            skLineSegment(sketch, "E1331", {"start": v(-3.33, -4.29) * mm, "end": v(-3.33, -3.33) * mm});
            skLineSegment(sketch, "E1332", {"start": v(-3.33, -3.33) * mm, "end": v(-4.29, -3.33) * mm});
            skLineSegment(sketch, "E1333", {"start": v(-4.29, -3.33) * mm, "end": v(-5.24, -3.33) * mm});
            skLineSegment(sketch, "E1334", {"start": v(-4.29, -5.24) * mm, "end": v(-4.29, -6.2) * mm});
            skLineSegment(sketch, "E1335", {"start": v(-4.29, -6.2) * mm, "end": v(-4.29, -7.14) * mm});
            skLineSegment(sketch, "E1336", {"start": v(-4.29, -7.14) * mm, "end": v(-4.29, -8.1) * mm});
            skLineSegment(sketch, "E1337", {"start": v(-4.29, -8.1) * mm, "end": v(-4.29, -9.05) * mm});
            skLineSegment(sketch, "E1338", {"start": v(-4.29, -9.05) * mm, "end": v(-5.24, -9.05) * mm});
            skLineSegment(sketch, "E1339", {"start": v(-5.24, -9.05) * mm, "end": v(-6.2, -9.05) * mm});
            skLineSegment(sketch, "E1340", {"start": v(-6.2, -9.05) * mm, "end": v(-7.14, -9.05) * mm});
            skLineSegment(sketch, "E1341", {"start": v(-7.14, -9.05) * mm, "end": v(-8.1, -9.05) * mm});
            skLineSegment(sketch, "E1342", {"start": v(-8.1, -9.05) * mm, "end": v(-9.05, -9.05) * mm});
            skLineSegment(sketch, "E1343", {"start": v(-9.05, -9.05) * mm, "end": v(-9.05, -8.1) * mm});
            skLineSegment(sketch, "E1344", {"start": v(-9.05, -8.1) * mm, "end": v(-9.05, -7.14) * mm});
            skLineSegment(sketch, "E1345", {"start": v(-9.05, -7.14) * mm, "end": v(-9.05, -6.2) * mm});
            skLineSegment(sketch, "E1346", {"start": v(-9.05, -6.2) * mm, "end": v(-9.05, -5.24) * mm});
            skLineSegment(sketch, "E1347", {"start": v(-9.05, -5.24) * mm, "end": v(-9.05, -4.29) * mm});
            skLineSegment(sketch, "E1348", {"start": v(-9.05, -4.29) * mm, "end": v(-8.1, -4.29) * mm});
            skLineSegment(sketch, "E1349", {"start": v(-8.1, -4.29) * mm, "end": v(-7.14, -4.29) * mm});
            skLineSegment(sketch, "E1350", {"start": v(-7.14, -4.29) * mm, "end": v(-6.2, -4.29) * mm});
            skLineSegment(sketch, "E1351", {"start": v(-6.2, -4.29) * mm, "end": v(-5.24, -4.29) * mm});
            skLineSegment(sketch, "E1352", {"start": v(-5.24, -4.29) * mm, "end": v(-4.29, -4.29) * mm});
            skLineSegment(sketch, "E1353", {"start": v(-4.29, -4.29) * mm, "end": v(-4.29, -5.24) * mm});
            skLineSegment(sketch, "E1354", {"start": v(10, -2.38) * mm, "end": v(10, -1.43) * mm});
            skLineSegment(sketch, "E1355", {"start": v(10, -1.43) * mm, "end": v(9.05, -1.43) * mm});
            skLineSegment(sketch, "E1356", {"start": v(9.05, -1.43) * mm, "end": v(9.05, -2.38) * mm});
            skLineSegment(sketch, "E1357", {"start": v(9.05, -2.38) * mm, "end": v(9.05, -3.33) * mm});
            skLineSegment(sketch, "E1358", {"start": v(9.05, -3.33) * mm, "end": v(10, -3.33) * mm});
            skLineSegment(sketch, "E1359", {"start": v(10, -3.33) * mm, "end": v(10, -2.38) * mm});
            skLineSegment(sketch, "E1360", {"start": v(-3.33, -1.43) * mm, "end": v(-4.29, -1.43) * mm});
            skLineSegment(sketch, "E1361", {"start": v(-4.29, -1.43) * mm, "end": v(-5.24, -1.43) * mm});
            skLineSegment(sketch, "E1362", {"start": v(-5.24, -1.43) * mm, "end": v(-6.2, -1.43) * mm});
            skLineSegment(sketch, "E1363", {"start": v(-6.2, -1.43) * mm, "end": v(-6.2, -2.38) * mm});
            skLineSegment(sketch, "E1364", {"start": v(-6.2, -2.38) * mm, "end": v(-5.24, -2.38) * mm});
            skLineSegment(sketch, "E1365", {"start": v(-5.24, -2.38) * mm, "end": v(-4.29, -2.38) * mm});
            skLineSegment(sketch, "E1366", {"start": v(-4.29, -2.38) * mm, "end": v(-3.33, -2.38) * mm});
            skLineSegment(sketch, "E1367", {"start": v(-3.33, -2.38) * mm, "end": v(-2.4, -2.37) * mm});
            skLineSegment(sketch, "E1368", {"start": v(-2.4, -2.37) * mm, "end": v(-2.38, -1.43) * mm});
            skLineSegment(sketch, "E1369", {"start": v(-2.38, -1.43) * mm, "end": v(-3.33, -1.43) * mm});
            skLineSegment(sketch, "E1370", {"start": v(-0.48, -1.43) * mm, "end": v(-0.48, -0.48) * mm});
            skLineSegment(sketch, "E1371", {"start": v(-0.48, -0.48) * mm, "end": v(0.48, -0.48) * mm});
            skLineSegment(sketch, "E1372", {"start": v(0.48, -0.48) * mm, "end": v(1.43, -0.48) * mm});
            skLineSegment(sketch, "E1373", {"start": v(1.43, -0.48) * mm, "end": v(2.38, -0.48) * mm});
            skLineSegment(sketch, "E1374", {"start": v(2.38, -0.48) * mm, "end": v(2.38, 0.48) * mm});
            skLineSegment(sketch, "E1375", {"start": v(2.38, 0.48) * mm, "end": v(3.33, 0.48) * mm});
            skLineSegment(sketch, "E1376", {"start": v(3.33, 0.48) * mm, "end": v(3.33, 1.43) * mm});
            skLineSegment(sketch, "E1377", {"start": v(3.33, 1.43) * mm, "end": v(3.33, 2.38) * mm});
            skLineSegment(sketch, "E1378", {"start": v(3.33, 2.38) * mm, "end": v(2.38, 2.38) * mm});
            skLineSegment(sketch, "E1379", {"start": v(2.38, 2.38) * mm, "end": v(2.38, 1.43) * mm});
            skLineSegment(sketch, "E1380", {"start": v(2.38, 1.43) * mm, "end": v(1.43, 1.43) * mm});
            skLineSegment(sketch, "E1381", {"start": v(1.43, 1.43) * mm, "end": v(1.43, 0.48) * mm});
            skLineSegment(sketch, "E1382", {"start": v(1.43, 0.48) * mm, "end": v(0.48, 0.48) * mm});
            skLineSegment(sketch, "E1383", {"start": v(0.48, 0.48) * mm, "end": v(0.48, 1.43) * mm});
            skLineSegment(sketch, "E1384", {"start": v(0.48, 1.43) * mm, "end": v(-0.48, 1.43) * mm});
            skLineSegment(sketch, "E1385", {"start": v(-0.48, 1.43) * mm, "end": v(-0.48, 2.38) * mm});
            skLineSegment(sketch, "E1386", {"start": v(-0.48, 2.38) * mm, "end": v(-1.43, 2.38) * mm});
            skLineSegment(sketch, "E1387", {"start": v(-1.43, 2.38) * mm, "end": v(-2.38, 2.38) * mm});
            skLineSegment(sketch, "E1388", {"start": v(-2.38, 2.38) * mm, "end": v(-3.33, 2.38) * mm});
            skLineSegment(sketch, "E1389", {"start": v(-3.33, 2.38) * mm, "end": v(-4.29, 2.38) * mm});
            skLineSegment(sketch, "E1390", {"start": v(-4.29, 2.38) * mm, "end": v(-4.29, 1.43) * mm});
            skLineSegment(sketch, "E1391", {"start": v(-4.29, 1.43) * mm, "end": v(-3.33, 1.43) * mm});
            skLineSegment(sketch, "E1392", {"start": v(-3.33, 1.43) * mm, "end": v(-2.38, 1.43) * mm});
            skLineSegment(sketch, "E1393", {"start": v(-2.38, 1.43) * mm, "end": v(-1.43, 1.43) * mm});
            skLineSegment(sketch, "E1394", {"start": v(-1.43, 1.43) * mm, "end": v(-1.43, 0.48) * mm});
            skLineSegment(sketch, "E1395", {"start": v(-1.43, 0.48) * mm, "end": v(-1.43, -0.48) * mm});
            skLineSegment(sketch, "E1396", {"start": v(-1.43, -0.48) * mm, "end": v(-2.38, -0.48) * mm});
            skLineSegment(sketch, "E1397", {"start": v(-2.38, -0.48) * mm, "end": v(-2.37, -1.42) * mm});
            skLineSegment(sketch, "E1398", {"start": v(-2.37, -1.42) * mm, "end": v(-1.43, -1.43) * mm});
            skLineSegment(sketch, "E1399", {"start": v(-1.43, -1.43) * mm, "end": v(-0.48, -1.43) * mm});
            skLineSegment(sketch, "E1400", {"start": v(4.29, -0.48) * mm, "end": v(4.29, 0.48) * mm});
            skLineSegment(sketch, "E1401", {"start": v(4.29, 0.48) * mm, "end": v(3.34, 0.47) * mm});
            skLineSegment(sketch, "E1402", {"start": v(3.34, 0.47) * mm, "end": v(3.33, -0.48) * mm});
            skLineSegment(sketch, "E1403", {"start": v(3.33, -0.48) * mm, "end": v(4.29, -0.48) * mm});
            skLineSegment(sketch, "E1404", {"start": v(-3.33, 0.48) * mm, "end": v(-4.29, 0.48) * mm});
            skLineSegment(sketch, "E1405", {"start": v(-4.29, 0.48) * mm, "end": v(-4.29, -0.48) * mm});
            skLineSegment(sketch, "E1406", {"start": v(-4.29, -0.48) * mm, "end": v(-3.33, -0.48) * mm});
            skLineSegment(sketch, "E1407", {"start": v(-3.33, -0.48) * mm, "end": v(-2.4, -0.47) * mm});
            skLineSegment(sketch, "E1408", {"start": v(-2.4, -0.47) * mm, "end": v(-2.38, 0.48) * mm});
            skLineSegment(sketch, "E1409", {"start": v(-2.38, 0.48) * mm, "end": v(-3.33, 0.48) * mm});
            skLineSegment(sketch, "E1410", {"start": v(-5.24, 1.43) * mm, "end": v(-5.24, 2.38) * mm});
            skLineSegment(sketch, "E1411", {"start": v(-5.24, 2.38) * mm, "end": v(-6.2, 2.38) * mm});
            skLineSegment(sketch, "E1412", {"start": v(-6.2, 2.38) * mm, "end": v(-7.14, 2.38) * mm});
            skLineSegment(sketch, "E1413", {"start": v(-7.14, 2.38) * mm, "end": v(-8.1, 2.38) * mm});
            skLineSegment(sketch, "E1414", {"start": v(-8.1, 2.38) * mm, "end": v(-9.05, 2.38) * mm});
            skLineSegment(sketch, "E1415", {"start": v(-9.05, 2.38) * mm, "end": v(-10, 2.38) * mm});
            skLineSegment(sketch, "E1416", {"start": v(-10, 2.38) * mm, "end": v(-10, 1.43) * mm});
            skLineSegment(sketch, "E1417", {"start": v(-10, 1.43) * mm, "end": v(-10, 0.48) * mm});
            skLineSegment(sketch, "E1418", {"start": v(-10, 0.48) * mm, "end": v(-10, -0.48) * mm});
            skLineSegment(sketch, "E1419", {"start": v(-10, -0.48) * mm, "end": v(-10, -1.43) * mm});
            skLineSegment(sketch, "E1420", {"start": v(-10, -1.43) * mm, "end": v(-9.05, -1.43) * mm});
            skLineSegment(sketch, "E1421", {"start": v(-9.05, -1.43) * mm, "end": v(-9.05, -2.38) * mm});
            skLineSegment(sketch, "E1422", {"start": v(-9.05, -2.38) * mm, "end": v(-8.1, -2.38) * mm});
            skLineSegment(sketch, "E1423", {"start": v(-8.1, -2.38) * mm, "end": v(-7.14, -2.38) * mm});
            skLineSegment(sketch, "E1424", {"start": v(-7.14, -2.38) * mm, "end": v(-7.14, -1.43) * mm});
            skLineSegment(sketch, "E1425", {"start": v(-7.14, -1.43) * mm, "end": v(-8.1, -1.43) * mm});
            skLineSegment(sketch, "E1426", {"start": v(-8.1, -1.43) * mm, "end": v(-8.1, -0.48) * mm});
            skLineSegment(sketch, "E1427", {"start": v(-8.1, -0.48) * mm, "end": v(-7.14, -0.48) * mm});
            skLineSegment(sketch, "E1428", {"start": v(-7.14, -0.48) * mm, "end": v(-7.15, 0.47) * mm});
            skLineSegment(sketch, "E1429", {"start": v(-7.15, 0.47) * mm, "end": v(-8.1, 0.48) * mm});
            skLineSegment(sketch, "E1430", {"start": v(-8.1, 0.48) * mm, "end": v(-8.1, 1.43) * mm});
            skLineSegment(sketch, "E1431", {"start": v(-8.1, 1.43) * mm, "end": v(-7.14, 1.43) * mm});
            skLineSegment(sketch, "E1432", {"start": v(-7.14, 1.43) * mm, "end": v(-7.14, 0.48) * mm});
            skLineSegment(sketch, "E1433", {"start": v(-7.14, 0.48) * mm, "end": v(-6.2, 0.48) * mm});
            skLineSegment(sketch, "E1434", {"start": v(-6.2, 0.48) * mm, "end": v(-6.2, -0.48) * mm});
            skLineSegment(sketch, "E1435", {"start": v(-6.2, -0.48) * mm, "end": v(-5.24, -0.48) * mm});
            skLineSegment(sketch, "E1436", {"start": v(-5.24, -0.48) * mm, "end": v(-5.24, 0.48) * mm});
            skLineSegment(sketch, "E1437", {"start": v(-5.24, 0.48) * mm, "end": v(-4.29, 0.49) * mm});
            skLineSegment(sketch, "E1438", {"start": v(-4.29, 0.49) * mm, "end": v(-4.29, 1.42) * mm});
            skLineSegment(sketch, "E1439", {"start": v(-4.29, 1.42) * mm, "end": v(-5.23, 1.43) * mm});
            skLineSegment(sketch, "E1440", {"start": v(-5.23, 1.43) * mm, "end": v(-5.24, 1.43) * mm});
            skLineSegment(sketch, "E1441", {"start": v(9.05, 2.38) * mm, "end": v(8.1, 2.38) * mm});
            skLineSegment(sketch, "E1442", {"start": v(8.1, 2.38) * mm, "end": v(8.1, 1.43) * mm});
            skLineSegment(sketch, "E1443", {"start": v(8.1, 1.43) * mm, "end": v(7.14, 1.43) * mm});
            skLineSegment(sketch, "E1444", {"start": v(7.14, 1.43) * mm, "end": v(7.14, 2.38) * mm});
            skLineSegment(sketch, "E1445", {"start": v(7.14, 2.38) * mm, "end": v(6.2, 2.38) * mm});
            skLineSegment(sketch, "E1446", {"start": v(6.2, 2.38) * mm, "end": v(6.2, 1.43) * mm});
            skLineSegment(sketch, "E1447", {"start": v(6.2, 1.43) * mm, "end": v(5.24, 1.43) * mm});
            skLineSegment(sketch, "E1448", {"start": v(5.24, 1.43) * mm, "end": v(5.24, 0.48) * mm});
            skLineSegment(sketch, "E1449", {"start": v(5.24, 0.48) * mm, "end": v(6.2, 0.48) * mm});
            skLineSegment(sketch, "E1450", {"start": v(6.2, 0.48) * mm, "end": v(7.14, 0.48) * mm});
            skLineSegment(sketch, "E1451", {"start": v(7.14, 0.48) * mm, "end": v(7.14, -0.48) * mm});
            skLineSegment(sketch, "E1452", {"start": v(7.14, -0.48) * mm, "end": v(6.2, -0.48) * mm});
            skLineSegment(sketch, "E1453", {"start": v(6.2, -0.48) * mm, "end": v(5.24, -0.48) * mm});
            skLineSegment(sketch, "E1454", {"start": v(5.24, -0.48) * mm, "end": v(5.24, -1.43) * mm});
            skLineSegment(sketch, "E1455", {"start": v(5.24, -1.43) * mm, "end": v(5.24, -2.38) * mm});
            skLineSegment(sketch, "E1456", {"start": v(5.24, -2.38) * mm, "end": v(4.29, -2.38) * mm});
            skLineSegment(sketch, "E1457", {"start": v(4.29, -2.38) * mm, "end": v(4.29, -1.43) * mm});
            skLineSegment(sketch, "E1458", {"start": v(4.29, -1.43) * mm, "end": v(3.33, -1.43) * mm});
            skLineSegment(sketch, "E1459", {"start": v(3.33, -1.43) * mm, "end": v(3.33, -2.38) * mm});
            skLineSegment(sketch, "E1460", {"start": v(3.33, -2.38) * mm, "end": v(2.38, -2.4) * mm});
            skLineSegment(sketch, "E1461", {"start": v(2.38, -2.4) * mm, "end": v(2.38, -3.32) * mm});
            skLineSegment(sketch, "E1462", {"start": v(2.38, -3.32) * mm, "end": v(3.33, -3.33) * mm});
            skLineSegment(sketch, "E1463", {"start": v(3.33, -3.33) * mm, "end": v(3.34, -4.28) * mm});
            skLineSegment(sketch, "E1464", {"start": v(3.34, -4.28) * mm, "end": v(4.29, -4.29) * mm});
            skLineSegment(sketch, "E1465", {"start": v(4.29, -4.29) * mm, "end": v(5.23, -4.28) * mm});
            skLineSegment(sketch, "E1466", {"start": v(5.23, -4.28) * mm, "end": v(5.24, -3.33) * mm});
            skLineSegment(sketch, "E1467", {"start": v(5.24, -3.33) * mm, "end": v(6.2, -3.33) * mm});
            skLineSegment(sketch, "E1468", {"start": v(6.2, -3.33) * mm, "end": v(7.14, -3.33) * mm});
            skLineSegment(sketch, "E1469", {"start": v(7.14, -3.33) * mm, "end": v(7.14, -4.29) * mm});
            skLineSegment(sketch, "E1470", {"start": v(7.14, -4.29) * mm, "end": v(6.2, -4.29) * mm});
            skLineSegment(sketch, "E1471", {"start": v(6.2, -4.29) * mm, "end": v(5.24, -4.29) * mm});
            skLineSegment(sketch, "E1472", {"start": v(5.24, -4.29) * mm, "end": v(5.24, -5.24) * mm});
            skLineSegment(sketch, "E1473", {"start": v(5.24, -5.24) * mm, "end": v(5.24, -6.2) * mm});
            skLineSegment(sketch, "E1474", {"start": v(5.24, -6.2) * mm, "end": v(4.29, -6.2) * mm});
            skLineSegment(sketch, "E1475", {"start": v(4.29, -6.2) * mm, "end": v(4.29, -5.24) * mm});
            skLineSegment(sketch, "E1476", {"start": v(4.29, -5.24) * mm, "end": v(3.34, -5.25) * mm});
            skLineSegment(sketch, "E1477", {"start": v(3.34, -5.25) * mm, "end": v(3.33, -6.2) * mm});
            skLineSegment(sketch, "E1478", {"start": v(3.33, -6.2) * mm, "end": v(3.33, -7.14) * mm});
            skLineSegment(sketch, "E1479", {"start": v(3.33, -7.14) * mm, "end": v(4.29, -7.14) * mm});
            skLineSegment(sketch, "E1480", {"start": v(4.29, -7.14) * mm, "end": v(4.29, -8.1) * mm});
            skLineSegment(sketch, "E1481", {"start": v(4.29, -8.1) * mm, "end": v(4.29, -9.05) * mm});
            skLineSegment(sketch, "E1482", {"start": v(4.29, -9.05) * mm, "end": v(3.33, -9.05) * mm});
            skLineSegment(sketch, "E1483", {"start": v(3.33, -9.05) * mm, "end": v(3.33, -8.1) * mm});
            skLineSegment(sketch, "E1484", {"start": v(3.33, -8.1) * mm, "end": v(2.38, -8.1) * mm});
            skLineSegment(sketch, "E1485", {"start": v(2.38, -8.1) * mm, "end": v(2.38, -7.14) * mm});
            skLineSegment(sketch, "E1486", {"start": v(2.38, -7.14) * mm, "end": v(1.43, -7.14) * mm});
            skLineSegment(sketch, "E1487", {"start": v(1.43, -7.14) * mm, "end": v(1.43, -8.1) * mm});
            skLineSegment(sketch, "E1488", {"start": v(1.43, -8.1) * mm, "end": v(1.43, -9.05) * mm});
            skLineSegment(sketch, "E1489", {"start": v(1.43, -9.05) * mm, "end": v(0.48, -9.05) * mm});
            skLineSegment(sketch, "E1490", {"start": v(0.48, -9.05) * mm, "end": v(0.48, -10) * mm});
            skLineSegment(sketch, "E1491", {"start": v(0.48, -10) * mm, "end": v(1.43, -10) * mm});
            skLineSegment(sketch, "E1492", {"start": v(1.43, -10) * mm, "end": v(2.38, -10) * mm});
            skLineSegment(sketch, "E1493", {"start": v(2.38, -10) * mm, "end": v(3.33, -10) * mm});
            skLineSegment(sketch, "E1494", {"start": v(3.33, -10) * mm, "end": v(4.29, -10) * mm});
            skLineSegment(sketch, "E1495", {"start": v(4.29, -10) * mm, "end": v(5.24, -10) * mm});
            skLineSegment(sketch, "E1496", {"start": v(5.24, -10) * mm, "end": v(6.2, -10) * mm});
            skLineSegment(sketch, "E1497", {"start": v(6.2, -10) * mm, "end": v(7.14, -10) * mm});
            skLineSegment(sketch, "E1498", {"start": v(7.14, -10) * mm, "end": v(7.13, -9.06) * mm});
            skLineSegment(sketch, "E1499", {"start": v(7.13, -9.06) * mm, "end": v(6.2, -9.05) * mm});
            skLineSegment(sketch, "E1500", {"start": v(6.2, -9.05) * mm, "end": v(6.2, -8.1) * mm});
            skLineSegment(sketch, "E1501", {"start": v(6.2, -8.1) * mm, "end": v(5.24, -8.1) * mm});
            skLineSegment(sketch, "E1502", {"start": v(5.24, -8.1) * mm, "end": v(5.24, -7.14) * mm});
            skLineSegment(sketch, "E1503", {"start": v(5.24, -7.14) * mm, "end": v(6.2, -7.14) * mm});
            skLineSegment(sketch, "E1504", {"start": v(6.2, -7.14) * mm, "end": v(6.2, -6.2) * mm});
            skLineSegment(sketch, "E1505", {"start": v(6.2, -6.2) * mm, "end": v(7.13, -6.18) * mm});
            skLineSegment(sketch, "E1506", {"start": v(7.13, -6.18) * mm, "end": v(7.14, -5.24) * mm});
            skLineSegment(sketch, "E1507", {"start": v(7.14, -5.24) * mm, "end": v(8.1, -5.24) * mm});
            skLineSegment(sketch, "E1508", {"start": v(8.1, -5.24) * mm, "end": v(8.1, -4.29) * mm});
            skLineSegment(sketch, "E1509", {"start": v(8.1, -4.29) * mm, "end": v(9.05, -4.29) * mm});
            skLineSegment(sketch, "E1510", {"start": v(9.05, -4.29) * mm, "end": v(9.04, -3.34) * mm});
            skLineSegment(sketch, "E1511", {"start": v(9.04, -3.34) * mm, "end": v(8.1, -3.33) * mm});
            skLineSegment(sketch, "E1512", {"start": v(8.1, -3.33) * mm, "end": v(8.1, -2.38) * mm});
            skLineSegment(sketch, "E1513", {"start": v(8.1, -2.38) * mm, "end": v(7.14, -2.38) * mm});
            skLineSegment(sketch, "E1514", {"start": v(7.14, -2.38) * mm, "end": v(7.14, -1.43) * mm});
            skLineSegment(sketch, "E1515", {"start": v(7.14, -1.43) * mm, "end": v(8.1, -1.43) * mm});
            skLineSegment(sketch, "E1516", {"start": v(8.1, -1.43) * mm, "end": v(8.1, -0.48) * mm});
            skLineSegment(sketch, "E1517", {"start": v(8.1, -0.48) * mm, "end": v(9.05, -0.48) * mm});
            skLineSegment(sketch, "E1518", {"start": v(9.05, -0.48) * mm, "end": v(9.05, 0.48) * mm});
            skLineSegment(sketch, "E1519", {"start": v(9.05, 0.48) * mm, "end": v(10, 0.48) * mm});
            skLineSegment(sketch, "E1520", {"start": v(10, 0.48) * mm, "end": v(10, 1.43) * mm});
            skLineSegment(sketch, "E1521", {"start": v(10, 1.43) * mm, "end": v(9.05, 1.43) * mm});
            skLineSegment(sketch, "E1522", {"start": v(9.05, 1.43) * mm, "end": v(9.05, 2.38) * mm});
            skLineSegment(sketch, "E1523", {"start": v(4.29, 2.38) * mm, "end": v(4.29, 1.43) * mm});
            skLineSegment(sketch, "E1524", {"start": v(4.29, 1.43) * mm, "end": v(5.23, 1.44) * mm});
            skLineSegment(sketch, "E1525", {"start": v(5.23, 1.44) * mm, "end": v(5.24, 2.38) * mm});
            skLineSegment(sketch, "E1526", {"start": v(5.24, 2.38) * mm, "end": v(4.29, 2.38) * mm});
            skLineSegment(sketch, "E1527", {"start": v(0.48, 3.33) * mm, "end": v(0.48, 4.29) * mm});
            skLineSegment(sketch, "E1528", {"start": v(0.48, 4.29) * mm, "end": v(1.43, 4.29) * mm});
            skLineSegment(sketch, "E1529", {"start": v(1.43, 4.29) * mm, "end": v(1.43, 3.33) * mm});
            skLineSegment(sketch, "E1530", {"start": v(1.43, 3.33) * mm, "end": v(1.43, 2.38) * mm});
            skLineSegment(sketch, "E1531", {"start": v(1.43, 2.38) * mm, "end": v(2.37, 2.4) * mm});
            skLineSegment(sketch, "E1532", {"start": v(2.37, 2.4) * mm, "end": v(2.38, 3.33) * mm});
            skLineSegment(sketch, "E1533", {"start": v(2.38, 3.33) * mm, "end": v(2.38, 4.29) * mm});
            skLineSegment(sketch, "E1534", {"start": v(2.38, 4.29) * mm, "end": v(2.38, 5.24) * mm});
            skLineSegment(sketch, "E1535", {"start": v(2.38, 5.24) * mm, "end": v(1.43, 5.24) * mm});
            skLineSegment(sketch, "E1536", {"start": v(1.43, 5.24) * mm, "end": v(1.43, 6.2) * mm});
            skLineSegment(sketch, "E1537", {"start": v(1.43, 6.2) * mm, "end": v(2.38, 6.2) * mm});
            skLineSegment(sketch, "E1538", {"start": v(2.38, 6.2) * mm, "end": v(2.38, 7.14) * mm});
            skLineSegment(sketch, "E1539", {"start": v(2.38, 7.14) * mm, "end": v(2.38, 8.1) * mm});
            skLineSegment(sketch, "E1540", {"start": v(2.38, 8.1) * mm, "end": v(2.38, 9.05) * mm});
            skLineSegment(sketch, "E1541", {"start": v(2.38, 9.05) * mm, "end": v(1.43, 9.05) * mm});
            skLineSegment(sketch, "E1542", {"start": v(1.43, 9.05) * mm, "end": v(0.48, 9.05) * mm});
            skLineSegment(sketch, "E1543", {"start": v(0.48, 9.05) * mm, "end": v(-0.48, 9.05) * mm});
            skLineSegment(sketch, "E1544", {"start": v(-0.48, 9.05) * mm, "end": v(-0.48, 10) * mm});
            skLineSegment(sketch, "E1545", {"start": v(-0.48, 10) * mm, "end": v(-1.43, 10) * mm});
            skLineSegment(sketch, "E1546", {"start": v(-1.43, 10) * mm, "end": v(-1.43, 9.05) * mm});
            skLineSegment(sketch, "E1547", {"start": v(-1.43, 9.05) * mm, "end": v(-2.38, 9.05) * mm});
            skLineSegment(sketch, "E1548", {"start": v(-2.38, 9.05) * mm, "end": v(-2.38, 8.1) * mm});
            skLineSegment(sketch, "E1549", {"start": v(-2.38, 8.1) * mm, "end": v(-1.43, 8.1) * mm});
            skLineSegment(sketch, "E1550", {"start": v(-1.43, 8.1) * mm, "end": v(-1.43, 7.14) * mm});
            skLineSegment(sketch, "E1551", {"start": v(-1.43, 7.14) * mm, "end": v(-2.38, 7.14) * mm});
            skLineSegment(sketch, "E1552", {"start": v(-2.38, 7.14) * mm, "end": v(-2.38, 6.2) * mm});
            skLineSegment(sketch, "E1553", {"start": v(-2.38, 6.2) * mm, "end": v(-1.43, 6.2) * mm});
            skLineSegment(sketch, "E1554", {"start": v(-1.43, 6.2) * mm, "end": v(-0.49, 6.2) * mm});
            skLineSegment(sketch, "E1555", {"start": v(-0.49, 6.2) * mm, "end": v(-0.48, 7.14) * mm});
            skLineSegment(sketch, "E1556", {"start": v(-0.48, 7.14) * mm, "end": v(-0.48, 8.1) * mm});
            skLineSegment(sketch, "E1557", {"start": v(-0.48, 8.1) * mm, "end": v(0.48, 8.1) * mm});
            skLineSegment(sketch, "E1558", {"start": v(0.48, 8.1) * mm, "end": v(0.48, 7.14) * mm});
            skLineSegment(sketch, "E1559", {"start": v(0.48, 7.14) * mm, "end": v(0.48, 6.2) * mm});
            skLineSegment(sketch, "E1560", {"start": v(0.48, 6.2) * mm, "end": v(-0.48, 6.2) * mm});
            skLineSegment(sketch, "E1561", {"start": v(-0.48, 6.2) * mm, "end": v(-0.48, 5.24) * mm});
            skLineSegment(sketch, "E1562", {"start": v(-0.48, 5.24) * mm, "end": v(-1.43, 5.24) * mm});
            skLineSegment(sketch, "E1563", {"start": v(-1.43, 5.24) * mm, "end": v(-2.38, 5.24) * mm});
            skLineSegment(sketch, "E1564", {"start": v(-2.38, 5.24) * mm, "end": v(-2.38, 4.29) * mm});
            skLineSegment(sketch, "E1565", {"start": v(-2.38, 4.29) * mm, "end": v(-2.38, 3.33) * mm});
            skLineSegment(sketch, "E1566", {"start": v(-2.38, 3.33) * mm, "end": v(-1.43, 3.33) * mm});
            skLineSegment(sketch, "E1567", {"start": v(-1.43, 3.33) * mm, "end": v(-1.43, 4.29) * mm});
            skLineSegment(sketch, "E1568", {"start": v(-1.43, 4.29) * mm, "end": v(-0.48, 4.29) * mm});
            skLineSegment(sketch, "E1569", {"start": v(-0.48, 4.29) * mm, "end": v(-0.48, 3.33) * mm});
            skLineSegment(sketch, "E1570", {"start": v(-0.48, 3.33) * mm, "end": v(-0.47, 2.4) * mm});
            skLineSegment(sketch, "E1571", {"start": v(-0.47, 2.4) * mm, "end": v(0.48, 2.38) * mm});
            skLineSegment(sketch, "E1572", {"start": v(0.48, 2.38) * mm, "end": v(0.48, 3.33) * mm});
            skLineSegment(sketch, "E1573", {"start": v(-8.1, 3.33) * mm, "end": v(-7.14, 3.33) * mm});
            skLineSegment(sketch, "E1574", {"start": v(-7.14, 3.33) * mm, "end": v(-6.2, 3.33) * mm});
            skLineSegment(sketch, "E1575", {"start": v(-6.2, 3.33) * mm, "end": v(-5.24, 3.33) * mm});
            skLineSegment(sketch, "E1576", {"start": v(-5.24, 3.33) * mm, "end": v(-4.29, 3.33) * mm});
            skLineSegment(sketch, "E1577", {"start": v(-4.29, 3.33) * mm, "end": v(-3.33, 3.33) * mm});
            skLineSegment(sketch, "E1578", {"start": v(-3.33, 3.33) * mm, "end": v(-3.33, 4.29) * mm});
            skLineSegment(sketch, "E1579", {"start": v(-3.33, 4.29) * mm, "end": v(-3.33, 5.24) * mm});
            skLineSegment(sketch, "E1580", {"start": v(-3.33, 5.24) * mm, "end": v(-3.33, 6.2) * mm});
            skLineSegment(sketch, "E1581", {"start": v(-3.33, 6.2) * mm, "end": v(-3.33, 7.14) * mm});
            skLineSegment(sketch, "E1582", {"start": v(-3.33, 7.14) * mm, "end": v(-3.33, 8.1) * mm});
            skLineSegment(sketch, "E1583", {"start": v(-3.33, 8.1) * mm, "end": v(-3.33, 9.05) * mm});
            skLineSegment(sketch, "E1584", {"start": v(-3.33, 9.05) * mm, "end": v(-3.33, 10) * mm});
            skLineSegment(sketch, "E1585", {"start": v(-3.33, 10) * mm, "end": v(-4.29, 10) * mm});
            skLineSegment(sketch, "E1586", {"start": v(-4.29, 10) * mm, "end": v(-5.24, 10) * mm});
            skLineSegment(sketch, "E1587", {"start": v(-5.24, 10) * mm, "end": v(-6.2, 10) * mm});
            skLineSegment(sketch, "E1588", {"start": v(-6.2, 10) * mm, "end": v(-7.14, 10) * mm});
            skLineSegment(sketch, "E1589", {"start": v(-7.14, 10) * mm, "end": v(-8.1, 10) * mm});
            skLineSegment(sketch, "E1590", {"start": v(-8.1, 10) * mm, "end": v(-9.05, 10) * mm});
            skLineSegment(sketch, "E1591", {"start": v(-9.05, 10) * mm, "end": v(-10, 10) * mm});
            skLineSegment(sketch, "E1592", {"start": v(-10, 10) * mm, "end": v(-10, 9.05) * mm});
            skLineSegment(sketch, "E1593", {"start": v(-10, 9.05) * mm, "end": v(-10, 8.1) * mm});
            skLineSegment(sketch, "E1594", {"start": v(-10, 8.1) * mm, "end": v(-10, 7.14) * mm});
            skLineSegment(sketch, "E1595", {"start": v(-10, 7.14) * mm, "end": v(-10, 6.2) * mm});
            skLineSegment(sketch, "E1596", {"start": v(-10, 6.2) * mm, "end": v(-10, 5.24) * mm});
            skLineSegment(sketch, "E1597", {"start": v(-10, 5.24) * mm, "end": v(-10, 4.29) * mm});
            skLineSegment(sketch, "E1598", {"start": v(-10, 4.29) * mm, "end": v(-10, 3.33) * mm});
            skLineSegment(sketch, "E1599", {"start": v(-10, 3.33) * mm, "end": v(-9.05, 3.33) * mm});
            skLineSegment(sketch, "E1600", {"start": v(-9.05, 3.33) * mm, "end": v(-8.1, 3.33) * mm});
            skLineSegment(sketch, "E1601", {"start": v(-9.05, 5.24) * mm, "end": v(-9.05, 6.2) * mm});
            skLineSegment(sketch, "E1602", {"start": v(-9.05, 6.2) * mm, "end": v(-9.05, 7.14) * mm});
            skLineSegment(sketch, "E1603", {"start": v(-9.05, 7.14) * mm, "end": v(-9.05, 8.1) * mm});
            skLineSegment(sketch, "E1604", {"start": v(-9.05, 8.1) * mm, "end": v(-9.05, 9.05) * mm});
            skLineSegment(sketch, "E1605", {"start": v(-9.05, 9.05) * mm, "end": v(-8.1, 9.05) * mm});
            skLineSegment(sketch, "E1606", {"start": v(-8.1, 9.05) * mm, "end": v(-7.14, 9.05) * mm});
            skLineSegment(sketch, "E1607", {"start": v(-7.14, 9.05) * mm, "end": v(-6.2, 9.05) * mm});
            skLineSegment(sketch, "E1608", {"start": v(-6.2, 9.05) * mm, "end": v(-5.24, 9.05) * mm});
            skLineSegment(sketch, "E1609", {"start": v(-5.24, 9.05) * mm, "end": v(-4.29, 9.05) * mm});
            skLineSegment(sketch, "E1610", {"start": v(-4.29, 9.05) * mm, "end": v(-4.29, 8.1) * mm});
            skLineSegment(sketch, "E1611", {"start": v(-4.29, 8.1) * mm, "end": v(-4.29, 7.14) * mm});
            skLineSegment(sketch, "E1612", {"start": v(-4.29, 7.14) * mm, "end": v(-4.29, 6.2) * mm});
            skLineSegment(sketch, "E1613", {"start": v(-4.29, 6.2) * mm, "end": v(-4.29, 5.24) * mm});
            skLineSegment(sketch, "E1614", {"start": v(-4.29, 5.24) * mm, "end": v(-4.29, 4.29) * mm});
            skLineSegment(sketch, "E1615", {"start": v(-4.29, 4.29) * mm, "end": v(-5.24, 4.29) * mm});
            skLineSegment(sketch, "E1616", {"start": v(-5.24, 4.29) * mm, "end": v(-6.2, 4.29) * mm});
            skLineSegment(sketch, "E1617", {"start": v(-6.2, 4.29) * mm, "end": v(-7.14, 4.29) * mm});
            skLineSegment(sketch, "E1618", {"start": v(-7.14, 4.29) * mm, "end": v(-8.1, 4.29) * mm});
            skLineSegment(sketch, "E1619", {"start": v(-8.1, 4.29) * mm, "end": v(-9.05, 4.29) * mm});
            skLineSegment(sketch, "E1620", {"start": v(-9.05, 4.29) * mm, "end": v(-9.05, 5.24) * mm});
            skLineSegment(sketch, "E1621", {"start": v(-6.2, 5.24) * mm, "end": v(-5.24, 5.24) * mm});
            skLineSegment(sketch, "E1622", {"start": v(-5.24, 5.24) * mm, "end": v(-5.24, 6.2) * mm});
            skLineSegment(sketch, "E1623", {"start": v(-5.24, 6.2) * mm, "end": v(-5.24, 7.14) * mm});
            skLineSegment(sketch, "E1624", {"start": v(-5.24, 7.14) * mm, "end": v(-5.24, 8.1) * mm});
            skLineSegment(sketch, "E1625", {"start": v(-5.24, 8.1) * mm, "end": v(-6.2, 8.1) * mm});
            skLineSegment(sketch, "E1626", {"start": v(-6.2, 8.1) * mm, "end": v(-7.14, 8.1) * mm});
            skLineSegment(sketch, "E1627", {"start": v(-7.14, 8.1) * mm, "end": v(-8.1, 8.1) * mm});
            skLineSegment(sketch, "E1628", {"start": v(-8.1, 8.1) * mm, "end": v(-8.1, 7.14) * mm});
            skLineSegment(sketch, "E1629", {"start": v(-8.1, 7.14) * mm, "end": v(-8.1, 6.2) * mm});
            skLineSegment(sketch, "E1630", {"start": v(-8.1, 6.2) * mm, "end": v(-8.1, 5.24) * mm});
            skLineSegment(sketch, "E1631", {"start": v(-8.1, 5.24) * mm, "end": v(-7.14, 5.24) * mm});
            skLineSegment(sketch, "E1632", {"start": v(-7.14, 5.24) * mm, "end": v(-6.2, 5.24) * mm});
            skLineSegment(sketch, "E1633", {"start": v(6.2, 8.1) * mm, "end": v(5.24, 8.1) * mm});
            skLineSegment(sketch, "E1634", {"start": v(5.24, 8.1) * mm, "end": v(5.24, 7.14) * mm});
            skLineSegment(sketch, "E1635", {"start": v(5.24, 7.14) * mm, "end": v(5.24, 6.2) * mm});
            skLineSegment(sketch, "E1636", {"start": v(5.24, 6.2) * mm, "end": v(5.24, 5.24) * mm});
            skLineSegment(sketch, "E1637", {"start": v(5.24, 5.24) * mm, "end": v(6.2, 5.24) * mm});
            skLineSegment(sketch, "E1638", {"start": v(6.2, 5.24) * mm, "end": v(7.14, 5.24) * mm});
            skLineSegment(sketch, "E1639", {"start": v(7.14, 5.24) * mm, "end": v(8.1, 5.24) * mm});
            skLineSegment(sketch, "E1640", {"start": v(8.1, 5.24) * mm, "end": v(8.1, 6.2) * mm});
            skLineSegment(sketch, "E1641", {"start": v(8.1, 6.2) * mm, "end": v(8.1, 7.14) * mm});
            skLineSegment(sketch, "E1642", {"start": v(8.1, 7.14) * mm, "end": v(8.1, 8.1) * mm});
            skLineSegment(sketch, "E1643", {"start": v(8.1, 8.1) * mm, "end": v(7.14, 8.1) * mm});
            skLineSegment(sketch, "E1644", {"start": v(7.14, 8.1) * mm, "end": v(6.2, 8.1) * mm});
            skLineSegment(sketch, "E1645", {"start": v(9.05, 10) * mm, "end": v(8.1, 10) * mm});
            skLineSegment(sketch, "E1646", {"start": v(8.1, 10) * mm, "end": v(7.14, 10) * mm});
            skLineSegment(sketch, "E1647", {"start": v(7.14, 10) * mm, "end": v(6.2, 10) * mm});
            skLineSegment(sketch, "E1648", {"start": v(6.2, 10) * mm, "end": v(5.24, 10) * mm});
            skLineSegment(sketch, "E1649", {"start": v(5.24, 10) * mm, "end": v(4.29, 10) * mm});
            skLineSegment(sketch, "E1650", {"start": v(4.29, 10) * mm, "end": v(3.33, 10) * mm});
            skLineSegment(sketch, "E1651", {"start": v(3.33, 10) * mm, "end": v(3.33, 9.05) * mm});
            skLineSegment(sketch, "E1652", {"start": v(3.33, 9.05) * mm, "end": v(3.33, 8.1) * mm});
            skLineSegment(sketch, "E1653", {"start": v(3.33, 8.1) * mm, "end": v(3.33, 7.14) * mm});
            skLineSegment(sketch, "E1654", {"start": v(3.33, 7.14) * mm, "end": v(3.33, 6.2) * mm});
            skLineSegment(sketch, "E1655", {"start": v(3.33, 6.2) * mm, "end": v(3.33, 5.24) * mm});
            skLineSegment(sketch, "E1656", {"start": v(3.33, 5.24) * mm, "end": v(3.33, 4.29) * mm});
            skLineSegment(sketch, "E1657", {"start": v(3.33, 4.29) * mm, "end": v(3.33, 3.33) * mm});
            skLineSegment(sketch, "E1658", {"start": v(3.33, 3.33) * mm, "end": v(4.29, 3.33) * mm});
            skLineSegment(sketch, "E1659", {"start": v(4.29, 3.33) * mm, "end": v(5.24, 3.33) * mm});
            skLineSegment(sketch, "E1660", {"start": v(5.24, 3.33) * mm, "end": v(6.2, 3.33) * mm});
            skLineSegment(sketch, "E1661", {"start": v(6.2, 3.33) * mm, "end": v(7.14, 3.33) * mm});
            skLineSegment(sketch, "E1662", {"start": v(7.14, 3.33) * mm, "end": v(8.1, 3.33) * mm});
            skLineSegment(sketch, "E1663", {"start": v(8.1, 3.33) * mm, "end": v(9.05, 3.33) * mm});
            skLineSegment(sketch, "E1664", {"start": v(9.05, 3.33) * mm, "end": v(10, 3.33) * mm});
            skLineSegment(sketch, "E1665", {"start": v(10, 3.33) * mm, "end": v(10, 4.29) * mm});
            skLineSegment(sketch, "E1666", {"start": v(10, 4.29) * mm, "end": v(10, 5.24) * mm});
            skLineSegment(sketch, "E1667", {"start": v(10, 5.24) * mm, "end": v(10, 6.2) * mm});
            skLineSegment(sketch, "E1668", {"start": v(10, 6.2) * mm, "end": v(10, 7.14) * mm});
            skLineSegment(sketch, "E1669", {"start": v(10, 7.14) * mm, "end": v(10, 8.1) * mm});
            skLineSegment(sketch, "E1670", {"start": v(10, 8.1) * mm, "end": v(10, 9.05) * mm});
            skLineSegment(sketch, "E1671", {"start": v(10, 9.05) * mm, "end": v(10, 10) * mm});
            skLineSegment(sketch, "E1672", {"start": v(10, 10) * mm, "end": v(9.05, 10) * mm});
            skLineSegment(sketch, "E1673", {"start": v(9.05, 8.1) * mm, "end": v(9.05, 7.14) * mm});
            skLineSegment(sketch, "E1674", {"start": v(9.05, 7.14) * mm, "end": v(9.05, 6.2) * mm});
            skLineSegment(sketch, "E1675", {"start": v(9.05, 6.2) * mm, "end": v(9.05, 5.24) * mm});
            skLineSegment(sketch, "E1676", {"start": v(9.05, 5.24) * mm, "end": v(9.05, 4.29) * mm});
            skLineSegment(sketch, "E1677", {"start": v(9.05, 4.29) * mm, "end": v(8.1, 4.29) * mm});
            skLineSegment(sketch, "E1678", {"start": v(8.1, 4.29) * mm, "end": v(7.14, 4.29) * mm});
            skLineSegment(sketch, "E1679", {"start": v(7.14, 4.29) * mm, "end": v(6.2, 4.29) * mm});
            skLineSegment(sketch, "E1680", {"start": v(6.2, 4.29) * mm, "end": v(5.24, 4.29) * mm});
            skLineSegment(sketch, "E1681", {"start": v(5.24, 4.29) * mm, "end": v(4.29, 4.29) * mm});
            skLineSegment(sketch, "E1682", {"start": v(4.29, 4.29) * mm, "end": v(4.29, 5.24) * mm});
            skLineSegment(sketch, "E1683", {"start": v(4.29, 5.24) * mm, "end": v(4.29, 6.2) * mm});
            skLineSegment(sketch, "E1684", {"start": v(4.29, 6.2) * mm, "end": v(4.29, 7.14) * mm});
            skLineSegment(sketch, "E1685", {"start": v(4.29, 7.14) * mm, "end": v(4.29, 8.1) * mm});
            skLineSegment(sketch, "E1686", {"start": v(4.29, 8.1) * mm, "end": v(4.29, 9.05) * mm});
            skLineSegment(sketch, "E1687", {"start": v(4.29, 9.05) * mm, "end": v(5.24, 9.05) * mm});
            skLineSegment(sketch, "E1688", {"start": v(5.24, 9.05) * mm, "end": v(6.2, 9.05) * mm});
            skLineSegment(sketch, "E1689", {"start": v(6.2, 9.05) * mm, "end": v(7.14, 9.05) * mm});
            skLineSegment(sketch, "E1690", {"start": v(7.14, 9.05) * mm, "end": v(8.1, 9.05) * mm});
            skLineSegment(sketch, "E1691", {"start": v(8.1, 9.05) * mm, "end": v(9.05, 9.05) * mm});
            skLineSegment(sketch, "E1692", {"start": v(9.05, 9.05) * mm, "end": v(9.05, 8.1) * mm});
            skSolve(sketch);
        }
        {
            var Q0;
            Q0 = qSketchRegion(id + "F10", true);
            var Q1;
            Q1=makeQuery(id+"F10.imprint","IMPRINT",FACE,{"disambiguationData":[TD([[makeQuery(id+"F10.imprint","IMPRINT",EDGE,{"derivedFrom":sQuery(id+"F10.wireOp",EDGE,"E1621")}),1.0]])]});
            var Q2;
            Q2=makeQuery(id+"F10.imprint","IMPRINT",FACE,{"disambiguationData":[TD([[makeQuery(id+"F10.imprint","IMPRINT",EDGE,{"derivedFrom":sQuery(id+"F10.wireOp",EDGE,"E1633")}),1.0]])]});
            var Q3;
            Q3=makeQuery(id+"F10.imprint","IMPRINT",FACE,{"disambiguationData":[TD([[makeQuery(id+"F10.imprint","IMPRINT",EDGE,{"derivedFrom":sQuery(id+"F10.wireOp",EDGE,"E1262")}),1.0]])]});
            extrude(context, id + "F11", {"entities" : qUnion([Q0, Q1, Q2, Q3]), "operationType" : NewBodyOperationType.REMOVE, "oppositeDirection" : true, "depth" : 1 * mm, "offsetDistance" : 25 * mm});
        }
    });
